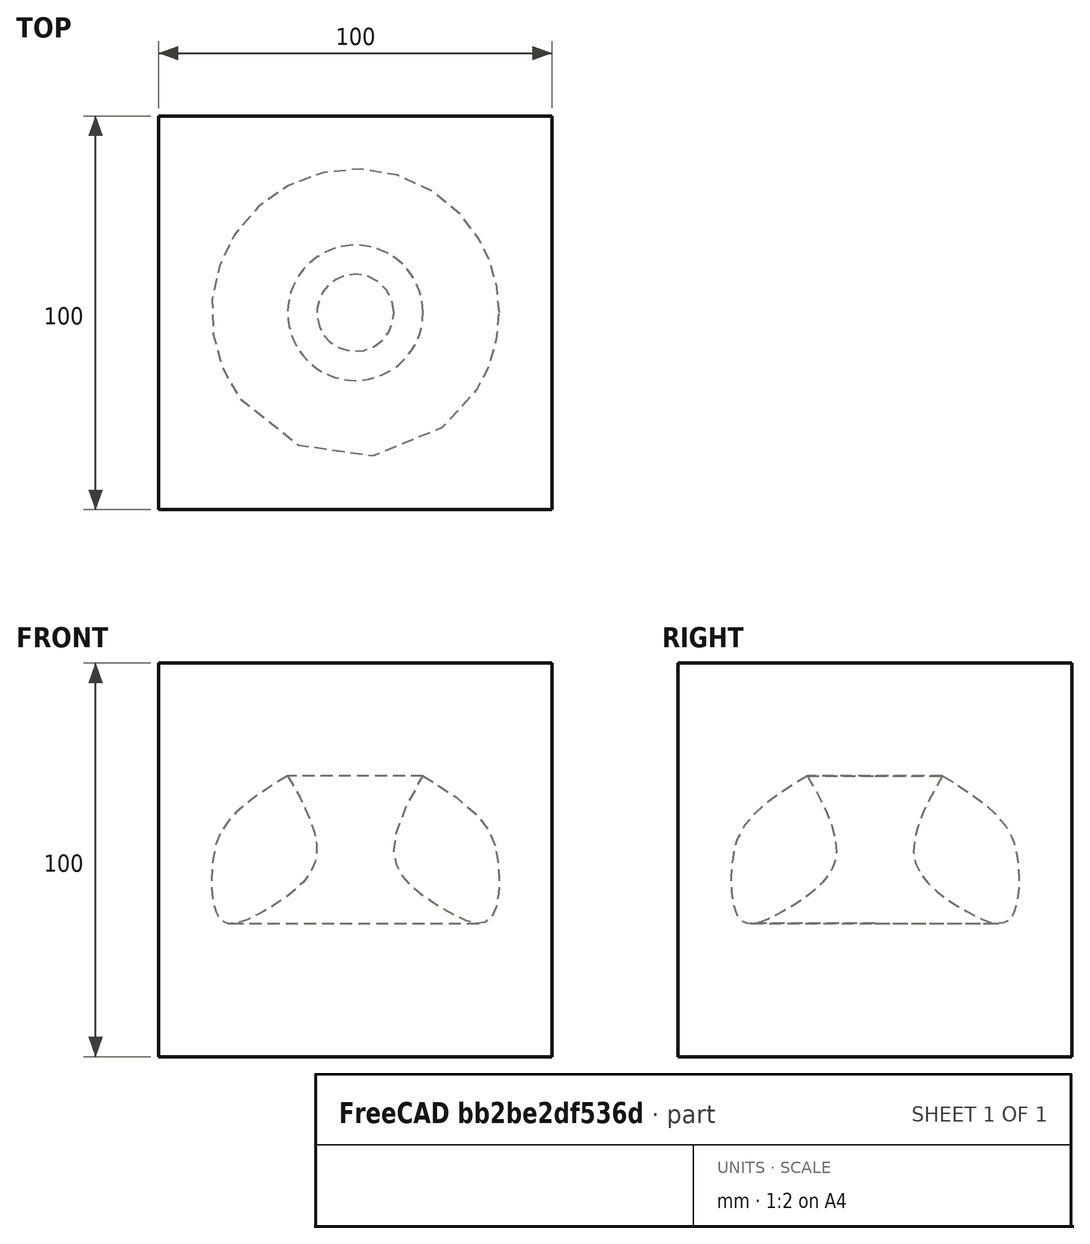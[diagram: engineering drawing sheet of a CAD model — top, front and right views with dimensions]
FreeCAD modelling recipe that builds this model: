
FCSTD DOCUMENT  (FreeCAD 0.21R33694 (Git))
Label: revolveSingleEdge-Bspline
License: All rights reserved
LicenseURL: http://en.wikipedia.org/wiki/All_rights_reserved
objects: App::DocumentObjectGroupPython×1248, App::Part×2, Part::FeaturePython×1, Sketcher::SketchObject×1, Part::Revolution×1
note: 3 computed .brp shape members not serialized (recipe doc carries the construction recipe); baked Part::Feature solids carry a one-line shape summary decoded from their .brp

FEATURE [App::DocumentObjectGroupPython] HALFPI  # scripted group (container) (typed FeaturePython)
  name = HALFPI
  value = pi/2.
FEATURE [App::DocumentObjectGroupPython] PI  # scripted group (container) (typed FeaturePython)
  name = PI
  value = 1.*pi
FEATURE [App::DocumentObjectGroupPython] TWOPI  # scripted group (container) (typed FeaturePython)
  name = TWOPI
  value = 2.*pi
FEATURE [App::DocumentObjectGroupPython] Constants  # scripted group (container) (typed FeaturePython)
  Group = -> [HALFPI,PI,TWOPI]
FEATURE [App::DocumentObjectGroupPython] Variables  # scripted group (container) (typed FeaturePython)
FEATURE [App::DocumentObjectGroupPython] Quantities  # scripted group (container) (typed FeaturePython)
FEATURE [App::DocumentObjectGroupPython] Isotopes  # scripted group (container) (typed FeaturePython)
FEATURE [App::DocumentObjectGroupPython] Elements  # scripted group (container) (typed FeaturePython)
FEATURE [App::DocumentObjectGroupPython] G4Isotopes  # scripted group (container) (typed FeaturePython)
FEATURE [App::DocumentObjectGroupPython] H_element  # scripted group (container) (typed FeaturePython)
  Z = 1
  atom_value = 1.008
  formula = H
  name = H_element
FEATURE [App::DocumentObjectGroupPython] He_element  # scripted group (container) (typed FeaturePython)
  Z = 2
  atom_value = 4.0026
  formula = He
  name = He_element
FEATURE [App::DocumentObjectGroupPython] Li_element  # scripted group (container) (typed FeaturePython)
  Z = 3
  atom_value = 6.94
  formula = Li
  name = Li_element
FEATURE [App::DocumentObjectGroupPython] Be_element  # scripted group (container) (typed FeaturePython)
  Z = 4
  atom_value = 9.01218
  formula = Be
  name = Be_element
FEATURE [App::DocumentObjectGroupPython] B_element  # scripted group (container) (typed FeaturePython)
  Z = 5
  atom_value = 10.81
  formula = B
  name = B_element
FEATURE [App::DocumentObjectGroupPython] C_element  # scripted group (container) (typed FeaturePython)
  Z = 6
  atom_value = 12.011
  formula = C
  name = C_element
FEATURE [App::DocumentObjectGroupPython] N_element  # scripted group (container) (typed FeaturePython)
  Z = 7
  atom_value = 14.007
  formula = N
  name = N_element
FEATURE [App::DocumentObjectGroupPython] O_element  # scripted group (container) (typed FeaturePython)
  Z = 8
  atom_value = 15.999
  formula = O
  name = O_element
FEATURE [App::DocumentObjectGroupPython] F_element  # scripted group (container) (typed FeaturePython)
  Z = 9
  atom_value = 18.9984
  formula = F
  name = F_element
FEATURE [App::DocumentObjectGroupPython] Ne_element  # scripted group (container) (typed FeaturePython)
  Z = 10
  atom_value = 20.1797
  formula = Ne
  name = Ne_element
FEATURE [App::DocumentObjectGroupPython] Na_element  # scripted group (container) (typed FeaturePython)
  Z = 11
  atom_value = 22.9898
  formula = Na
  name = Na_element
FEATURE [App::DocumentObjectGroupPython] Mg_element  # scripted group (container) (typed FeaturePython)
  Z = 12
  atom_value = 24.305
  formula = Mg
  name = Mg_element
FEATURE [App::DocumentObjectGroupPython] Al_element  # scripted group (container) (typed FeaturePython)
  Z = 13
  atom_value = 26.9815
  formula = Al
  name = Al_element
FEATURE [App::DocumentObjectGroupPython] Si_element  # scripted group (container) (typed FeaturePython)
  Z = 14
  atom_value = 28.085
  formula = Si
  name = Si_element
FEATURE [App::DocumentObjectGroupPython] P_element  # scripted group (container) (typed FeaturePython)
  Z = 15
  atom_value = 30.9738
  formula = P
  name = P_element
FEATURE [App::DocumentObjectGroupPython] S_element  # scripted group (container) (typed FeaturePython)
  Z = 16
  atom_value = 32.06
  formula = S
  name = S_element
FEATURE [App::DocumentObjectGroupPython] Cl_element  # scripted group (container) (typed FeaturePython)
  Z = 17
  atom_value = 35.45
  formula = Cl
  name = Cl_element
FEATURE [App::DocumentObjectGroupPython] Ar_element  # scripted group (container) (typed FeaturePython)
  Z = 18
  atom_value = 39.95
  formula = Ar
  name = Ar_element
FEATURE [App::DocumentObjectGroupPython] K_element  # scripted group (container) (typed FeaturePython)
  Z = 19
  atom_value = 39.0983
  formula = K
  name = K_element
FEATURE [App::DocumentObjectGroupPython] Ca_element  # scripted group (container) (typed FeaturePython)
  Z = 20
  atom_value = 40.078
  formula = Ca
  name = Ca_element
FEATURE [App::DocumentObjectGroupPython] Sc_element  # scripted group (container) (typed FeaturePython)
  Z = 21
  atom_value = 44.9559
  formula = Sc
  name = Sc_element
FEATURE [App::DocumentObjectGroupPython] Ti_element  # scripted group (container) (typed FeaturePython)
  Z = 22
  atom_value = 47.867
  formula = Ti
  name = Ti_element
FEATURE [App::DocumentObjectGroupPython] V_element  # scripted group (container) (typed FeaturePython)
  Z = 23
  atom_value = 50.9415
  formula = V
  name = V_element
FEATURE [App::DocumentObjectGroupPython] Cr_element  # scripted group (container) (typed FeaturePython)
  Z = 24
  atom_value = 51.9961
  formula = Cr
  name = Cr_element
FEATURE [App::DocumentObjectGroupPython] Mn_element  # scripted group (container) (typed FeaturePython)
  Z = 25
  atom_value = 54.938
  formula = Mn
  name = Mn_element
FEATURE [App::DocumentObjectGroupPython] Fe_element  # scripted group (container) (typed FeaturePython)
  Z = 26
  atom_value = 55.845
  formula = Fe
  name = Fe_element
FEATURE [App::DocumentObjectGroupPython] Co_element  # scripted group (container) (typed FeaturePython)
  Z = 27
  atom_value = 58.9332
  formula = Co
  name = Co_element
FEATURE [App::DocumentObjectGroupPython] Ni_element  # scripted group (container) (typed FeaturePython)
  Z = 28
  atom_value = 58.6934
  formula = Ni
  name = Ni_element
FEATURE [App::DocumentObjectGroupPython] Cu_element  # scripted group (container) (typed FeaturePython)
  Z = 29
  atom_value = 63.546
  formula = Cu
  name = Cu_element
FEATURE [App::DocumentObjectGroupPython] Zn_element  # scripted group (container) (typed FeaturePython)
  Z = 30
  atom_value = 65.38
  formula = Zn
  name = Zn_element
FEATURE [App::DocumentObjectGroupPython] Ga_element  # scripted group (container) (typed FeaturePython)
  Z = 31
  atom_value = 69.723
  formula = Ga
  name = Ga_element
FEATURE [App::DocumentObjectGroupPython] Ge_element  # scripted group (container) (typed FeaturePython)
  Z = 32
  atom_value = 72.63
  formula = Ge
  name = Ge_element
FEATURE [App::DocumentObjectGroupPython] As_element  # scripted group (container) (typed FeaturePython)
  Z = 33
  atom_value = 74.9216
  formula = As
  name = As_element
FEATURE [App::DocumentObjectGroupPython] Se_element  # scripted group (container) (typed FeaturePython)
  Z = 34
  atom_value = 78.971
  formula = Se
  name = Se_element
FEATURE [App::DocumentObjectGroupPython] Br_element  # scripted group (container) (typed FeaturePython)
  Z = 35
  atom_value = 79.904
  formula = Br
  name = Br_element
FEATURE [App::DocumentObjectGroupPython] Kr_element  # scripted group (container) (typed FeaturePython)
  Z = 36
  atom_value = 83.798
  formula = Kr
  name = Kr_element
FEATURE [App::DocumentObjectGroupPython] Rb_element  # scripted group (container) (typed FeaturePython)
  Z = 37
  atom_value = 85.4678
  formula = Rb
  name = Rb_element
FEATURE [App::DocumentObjectGroupPython] Sr_element  # scripted group (container) (typed FeaturePython)
  Z = 38
  atom_value = 87.62
  formula = Sr
  name = Sr_element
FEATURE [App::DocumentObjectGroupPython] Y_element  # scripted group (container) (typed FeaturePython)
  Z = 39
  atom_value = 88.9058
  formula = Y
  name = Y_element
FEATURE [App::DocumentObjectGroupPython] Zr_element  # scripted group (container) (typed FeaturePython)
  Z = 40
  atom_value = 91.224
  formula = Zr
  name = Zr_element
FEATURE [App::DocumentObjectGroupPython] Nb_element  # scripted group (container) (typed FeaturePython)
  Z = 41
  atom_value = 92.9064
  formula = Nb
  name = Nb_element
FEATURE [App::DocumentObjectGroupPython] Mo_element  # scripted group (container) (typed FeaturePython)
  Z = 42
  atom_value = 95.95
  formula = Mo
  name = Mo_element
FEATURE [App::DocumentObjectGroupPython] Tc_element  # scripted group (container) (typed FeaturePython)
  Z = 43
  atom_value = 97
  formula = Tc
  name = Tc_element
FEATURE [App::DocumentObjectGroupPython] Ru_element  # scripted group (container) (typed FeaturePython)
  Z = 44
  atom_value = 101.07
  formula = Ru
  name = Ru_element
FEATURE [App::DocumentObjectGroupPython] Rh_element  # scripted group (container) (typed FeaturePython)
  Z = 45
  atom_value = 102.905
  formula = Rh
  name = Rh_element
FEATURE [App::DocumentObjectGroupPython] Pd_element  # scripted group (container) (typed FeaturePython)
  Z = 46
  atom_value = 106.42
  formula = Pd
  name = Pd_element
FEATURE [App::DocumentObjectGroupPython] Ag_element  # scripted group (container) (typed FeaturePython)
  Z = 47
  atom_value = 107.868
  formula = Ag
  name = Ag_element
FEATURE [App::DocumentObjectGroupPython] Cd_element  # scripted group (container) (typed FeaturePython)
  Z = 48
  atom_value = 112.414
  formula = Cd
  name = Cd_element
FEATURE [App::DocumentObjectGroupPython] In_element  # scripted group (container) (typed FeaturePython)
  Z = 49
  atom_value = 114.818
  formula = In
  name = In_element
FEATURE [App::DocumentObjectGroupPython] Sn_element  # scripted group (container) (typed FeaturePython)
  Z = 50
  atom_value = 118.71
  formula = Sn
  name = Sn_element
FEATURE [App::DocumentObjectGroupPython] Sb_element  # scripted group (container) (typed FeaturePython)
  Z = 51
  atom_value = 121.76
  formula = Sb
  name = Sb_element
FEATURE [App::DocumentObjectGroupPython] Te_element  # scripted group (container) (typed FeaturePython)
  Z = 52
  atom_value = 127.6
  formula = Te
  name = Te_element
FEATURE [App::DocumentObjectGroupPython] I_element  # scripted group (container) (typed FeaturePython)
  Z = 53
  atom_value = 126.904
  formula = I
  name = I_element
FEATURE [App::DocumentObjectGroupPython] Xe_element  # scripted group (container) (typed FeaturePython)
  Z = 54
  atom_value = 131.293
  formula = Xe
  name = Xe_element
FEATURE [App::DocumentObjectGroupPython] Cs_element  # scripted group (container) (typed FeaturePython)
  Z = 55
  atom_value = 132.905
  formula = Cs
  name = Cs_element
FEATURE [App::DocumentObjectGroupPython] Ba_element  # scripted group (container) (typed FeaturePython)
  Z = 56
  atom_value = 137.327
  formula = Ba
  name = Ba_element
FEATURE [App::DocumentObjectGroupPython] La_element  # scripted group (container) (typed FeaturePython)
  Z = 57
  atom_value = 138.905
  formula = La
  name = La_element
FEATURE [App::DocumentObjectGroupPython] Ce_element  # scripted group (container) (typed FeaturePython)
  Z = 58
  atom_value = 140.116
  formula = Ce
  name = Ce_element
FEATURE [App::DocumentObjectGroupPython] Pr_element  # scripted group (container) (typed FeaturePython)
  Z = 59
  atom_value = 140.908
  formula = Pr
  name = Pr_element
FEATURE [App::DocumentObjectGroupPython] Nd_element  # scripted group (container) (typed FeaturePython)
  Z = 60
  atom_value = 144.242
  formula = Nd
  name = Nd_element
FEATURE [App::DocumentObjectGroupPython] Pm_element  # scripted group (container) (typed FeaturePython)
  Z = 61
  atom_value = 145
  formula = Pm
  name = Pm_element
FEATURE [App::DocumentObjectGroupPython] Sm_element  # scripted group (container) (typed FeaturePython)
  Z = 62
  atom_value = 150.36
  formula = Sm
  name = Sm_element
FEATURE [App::DocumentObjectGroupPython] Eu_element  # scripted group (container) (typed FeaturePython)
  Z = 63
  atom_value = 151.964
  formula = Eu
  name = Eu_element
FEATURE [App::DocumentObjectGroupPython] Gd_element  # scripted group (container) (typed FeaturePython)
  Z = 64
  atom_value = 157.25
  formula = Gd
  name = Gd_element
FEATURE [App::DocumentObjectGroupPython] Tb_element  # scripted group (container) (typed FeaturePython)
  Z = 65
  atom_value = 158.925
  formula = Tb
  name = Tb_element
FEATURE [App::DocumentObjectGroupPython] Dy_element  # scripted group (container) (typed FeaturePython)
  Z = 66
  atom_value = 162.5
  formula = Dy
  name = Dy_element
FEATURE [App::DocumentObjectGroupPython] Ho_element  # scripted group (container) (typed FeaturePython)
  Z = 67
  atom_value = 164.93
  formula = Ho
  name = Ho_element
FEATURE [App::DocumentObjectGroupPython] Er_element  # scripted group (container) (typed FeaturePython)
  Z = 68
  atom_value = 167.259
  formula = Er
  name = Er_element
FEATURE [App::DocumentObjectGroupPython] Tm_element  # scripted group (container) (typed FeaturePython)
  Z = 69
  atom_value = 168.934
  formula = Tm
  name = Tm_element
FEATURE [App::DocumentObjectGroupPython] Yb_element  # scripted group (container) (typed FeaturePython)
  Z = 70
  atom_value = 173.045
  formula = Yb
  name = Yb_element
FEATURE [App::DocumentObjectGroupPython] Lu_element  # scripted group (container) (typed FeaturePython)
  Z = 71
  atom_value = 174.967
  formula = Lu
  name = Lu_element
FEATURE [App::DocumentObjectGroupPython] Hf_element  # scripted group (container) (typed FeaturePython)
  Z = 72
  atom_value = 178.49
  formula = Hf
  name = Hf_element
FEATURE [App::DocumentObjectGroupPython] Ta_element  # scripted group (container) (typed FeaturePython)
  Z = 73
  atom_value = 180.948
  formula = Ta
  name = Ta_element
FEATURE [App::DocumentObjectGroupPython] W_element  # scripted group (container) (typed FeaturePython)
  Z = 74
  atom_value = 183.84
  formula = W
  name = W_element
FEATURE [App::DocumentObjectGroupPython] Re_element  # scripted group (container) (typed FeaturePython)
  Z = 75
  atom_value = 186.207
  formula = Re
  name = Re_element
FEATURE [App::DocumentObjectGroupPython] Os_element  # scripted group (container) (typed FeaturePython)
  Z = 76
  atom_value = 190.23
  formula = Os
  name = Os_element
FEATURE [App::DocumentObjectGroupPython] Ir_element  # scripted group (container) (typed FeaturePython)
  Z = 77
  atom_value = 192.217
  formula = Ir
  name = Ir_element
FEATURE [App::DocumentObjectGroupPython] Pt_element  # scripted group (container) (typed FeaturePython)
  Z = 78
  atom_value = 195.084
  formula = Pt
  name = Pt_element
FEATURE [App::DocumentObjectGroupPython] Au_element  # scripted group (container) (typed FeaturePython)
  Z = 79
  atom_value = 196.967
  formula = Au
  name = Au_element
FEATURE [App::DocumentObjectGroupPython] Hg_element  # scripted group (container) (typed FeaturePython)
  Z = 80
  atom_value = 200.592
  formula = Hg
  name = Hg_element
FEATURE [App::DocumentObjectGroupPython] Tl_element  # scripted group (container) (typed FeaturePython)
  Z = 81
  atom_value = 204.38
  formula = Tl
  name = Tl_element
FEATURE [App::DocumentObjectGroupPython] Pb_element  # scripted group (container) (typed FeaturePython)
  Z = 82
  atom_value = 207.2
  formula = Pb
  name = Pb_element
FEATURE [App::DocumentObjectGroupPython] Bi_element  # scripted group (container) (typed FeaturePython)
  Z = 83
  atom_value = 208.98
  formula = Bi
  name = Bi_element
FEATURE [App::DocumentObjectGroupPython] Po_element  # scripted group (container) (typed FeaturePython)
  Z = 84
  atom_value = 209
  formula = Po
  name = Po_element
FEATURE [App::DocumentObjectGroupPython] At_element  # scripted group (container) (typed FeaturePython)
  Z = 85
  atom_value = 210
  formula = At
  name = At_element
FEATURE [App::DocumentObjectGroupPython] Rn_element  # scripted group (container) (typed FeaturePython)
  Z = 86
  atom_value = 222
  formula = Rn
  name = Rn_element
FEATURE [App::DocumentObjectGroupPython] Fr_element  # scripted group (container) (typed FeaturePython)
  Z = 87
  atom_value = 223
  formula = Fr
  name = Fr_element
FEATURE [App::DocumentObjectGroupPython] Ra_element  # scripted group (container) (typed FeaturePython)
  Z = 88
  atom_value = 226
  formula = Ra
  name = Ra_element
FEATURE [App::DocumentObjectGroupPython] Ac_element  # scripted group (container) (typed FeaturePython)
  Z = 89
  atom_value = 227
  formula = Ac
  name = Ac_element
FEATURE [App::DocumentObjectGroupPython] Th_element  # scripted group (container) (typed FeaturePython)
  Z = 90
  atom_value = 232.038
  formula = Th
  name = Th_element
FEATURE [App::DocumentObjectGroupPython] Pa_element  # scripted group (container) (typed FeaturePython)
  Z = 91
  atom_value = 231.036
  formula = Pa
  name = Pa_element
FEATURE [App::DocumentObjectGroupPython] U_element  # scripted group (container) (typed FeaturePython)
  Z = 92
  atom_value = 238.029
  formula = U
  name = U_element
FEATURE [App::DocumentObjectGroupPython] Np_element  # scripted group (container) (typed FeaturePython)
  Z = 93
  atom_value = 237
  formula = Np
  name = Np_element
FEATURE [App::DocumentObjectGroupPython] Pu_element  # scripted group (container) (typed FeaturePython)
  Z = 94
  atom_value = 244
  formula = Pu
  name = Pu_element
FEATURE [App::DocumentObjectGroupPython] Am_element  # scripted group (container) (typed FeaturePython)
  Z = 95
  atom_value = 243
  formula = Am
  name = Am_element
FEATURE [App::DocumentObjectGroupPython] Cm_element  # scripted group (container) (typed FeaturePython)
  Z = 96
  atom_value = 247
  formula = Cm
  name = Cm_element
FEATURE [App::DocumentObjectGroupPython] Bk_element  # scripted group (container) (typed FeaturePython)
  Z = 97
  atom_value = 247
  formula = Bk
  name = Bk_element
FEATURE [App::DocumentObjectGroupPython] Cf_element  # scripted group (container) (typed FeaturePython)
  Z = 98
  atom_value = 251
  formula = Cf
  name = Cf_element
FEATURE [App::DocumentObjectGroupPython] G4Elements  # scripted group (container) (typed FeaturePython)
  Group = -> [H_element,He_element,Li_element,Be_element,B_element,C_element,N_element,O_element,F_element,Ne_element,Na_element,Mg_element,Al_element,Si_element,P_element,S_element,Cl_element,Ar_element,K_element,Ca_element,Sc_element,Ti_element,V_element,Cr_element,Mn_element,Fe_element,Co_element,Ni_element,Cu_element,Zn_element,Ga_element,Ge_element,As_element,Se_element,Br_element,Kr_element,Rb_element,+61 more]
FEATURE [App::DocumentObjectGroupPython] H_element001  label="H_element : 0.101"  # scripted group (container) (typed FeaturePython)
  n = 0.101327
FEATURE [App::DocumentObjectGroupPython] C_element001  label="C_element : 0.775"  # scripted group (container) (typed FeaturePython)
  n = 0.7755
FEATURE [App::DocumentObjectGroupPython] N_element001  label="N_element : 0.035"  # scripted group (container) (typed FeaturePython)
  n = 0.035057
FEATURE [App::DocumentObjectGroupPython] O_element001  label="O_element : 0.052"  # scripted group (container) (typed FeaturePython)
  n = 0.0523159
FEATURE [App::DocumentObjectGroupPython] F_element001  label="F_element : 0.017"  # scripted group (container) (typed FeaturePython)
  n = 0.017422
FEATURE [App::DocumentObjectGroupPython] Ca_element001  label="Ca_element : 0.018"  # scripted group (container) (typed FeaturePython)
  n = 0.018378
FEATURE [App::DocumentObjectGroupPython] G4_A_150_TISSUE  label="G4_A-150_TISSUE"  # scripted group (container) (typed FeaturePython)
  Dunit = g/cm3
  Dvalue = 1.127
  Group = -> [H_element001,C_element001,N_element001,O_element001,F_element001,Ca_element001]
  conduct = 2
  density = 1
  expand = 3
  formula = G4_A-150_TISSUE
  name = G4_A-150_TISSUE
  specific = 4
FEATURE [App::DocumentObjectGroupPython] C_element002  label="C_element : 3"  # scripted group (container) (typed FeaturePython)
  n = 3
  ref = C_element
FEATURE [App::DocumentObjectGroupPython] H_element002  label="H_element : 6"  # scripted group (container) (typed FeaturePython)
  n = 6
  ref = H_element
FEATURE [App::DocumentObjectGroupPython] O_element002  label="O_element : 1"  # scripted group (container) (typed FeaturePython)
  n = 1
  ref = O_element
FEATURE [App::DocumentObjectGroupPython] G4_ACETONE  # scripted group (container) (typed FeaturePython)
  Dunit = g/cm3
  Dvalue = 0.7899
  Group = -> [C_element002,H_element002,O_element002]
  conduct = 2
  density = 1
  expand = 3
  formula = G4_ACETONE
  name = G4_ACETONE
  specific = 4
FEATURE [App::DocumentObjectGroupPython] C_element003  label="C_element : 2"  # scripted group (container) (typed FeaturePython)
  n = 2
  ref = C_element
FEATURE [App::DocumentObjectGroupPython] H_element003  label="H_element : 2"  # scripted group (container) (typed FeaturePython)
  n = 2
  ref = H_element
FEATURE [App::DocumentObjectGroupPython] G4_ACETYLENE  # scripted group (container) (typed FeaturePython)
  Dunit = g/cm3
  Dvalue = 0.0010967
  Group = -> [C_element003,H_element003]
  conduct = 2
  density = 1
  expand = 3
  formula = G4_ACETYLENE
  name = G4_ACETYLENE
  specific = 4
FEATURE [App::DocumentObjectGroupPython] C_element004  label="C_element : 5"  # scripted group (container) (typed FeaturePython)
  n = 5
  ref = C_element
FEATURE [App::DocumentObjectGroupPython] H_element004  label="H_element : 5"  # scripted group (container) (typed FeaturePython)
  n = 5
  ref = H_element
FEATURE [App::DocumentObjectGroupPython] N_element002  label="N_element : 5"  # scripted group (container) (typed FeaturePython)
  n = 5
  ref = N_element
FEATURE [App::DocumentObjectGroupPython] G4_ADENINE  # scripted group (container) (typed FeaturePython)
  Dunit = g/cm3
  Dvalue = 1.6
  Group = -> [C_element004,H_element004,N_element002]
  conduct = 2
  density = 1
  expand = 3
  formula = G4_ADENINE
  name = G4_ADENINE
  specific = 4
FEATURE [App::DocumentObjectGroupPython] H_element005  label="H_element : 0.114"  # scripted group (container) (typed FeaturePython)
  n = 0.114
FEATURE [App::DocumentObjectGroupPython] C_element005  label="C_element : 0.598"  # scripted group (container) (typed FeaturePython)
  n = 0.598
FEATURE [App::DocumentObjectGroupPython] N_element003  label="N_element : 0.007"  # scripted group (container) (typed FeaturePython)
  n = 0.007
FEATURE [App::DocumentObjectGroupPython] O_element003  label="O_element : 0.278"  # scripted group (container) (typed FeaturePython)
  n = 0.278
FEATURE [App::DocumentObjectGroupPython] Na_element001  label="Na_element : 0.001"  # scripted group (container) (typed FeaturePython)
  n = 0.001
FEATURE [App::DocumentObjectGroupPython] S_element001  label="S_element : 0.001"  # scripted group (container) (typed FeaturePython)
  n = 0.001
FEATURE [App::DocumentObjectGroupPython] Cl_element001  label="Cl_element : 0.001"  # scripted group (container) (typed FeaturePython)
  n = 0.001
FEATURE [App::DocumentObjectGroupPython] G4_ADIPOSE_TISSUE_ICRP  # scripted group (container) (typed FeaturePython)
  Dunit = g/cm3
  Dvalue = 0.95
  Group = -> [H_element005,C_element005,N_element003,O_element003,Na_element001,S_element001,Cl_element001]
  conduct = 2
  density = 1
  expand = 3
  formula = G4_ADIPOSE_TISSUE_ICRP
  name = G4_ADIPOSE_TISSUE_ICRP
  specific = 4
FEATURE [App::DocumentObjectGroupPython] C_element006  label="C_element : 0.000"  # scripted group (container) (typed FeaturePython)
  n = 0.000124
FEATURE [App::DocumentObjectGroupPython] N_element004  label="N_element : 0.755"  # scripted group (container) (typed FeaturePython)
  n = 0.755268
FEATURE [App::DocumentObjectGroupPython] O_element004  label="O_element : 0.232"  # scripted group (container) (typed FeaturePython)
  n = 0.231781
FEATURE [App::DocumentObjectGroupPython] Ar_element001  label="Ar_element : 0.013"  # scripted group (container) (typed FeaturePython)
  n = 0.012827
FEATURE [App::DocumentObjectGroupPython] G4_AIR  # scripted group (container) (typed FeaturePython)
  Dunit = g/cm3
  Dvalue = 0.00120479
  Group = -> [C_element006,N_element004,O_element004,Ar_element001]
  conduct = 2
  density = 1
  expand = 3
  formula = G4_AIR
  name = G4_AIR
  specific = 4
FEATURE [App::DocumentObjectGroupPython] C_element007  label="C_element : 006"  # scripted group (container) (typed FeaturePython)
  n = 3
  ref = C_element
FEATURE [App::DocumentObjectGroupPython] H_element006  label="H_element : 7"  # scripted group (container) (typed FeaturePython)
  n = 7
  ref = H_element
FEATURE [App::DocumentObjectGroupPython] N_element005  label="N_element : 1"  # scripted group (container) (typed FeaturePython)
  n = 1
  ref = N_element
FEATURE [App::DocumentObjectGroupPython] O_element005  label="O_element : 2"  # scripted group (container) (typed FeaturePython)
  n = 2
  ref = O_element
FEATURE [App::DocumentObjectGroupPython] G4_ALANINE  # scripted group (container) (typed FeaturePython)
  Dunit = g/cm3
  Dvalue = 1.42
  Group = -> [C_element007,H_element006,N_element005,O_element005]
  conduct = 2
  density = 1
  expand = 3
  formula = G4_ALANINE
  name = G4_ALANINE
  specific = 4
FEATURE [App::DocumentObjectGroupPython] Al_element001  label="Al_element : 2"  # scripted group (container) (typed FeaturePython)
  n = 2
  ref = Al_element
FEATURE [App::DocumentObjectGroupPython] O_element006  label="O_element : 3"  # scripted group (container) (typed FeaturePython)
  n = 3
  ref = O_element
FEATURE [App::DocumentObjectGroupPython] G4_ALUMINUM_OXIDE  # scripted group (container) (typed FeaturePython)
  Dunit = g/cm3
  Dvalue = 3.97
  Group = -> [Al_element001,O_element006]
  conduct = 2
  density = 1
  expand = 3
  formula = G4_ALUMINUM_OXIDE
  name = G4_ALUMINUM_OXIDE
  specific = 4
FEATURE [App::DocumentObjectGroupPython] H_element007  label="H_element : 0.106"  # scripted group (container) (typed FeaturePython)
  n = 0.10593
FEATURE [App::DocumentObjectGroupPython] C_element008  label="C_element : 0.789"  # scripted group (container) (typed FeaturePython)
  n = 0.788974
FEATURE [App::DocumentObjectGroupPython] O_element007  label="O_element : 0.105"  # scripted group (container) (typed FeaturePython)
  n = 0.105096
FEATURE [App::DocumentObjectGroupPython] G4_AMBER  # scripted group (container) (typed FeaturePython)
  Dunit = g/cm3
  Dvalue = 1.1
  Group = -> [H_element007,C_element008,O_element007]
  conduct = 2
  density = 1
  expand = 3
  formula = G4_AMBER
  name = G4_AMBER
  specific = 4
FEATURE [App::DocumentObjectGroupPython] N_element006  label="N_element : 006"  # scripted group (container) (typed FeaturePython)
  n = 1
  ref = N_element
FEATURE [App::DocumentObjectGroupPython] H_element008  label="H_element : 3"  # scripted group (container) (typed FeaturePython)
  n = 3
  ref = H_element
FEATURE [App::DocumentObjectGroupPython] G4_AMMONIA  # scripted group (container) (typed FeaturePython)
  Dunit = g/cm3
  Dvalue = 0.000826019
  Group = -> [N_element006,H_element008]
  conduct = 2
  density = 1
  expand = 3
  formula = G4_AMMONIA
  name = G4_AMMONIA
  specific = 4
FEATURE [App::DocumentObjectGroupPython] C_element009  label="C_element : 6"  # scripted group (container) (typed FeaturePython)
  n = 6
  ref = C_element
FEATURE [App::DocumentObjectGroupPython] H_element009  label="H_element : 008"  # scripted group (container) (typed FeaturePython)
  n = 7
  ref = H_element
FEATURE [App::DocumentObjectGroupPython] N_element007  label="N_element : 007"  # scripted group (container) (typed FeaturePython)
  n = 1
  ref = N_element
FEATURE [App::DocumentObjectGroupPython] G4_ANILINE  # scripted group (container) (typed FeaturePython)
  Dunit = g/cm3
  Dvalue = 1.0235
  Group = -> [C_element009,H_element009,N_element007]
  conduct = 2
  density = 1
  expand = 3
  formula = G4_ANILINE
  name = G4_ANILINE
  specific = 4
FEATURE [App::DocumentObjectGroupPython] C_element010  label="C_element : 14"  # scripted group (container) (typed FeaturePython)
  n = 14
  ref = C_element
FEATURE [App::DocumentObjectGroupPython] H_element010  label="H_element : 10"  # scripted group (container) (typed FeaturePython)
  n = 10
  ref = H_element
FEATURE [App::DocumentObjectGroupPython] G4_ANTHRACENE  # scripted group (container) (typed FeaturePython)
  Dunit = g/cm3
  Dvalue = 1.283
  Group = -> [C_element010,H_element010]
  conduct = 2
  density = 1
  expand = 3
  formula = G4_ANTHRACENE
  name = G4_ANTHRACENE
  specific = 4
FEATURE [App::DocumentObjectGroupPython] H_element011  label="H_element : 0.065"  # scripted group (container) (typed FeaturePython)
  n = 0.0654709
FEATURE [App::DocumentObjectGroupPython] C_element011  label="C_element : 0.537"  # scripted group (container) (typed FeaturePython)
  n = 0.536944
FEATURE [App::DocumentObjectGroupPython] N_element008  label="N_element : 0.021"  # scripted group (container) (typed FeaturePython)
  n = 0.0215
FEATURE [App::DocumentObjectGroupPython] O_element008  label="O_element : 0.032"  # scripted group (container) (typed FeaturePython)
  n = 0.032085
FEATURE [App::DocumentObjectGroupPython] F_element002  label="F_element : 0.167"  # scripted group (container) (typed FeaturePython)
  n = 0.167411
FEATURE [App::DocumentObjectGroupPython] Ca_element002  label="Ca_element : 0.177"  # scripted group (container) (typed FeaturePython)
  n = 0.176589
FEATURE [App::DocumentObjectGroupPython] G4_B_100_BONE  label="G4_B-100_BONE"  # scripted group (container) (typed FeaturePython)
  Dunit = g/cm3
  Dvalue = 1.45
  Group = -> [H_element011,C_element011,N_element008,O_element008,F_element002,Ca_element002]
  conduct = 2
  density = 1
  expand = 3
  formula = G4_B-100_BONE
  name = G4_B-100_BONE
  specific = 4
FEATURE [App::DocumentObjectGroupPython] H_element012  label="H_element : 0.057"  # scripted group (container) (typed FeaturePython)
  n = 0.057441
FEATURE [App::DocumentObjectGroupPython] C_element012  label="C_element : 0.790"  # scripted group (container) (typed FeaturePython)
  n = 0.774591
FEATURE [App::DocumentObjectGroupPython] O_element009  label="O_element : 0.168"  # scripted group (container) (typed FeaturePython)
  n = 0.167968
FEATURE [App::DocumentObjectGroupPython] G4_BAKELITE  # scripted group (container) (typed FeaturePython)
  Dunit = g/cm3
  Dvalue = 1.25
  Group = -> [H_element012,C_element012,O_element009]
  conduct = 2
  density = 1
  expand = 3
  formula = G4_BAKELITE
  name = G4_BAKELITE
  specific = 4
FEATURE [App::DocumentObjectGroupPython] Ba_element001  label="Ba_element : 1"  # scripted group (container) (typed FeaturePython)
  n = 1
  ref = Ba_element
FEATURE [App::DocumentObjectGroupPython] F_element003  label="F_element : 2"  # scripted group (container) (typed FeaturePython)
  n = 2
  ref = F_element
FEATURE [App::DocumentObjectGroupPython] G4_BARIUM_FLUORIDE  # scripted group (container) (typed FeaturePython)
  Dunit = g/cm3
  Dvalue = 4.89
  Group = -> [Ba_element001,F_element003]
  conduct = 2
  density = 1
  expand = 3
  formula = G4_BARIUM_FLUORIDE
  name = G4_BARIUM_FLUORIDE
  specific = 4
FEATURE [App::DocumentObjectGroupPython] Ba_element002  label="Ba_element : 002"  # scripted group (container) (typed FeaturePython)
  n = 1
  ref = Ba_element
FEATURE [App::DocumentObjectGroupPython] S_element002  label="S_element : 1"  # scripted group (container) (typed FeaturePython)
  n = 1
  ref = S_element
FEATURE [App::DocumentObjectGroupPython] O_element010  label="O_element : 4"  # scripted group (container) (typed FeaturePython)
  n = 4
  ref = O_element
FEATURE [App::DocumentObjectGroupPython] G4_BARIUM_SULFATE  # scripted group (container) (typed FeaturePython)
  Dunit = g/cm3
  Dvalue = 4.5
  Group = -> [Ba_element002,S_element002,O_element010]
  conduct = 2
  density = 1
  expand = 3
  formula = G4_BARIUM_SULFATE
  name = G4_BARIUM_SULFATE
  specific = 4
FEATURE [App::DocumentObjectGroupPython] C_element013  label="C_element : 007"  # scripted group (container) (typed FeaturePython)
  n = 6
  ref = C_element
FEATURE [App::DocumentObjectGroupPython] H_element013  label="H_element : 009"  # scripted group (container) (typed FeaturePython)
  n = 6
  ref = H_element
FEATURE [App::DocumentObjectGroupPython] G4_BENZENE  # scripted group (container) (typed FeaturePython)
  Dunit = g/cm3
  Dvalue = 0.87865
  Group = -> [C_element013,H_element013]
  conduct = 2
  density = 1
  expand = 3
  formula = G4_BENZENE
  name = G4_BENZENE
  specific = 4
FEATURE [App::DocumentObjectGroupPython] Be_element001  label="Be_element : 1"  # scripted group (container) (typed FeaturePython)
  n = 1
  ref = Be_element
FEATURE [App::DocumentObjectGroupPython] O_element011  label="O_element : 005"  # scripted group (container) (typed FeaturePython)
  n = 1
  ref = O_element
FEATURE [App::DocumentObjectGroupPython] G4_BERYLLIUM_OXIDE  # scripted group (container) (typed FeaturePython)
  Dunit = g/cm3
  Dvalue = 3.01
  Group = -> [Be_element001,O_element011]
  conduct = 2
  density = 1
  expand = 3
  formula = G4_BERYLLIUM_OXIDE
  name = G4_BERYLLIUM_OXIDE
  specific = 4
FEATURE [App::DocumentObjectGroupPython] Bi_element001  label="Bi_element : 4"  # scripted group (container) (typed FeaturePython)
  n = 4
  ref = Bi_element
FEATURE [App::DocumentObjectGroupPython] Ge_element001  label="Ge_element : 3"  # scripted group (container) (typed FeaturePython)
  n = 3
  ref = Ge_element
FEATURE [App::DocumentObjectGroupPython] O_element012  label="O_element : 12"  # scripted group (container) (typed FeaturePython)
  n = 12
  ref = O_element
FEATURE [App::DocumentObjectGroupPython] G4_BGO  # scripted group (container) (typed FeaturePython)
  Dunit = g/cm3
  Dvalue = 7.13
  Group = -> [Bi_element001,Ge_element001,O_element012]
  conduct = 2
  density = 1
  expand = 3
  formula = G4_BGO
  name = G4_BGO
  specific = 4
FEATURE [App::DocumentObjectGroupPython] H_element014  label="H_element : 0.102"  # scripted group (container) (typed FeaturePython)
  n = 0.102
FEATURE [App::DocumentObjectGroupPython] C_element014  label="C_element : 0.110"  # scripted group (container) (typed FeaturePython)
  n = 0.11
FEATURE [App::DocumentObjectGroupPython] N_element009  label="N_element : 0.033"  # scripted group (container) (typed FeaturePython)
  n = 0.033
FEATURE [App::DocumentObjectGroupPython] O_element013  label="O_element : 0.745"  # scripted group (container) (typed FeaturePython)
  n = 0.745
FEATURE [App::DocumentObjectGroupPython] Na_element002  label="Na_element : 0.002"  # scripted group (container) (typed FeaturePython)
  n = 0.001
FEATURE [App::DocumentObjectGroupPython] P_element001  label="P_element : 0.001"  # scripted group (container) (typed FeaturePython)
  n = 0.001
FEATURE [App::DocumentObjectGroupPython] S_element003  label="S_element : 0.002"  # scripted group (container) (typed FeaturePython)
  n = 0.002
FEATURE [App::DocumentObjectGroupPython] Cl_element002  label="Cl_element : 0.003"  # scripted group (container) (typed FeaturePython)
  n = 0.003
FEATURE [App::DocumentObjectGroupPython] K_element001  label="K_element : 0.002"  # scripted group (container) (typed FeaturePython)
  n = 0.002
FEATURE [App::DocumentObjectGroupPython] Fe_element001  label="Fe_element : 0.001"  # scripted group (container) (typed FeaturePython)
  n = 0.001
FEATURE [App::DocumentObjectGroupPython] G4_BLOOD_ICRP  # scripted group (container) (typed FeaturePython)
  Dunit = g/cm3
  Dvalue = 1.06
  Group = -> [H_element014,C_element014,N_element009,O_element013,Na_element002,P_element001,S_element003,Cl_element002,K_element001,Fe_element001]
  conduct = 2
  density = 1
  expand = 3
  formula = G4_BLOOD_ICRP
  name = G4_BLOOD_ICRP
  specific = 4
FEATURE [App::DocumentObjectGroupPython] H_element015  label="H_element : 0.064"  # scripted group (container) (typed FeaturePython)
  n = 0.064
FEATURE [App::DocumentObjectGroupPython] C_element015  label="C_element : 0.278"  # scripted group (container) (typed FeaturePython)
  n = 0.278
FEATURE [App::DocumentObjectGroupPython] N_element010  label="N_element : 0.027"  # scripted group (container) (typed FeaturePython)
  n = 0.027
FEATURE [App::DocumentObjectGroupPython] O_element014  label="O_element : 0.410"  # scripted group (container) (typed FeaturePython)
  n = 0.41
FEATURE [App::DocumentObjectGroupPython] Mg_element001  label="Mg_element : 0.002"  # scripted group (container) (typed FeaturePython)
  n = 0.002
FEATURE [App::DocumentObjectGroupPython] P_element002  label="P_element : 0.070"  # scripted group (container) (typed FeaturePython)
  n = 0.07
FEATURE [App::DocumentObjectGroupPython] S_element004  label="S_element : 0.003"  # scripted group (container) (typed FeaturePython)
  n = 0.002
FEATURE [App::DocumentObjectGroupPython] Ca_element003  label="Ca_element : 0.147"  # scripted group (container) (typed FeaturePython)
  n = 0.147
FEATURE [App::DocumentObjectGroupPython] G4_BONE_COMPACT_ICRU  # scripted group (container) (typed FeaturePython)
  Dunit = g/cm3
  Dvalue = 1.85
  Group = -> [H_element015,C_element015,N_element010,O_element014,Mg_element001,P_element002,S_element004,Ca_element003]
  conduct = 2
  density = 1
  expand = 3
  formula = G4_BONE_COMPACT_ICRU
  name = G4_BONE_COMPACT_ICRU
  specific = 4
FEATURE [App::DocumentObjectGroupPython] H_element016  label="H_element : 0.034"  # scripted group (container) (typed FeaturePython)
  n = 0.034
FEATURE [App::DocumentObjectGroupPython] C_element016  label="C_element : 0.155"  # scripted group (container) (typed FeaturePython)
  n = 0.155
FEATURE [App::DocumentObjectGroupPython] N_element011  label="N_element : 0.042"  # scripted group (container) (typed FeaturePython)
  n = 0.042
FEATURE [App::DocumentObjectGroupPython] O_element015  label="O_element : 0.435"  # scripted group (container) (typed FeaturePython)
  n = 0.435
FEATURE [App::DocumentObjectGroupPython] Na_element003  label="Na_element : 0.003"  # scripted group (container) (typed FeaturePython)
  n = 0.001
FEATURE [App::DocumentObjectGroupPython] Mg_element002  label="Mg_element : 0.003"  # scripted group (container) (typed FeaturePython)
  n = 0.002
FEATURE [App::DocumentObjectGroupPython] P_element003  label="P_element : 0.103"  # scripted group (container) (typed FeaturePython)
  n = 0.103
FEATURE [App::DocumentObjectGroupPython] S_element005  label="S_element : 0.004"  # scripted group (container) (typed FeaturePython)
  n = 0.003
FEATURE [App::DocumentObjectGroupPython] Ca_element004  label="Ca_element : 0.225"  # scripted group (container) (typed FeaturePython)
  n = 0.225
FEATURE [App::DocumentObjectGroupPython] G4_BONE_CORTICAL_ICRP  # scripted group (container) (typed FeaturePython)
  Dunit = g/cm3
  Dvalue = 1.92
  Group = -> [H_element016,C_element016,N_element011,O_element015,Na_element003,Mg_element002,P_element003,S_element005,Ca_element004]
  conduct = 2
  density = 1
  expand = 3
  formula = G4_BONE_CORTICAL_ICRP
  name = G4_BONE_CORTICAL_ICRP
  specific = 4
FEATURE [App::DocumentObjectGroupPython] B_element001  label="B_element : 4"  # scripted group (container) (typed FeaturePython)
  n = 4
  ref = B_element
FEATURE [App::DocumentObjectGroupPython] C_element017  label="C_element : 1"  # scripted group (container) (typed FeaturePython)
  n = 1
  ref = C_element
FEATURE [App::DocumentObjectGroupPython] G4_BORON_CARBIDE  # scripted group (container) (typed FeaturePython)
  Dunit = g/cm3
  Dvalue = 2.52
  Group = -> [B_element001,C_element017]
  conduct = 2
  density = 1
  expand = 3
  formula = G4_BORON_CARBIDE
  name = G4_BORON_CARBIDE
  specific = 4
FEATURE [App::DocumentObjectGroupPython] B_element002  label="B_element : 2"  # scripted group (container) (typed FeaturePython)
  n = 2
  ref = B_element
FEATURE [App::DocumentObjectGroupPython] O_element016  label="O_element : 006"  # scripted group (container) (typed FeaturePython)
  n = 3
  ref = O_element
FEATURE [App::DocumentObjectGroupPython] G4_BORON_OXIDE  # scripted group (container) (typed FeaturePython)
  Dunit = g/cm3
  Dvalue = 1.812
  Group = -> [B_element002,O_element016]
  conduct = 2
  density = 1
  expand = 3
  formula = G4_BORON_OXIDE
  name = G4_BORON_OXIDE
  specific = 4
FEATURE [App::DocumentObjectGroupPython] H_element017  label="H_element : 0.107"  # scripted group (container) (typed FeaturePython)
  n = 0.107
FEATURE [App::DocumentObjectGroupPython] C_element018  label="C_element : 0.145"  # scripted group (container) (typed FeaturePython)
  n = 0.145
FEATURE [App::DocumentObjectGroupPython] N_element012  label="N_element : 0.022"  # scripted group (container) (typed FeaturePython)
  n = 0.022
FEATURE [App::DocumentObjectGroupPython] O_element017  label="O_element : 0.712"  # scripted group (container) (typed FeaturePython)
  n = 0.712
FEATURE [App::DocumentObjectGroupPython] Na_element004  label="Na_element : 0.004"  # scripted group (container) (typed FeaturePython)
  n = 0.002
FEATURE [App::DocumentObjectGroupPython] P_element004  label="P_element : 0.004"  # scripted group (container) (typed FeaturePython)
  n = 0.004
FEATURE [App::DocumentObjectGroupPython] S_element006  label="S_element : 0.005"  # scripted group (container) (typed FeaturePython)
  n = 0.002
FEATURE [App::DocumentObjectGroupPython] Cl_element003  label="Cl_element : 0.004"  # scripted group (container) (typed FeaturePython)
  n = 0.003
FEATURE [App::DocumentObjectGroupPython] K_element002  label="K_element : 0.003"  # scripted group (container) (typed FeaturePython)
  n = 0.003
FEATURE [App::DocumentObjectGroupPython] G4_BRAIN_ICRP  # scripted group (container) (typed FeaturePython)
  Dunit = g/cm3
  Dvalue = 1.04
  Group = -> [H_element017,C_element018,N_element012,O_element017,Na_element004,P_element004,S_element006,Cl_element003,K_element002]
  conduct = 2
  density = 1
  expand = 3
  formula = G4_BRAIN_ICRP
  name = G4_BRAIN_ICRP
  specific = 4
FEATURE [App::DocumentObjectGroupPython] C_element019  label="C_element : 4"  # scripted group (container) (typed FeaturePython)
  n = 4
  ref = C_element
FEATURE [App::DocumentObjectGroupPython] H_element018  label="H_element : 010"  # scripted group (container) (typed FeaturePython)
  n = 10
  ref = H_element
FEATURE [App::DocumentObjectGroupPython] G4_BUTANE  # scripted group (container) (typed FeaturePython)
  Dunit = g/cm3
  Dvalue = 0.00249343
  Group = -> [C_element019,H_element018]
  conduct = 2
  density = 1
  expand = 3
  formula = G4_BUTANE
  name = G4_BUTANE
  specific = 4
FEATURE [App::DocumentObjectGroupPython] C_element020  label="C_element : 008"  # scripted group (container) (typed FeaturePython)
  n = 4
  ref = C_element
FEATURE [App::DocumentObjectGroupPython] H_element019  label="H_element : 011"  # scripted group (container) (typed FeaturePython)
  n = 10
  ref = H_element
FEATURE [App::DocumentObjectGroupPython] O_element018  label="O_element : 007"  # scripted group (container) (typed FeaturePython)
  n = 1
  ref = O_element
FEATURE [App::DocumentObjectGroupPython] G4_N_BUTYL_ALCOHOL  label="G4_N-BUTYL_ALCOHOL"  # scripted group (container) (typed FeaturePython)
  Dunit = g/cm3
  Dvalue = 0.8098
  Group = -> [C_element020,H_element019,O_element018]
  conduct = 2
  density = 1
  expand = 3
  formula = G4_N-BUTYL_ALCOHOL
  name = G4_N-BUTYL_ALCOHOL
  specific = 4
FEATURE [App::DocumentObjectGroupPython] H_element020  label="H_element : 0.025"  # scripted group (container) (typed FeaturePython)
  n = 0.02468
FEATURE [App::DocumentObjectGroupPython] C_element021  label="C_element : 0.502"  # scripted group (container) (typed FeaturePython)
  n = 0.501611
FEATURE [App::DocumentObjectGroupPython] O_element019  label="O_element : 0.005"  # scripted group (container) (typed FeaturePython)
  n = 0.004527
FEATURE [App::DocumentObjectGroupPython] F_element004  label="F_element : 0.465"  # scripted group (container) (typed FeaturePython)
  n = 0.465209
FEATURE [App::DocumentObjectGroupPython] Si_element001  label="Si_element : 0.004"  # scripted group (container) (typed FeaturePython)
  n = 0.003973
FEATURE [App::DocumentObjectGroupPython] G4_C_552  label="G4_C-552"  # scripted group (container) (typed FeaturePython)
  Dunit = g/cm3
  Dvalue = 1.76
  Group = -> [H_element020,C_element021,O_element019,F_element004,Si_element001]
  conduct = 2
  density = 1
  expand = 3
  formula = G4_C-552
  name = G4_C-552
  specific = 4
FEATURE [App::DocumentObjectGroupPython] Cd_element001  label="Cd_element : 1"  # scripted group (container) (typed FeaturePython)
  n = 1
  ref = Cd_element
FEATURE [App::DocumentObjectGroupPython] Te_element001  label="Te_element : 1"  # scripted group (container) (typed FeaturePython)
  n = 1
  ref = Te_element
FEATURE [App::DocumentObjectGroupPython] G4_CADMIUM_TELLURIDE  # scripted group (container) (typed FeaturePython)
  Dunit = g/cm3
  Dvalue = 6.2
  Group = -> [Cd_element001,Te_element001]
  conduct = 2
  density = 1
  expand = 3
  formula = G4_CADMIUM_TELLURIDE
  name = G4_CADMIUM_TELLURIDE
  specific = 4
FEATURE [App::DocumentObjectGroupPython] Cd_element002  label="Cd_element : 002"  # scripted group (container) (typed FeaturePython)
  n = 1
  ref = Cd_element
FEATURE [App::DocumentObjectGroupPython] W_element001  label="W_element : 1"  # scripted group (container) (typed FeaturePython)
  n = 1
  ref = W_element
FEATURE [App::DocumentObjectGroupPython] O_element020  label="O_element : 008"  # scripted group (container) (typed FeaturePython)
  n = 4
  ref = O_element
FEATURE [App::DocumentObjectGroupPython] G4_CADMIUM_TUNGSTATE  # scripted group (container) (typed FeaturePython)
  Dunit = g/cm3
  Dvalue = 7.9
  Group = -> [Cd_element002,W_element001,O_element020]
  conduct = 2
  density = 1
  expand = 3
  formula = G4_CADMIUM_TUNGSTATE
  name = G4_CADMIUM_TUNGSTATE
  specific = 4
FEATURE [App::DocumentObjectGroupPython] Ca_element005  label="Ca_element : 1"  # scripted group (container) (typed FeaturePython)
  n = 1
  ref = Ca_element
FEATURE [App::DocumentObjectGroupPython] C_element022  label="C_element : 009"  # scripted group (container) (typed FeaturePython)
  n = 1
  ref = C_element
FEATURE [App::DocumentObjectGroupPython] O_element021  label="O_element : 009"  # scripted group (container) (typed FeaturePython)
  n = 3
  ref = O_element
FEATURE [App::DocumentObjectGroupPython] G4_CALCIUM_CARBONATE  # scripted group (container) (typed FeaturePython)
  Dunit = g/cm3
  Dvalue = 2.8
  Group = -> [Ca_element005,C_element022,O_element021]
  conduct = 2
  density = 1
  expand = 3
  formula = G4_CALCIUM_CARBONATE
  name = G4_CALCIUM_CARBONATE
  specific = 4
FEATURE [App::DocumentObjectGroupPython] Ca_element006  label="Ca_element : 002"  # scripted group (container) (typed FeaturePython)
  n = 1
  ref = Ca_element
FEATURE [App::DocumentObjectGroupPython] F_element005  label="F_element : 003"  # scripted group (container) (typed FeaturePython)
  n = 2
  ref = F_element
FEATURE [App::DocumentObjectGroupPython] G4_CALCIUM_FLUORIDE  # scripted group (container) (typed FeaturePython)
  Dunit = g/cm3
  Dvalue = 3.18
  Group = -> [Ca_element006,F_element005]
  conduct = 2
  density = 1
  expand = 3
  formula = G4_CALCIUM_FLUORIDE
  name = G4_CALCIUM_FLUORIDE
  specific = 4
FEATURE [App::DocumentObjectGroupPython] Ca_element007  label="Ca_element : 003"  # scripted group (container) (typed FeaturePython)
  n = 1
  ref = Ca_element
FEATURE [App::DocumentObjectGroupPython] O_element022  label="O_element : 010"  # scripted group (container) (typed FeaturePython)
  n = 1
  ref = O_element
FEATURE [App::DocumentObjectGroupPython] G4_CALCIUM_OXIDE  # scripted group (container) (typed FeaturePython)
  Dunit = g/cm3
  Dvalue = 3.3
  Group = -> [Ca_element007,O_element022]
  conduct = 2
  density = 1
  expand = 3
  formula = G4_CALCIUM_OXIDE
  name = G4_CALCIUM_OXIDE
  specific = 4
FEATURE [App::DocumentObjectGroupPython] Ca_element008  label="Ca_element : 004"  # scripted group (container) (typed FeaturePython)
  n = 1
  ref = Ca_element
FEATURE [App::DocumentObjectGroupPython] S_element007  label="S_element : 002"  # scripted group (container) (typed FeaturePython)
  n = 1
  ref = S_element
FEATURE [App::DocumentObjectGroupPython] O_element023  label="O_element : 011"  # scripted group (container) (typed FeaturePython)
  n = 4
  ref = O_element
FEATURE [App::DocumentObjectGroupPython] G4_CALCIUM_SULFATE  # scripted group (container) (typed FeaturePython)
  Dunit = g/cm3
  Dvalue = 2.96
  Group = -> [Ca_element008,S_element007,O_element023]
  conduct = 2
  density = 1
  expand = 3
  formula = G4_CALCIUM_SULFATE
  name = G4_CALCIUM_SULFATE
  specific = 4
FEATURE [App::DocumentObjectGroupPython] Ca_element009  label="Ca_element : 005"  # scripted group (container) (typed FeaturePython)
  n = 1
  ref = Ca_element
FEATURE [App::DocumentObjectGroupPython] W_element002  label="W_element : 002"  # scripted group (container) (typed FeaturePython)
  n = 1
  ref = W_element
FEATURE [App::DocumentObjectGroupPython] O_element024  label="O_element : 012"  # scripted group (container) (typed FeaturePython)
  n = 4
  ref = O_element
FEATURE [App::DocumentObjectGroupPython] G4_CALCIUM_TUNGSTATE  # scripted group (container) (typed FeaturePython)
  Dunit = g/cm3
  Dvalue = 6.062
  Group = -> [Ca_element009,W_element002,O_element024]
  conduct = 2
  density = 1
  expand = 3
  formula = G4_CALCIUM_TUNGSTATE
  name = G4_CALCIUM_TUNGSTATE
  specific = 4
FEATURE [App::DocumentObjectGroupPython] C_element023  label="C_element : 010"  # scripted group (container) (typed FeaturePython)
  n = 1
  ref = C_element
FEATURE [App::DocumentObjectGroupPython] O_element025  label="O_element : 013"  # scripted group (container) (typed FeaturePython)
  n = 2
  ref = O_element
FEATURE [App::DocumentObjectGroupPython] G4_CARBON_DIOXIDE  # scripted group (container) (typed FeaturePython)
  Dunit = g/cm3
  Dvalue = 0.00184212
  Group = -> [C_element023,O_element025]
  conduct = 2
  density = 1
  expand = 3
  formula = G4_CARBON_DIOXIDE
  name = G4_CARBON_DIOXIDE
  specific = 4
FEATURE [App::DocumentObjectGroupPython] C_element024  label="C_element : 011"  # scripted group (container) (typed FeaturePython)
  n = 1
  ref = C_element
FEATURE [App::DocumentObjectGroupPython] Cl_element004  label="Cl_element : 4"  # scripted group (container) (typed FeaturePython)
  n = 4
  ref = Cl_element
FEATURE [App::DocumentObjectGroupPython] G4_CARBON_TETRACHLORIDE  # scripted group (container) (typed FeaturePython)
  Dunit = g/cm3
  Dvalue = 1.594
  Group = -> [C_element024,Cl_element004]
  conduct = 2
  density = 1
  expand = 3
  formula = G4_CARBON_TETRACHLORIDE
  name = G4_CARBON_TETRACHLORIDE
  specific = 4
FEATURE [App::DocumentObjectGroupPython] C_element025  label="C_element : 012"  # scripted group (container) (typed FeaturePython)
  n = 6
  ref = C_element
FEATURE [App::DocumentObjectGroupPython] H_element021  label="H_element : 012"  # scripted group (container) (typed FeaturePython)
  n = 10
  ref = H_element
FEATURE [App::DocumentObjectGroupPython] O_element026  label="O_element : 5"  # scripted group (container) (typed FeaturePython)
  n = 5
  ref = O_element
FEATURE [App::DocumentObjectGroupPython] G4_CELLULOSE_CELLOPHANE  # scripted group (container) (typed FeaturePython)
  Dunit = g/cm3
  Dvalue = 1.42
  Group = -> [C_element025,H_element021,O_element026]
  conduct = 2
  density = 1
  expand = 3
  formula = G4_CELLULOSE_CELLOPHANE
  name = G4_CELLULOSE_CELLOPHANE
  specific = 4
FEATURE [App::DocumentObjectGroupPython] H_element022  label="H_element : 0.067"  # scripted group (container) (typed FeaturePython)
  n = 0.067125
FEATURE [App::DocumentObjectGroupPython] C_element026  label="C_element : 0.545"  # scripted group (container) (typed FeaturePython)
  n = 0.545403
FEATURE [App::DocumentObjectGroupPython] O_element027  label="O_element : 0.387"  # scripted group (container) (typed FeaturePython)
  n = 0.387472
FEATURE [App::DocumentObjectGroupPython] G4_CELLULOSE_BUTYRATE  # scripted group (container) (typed FeaturePython)
  Dunit = g/cm3
  Dvalue = 1.2
  Group = -> [H_element022,C_element026,O_element027]
  conduct = 2
  density = 1
  expand = 3
  formula = G4_CELLULOSE_BUTYRATE
  name = G4_CELLULOSE_BUTYRATE
  specific = 4
FEATURE [App::DocumentObjectGroupPython] H_element023  label="H_element : 0.029"  # scripted group (container) (typed FeaturePython)
  n = 0.029216
FEATURE [App::DocumentObjectGroupPython] C_element027  label="C_element : 0.271"  # scripted group (container) (typed FeaturePython)
  n = 0.271296
FEATURE [App::DocumentObjectGroupPython] N_element013  label="N_element : 0.121"  # scripted group (container) (typed FeaturePython)
  n = 0.121276
FEATURE [App::DocumentObjectGroupPython] O_element028  label="O_element : 0.578"  # scripted group (container) (typed FeaturePython)
  n = 0.578212
FEATURE [App::DocumentObjectGroupPython] G4_CELLULOSE_NITRATE  # scripted group (container) (typed FeaturePython)
  Dunit = g/cm3
  Dvalue = 1.49
  Group = -> [H_element023,C_element027,N_element013,O_element028]
  conduct = 2
  density = 1
  expand = 3
  formula = G4_CELLULOSE_NITRATE
  name = G4_CELLULOSE_NITRATE
  specific = 4
FEATURE [App::DocumentObjectGroupPython] H_element024  label="H_element : 0.108"  # scripted group (container) (typed FeaturePython)
  n = 0.107596
FEATURE [App::DocumentObjectGroupPython] N_element014  label="N_element : 0.001"  # scripted group (container) (typed FeaturePython)
  n = 0.0008
FEATURE [App::DocumentObjectGroupPython] O_element029  label="O_element : 0.875"  # scripted group (container) (typed FeaturePython)
  n = 0.874976
FEATURE [App::DocumentObjectGroupPython] S_element008  label="S_element : 0.015"  # scripted group (container) (typed FeaturePython)
  n = 0.014627
FEATURE [App::DocumentObjectGroupPython] Ce_element001  label="Ce_element : 0.002"  # scripted group (container) (typed FeaturePython)
  n = 0.002001
FEATURE [App::DocumentObjectGroupPython] G4_CERIC_SULFATE  # scripted group (container) (typed FeaturePython)
  Dunit = g/cm3
  Dvalue = 1.03
  Group = -> [H_element024,N_element014,O_element029,S_element008,Ce_element001]
  conduct = 2
  density = 1
  expand = 3
  formula = G4_CERIC_SULFATE
  name = G4_CERIC_SULFATE
  specific = 4
FEATURE [App::DocumentObjectGroupPython] Cs_element001  label="Cs_element : 1"  # scripted group (container) (typed FeaturePython)
  n = 1
  ref = Cs_element
FEATURE [App::DocumentObjectGroupPython] F_element006  label="F_element : 1"  # scripted group (container) (typed FeaturePython)
  n = 1
  ref = F_element
FEATURE [App::DocumentObjectGroupPython] G4_CESIUM_FLUORIDE  # scripted group (container) (typed FeaturePython)
  Dunit = g/cm3
  Dvalue = 4.115
  Group = -> [Cs_element001,F_element006]
  conduct = 2
  density = 1
  expand = 3
  formula = G4_CESIUM_FLUORIDE
  name = G4_CESIUM_FLUORIDE
  specific = 4
FEATURE [App::DocumentObjectGroupPython] Cs_element002  label="Cs_element : 002"  # scripted group (container) (typed FeaturePython)
  n = 1
  ref = Cs_element
FEATURE [App::DocumentObjectGroupPython] I_element001  label="I_element : 1"  # scripted group (container) (typed FeaturePython)
  n = 1
  ref = I_element
FEATURE [App::DocumentObjectGroupPython] G4_CESIUM_IODIDE  # scripted group (container) (typed FeaturePython)
  Dunit = g/cm3
  Dvalue = 4.51
  Group = -> [Cs_element002,I_element001]
  conduct = 2
  density = 1
  expand = 3
  formula = G4_CESIUM_IODIDE
  name = G4_CESIUM_IODIDE
  specific = 4
FEATURE [App::DocumentObjectGroupPython] C_element028  label="C_element : 013"  # scripted group (container) (typed FeaturePython)
  n = 6
  ref = C_element
FEATURE [App::DocumentObjectGroupPython] H_element025  label="H_element : 013"  # scripted group (container) (typed FeaturePython)
  n = 5
  ref = H_element
FEATURE [App::DocumentObjectGroupPython] Cl_element005  label="Cl_element : 1"  # scripted group (container) (typed FeaturePython)
  n = 1
  ref = Cl_element
FEATURE [App::DocumentObjectGroupPython] G4_CHLOROBENZENE  # scripted group (container) (typed FeaturePython)
  Dunit = g/cm3
  Dvalue = 1.1058
  Group = -> [C_element028,H_element025,Cl_element005]
  conduct = 2
  density = 1
  expand = 3
  formula = G4_CHLOROBENZENE
  name = G4_CHLOROBENZENE
  specific = 4
FEATURE [App::DocumentObjectGroupPython] C_element029  label="C_element : 014"  # scripted group (container) (typed FeaturePython)
  n = 1
  ref = C_element
FEATURE [App::DocumentObjectGroupPython] H_element026  label="H_element : 1"  # scripted group (container) (typed FeaturePython)
  n = 1
  ref = H_element
FEATURE [App::DocumentObjectGroupPython] Cl_element006  label="Cl_element : 3"  # scripted group (container) (typed FeaturePython)
  n = 3
  ref = Cl_element
FEATURE [App::DocumentObjectGroupPython] G4_CHLOROFORM  # scripted group (container) (typed FeaturePython)
  Dunit = g/cm3
  Dvalue = 1.4832
  Group = -> [C_element029,H_element026,Cl_element006]
  conduct = 2
  density = 1
  expand = 3
  formula = G4_CHLOROFORM
  name = G4_CHLOROFORM
  specific = 4
FEATURE [App::DocumentObjectGroupPython] H_element027  label="H_element : 0.010"  # scripted group (container) (typed FeaturePython)
  n = 0.01
FEATURE [App::DocumentObjectGroupPython] C_element030  label="C_element : 0.001"  # scripted group (container) (typed FeaturePython)
  n = 0.001
FEATURE [App::DocumentObjectGroupPython] O_element030  label="O_element : 0.529"  # scripted group (container) (typed FeaturePython)
  n = 0.529107
FEATURE [App::DocumentObjectGroupPython] Na_element005  label="Na_element : 0.016"  # scripted group (container) (typed FeaturePython)
  n = 0.016
FEATURE [App::DocumentObjectGroupPython] Mg_element003  label="Mg_element : 0.004"  # scripted group (container) (typed FeaturePython)
  n = 0.002
FEATURE [App::DocumentObjectGroupPython] Al_element002  label="Al_element : 0.034"  # scripted group (container) (typed FeaturePython)
  n = 0.033872
FEATURE [App::DocumentObjectGroupPython] Si_element002  label="Si_element : 0.337"  # scripted group (container) (typed FeaturePython)
  n = 0.337021
FEATURE [App::DocumentObjectGroupPython] K_element003  label="K_element : 0.013"  # scripted group (container) (typed FeaturePython)
  n = 0.013
FEATURE [App::DocumentObjectGroupPython] Ca_element010  label="Ca_element : 0.044"  # scripted group (container) (typed FeaturePython)
  n = 0.044
FEATURE [App::DocumentObjectGroupPython] Fe_element002  label="Fe_element : 0.014"  # scripted group (container) (typed FeaturePython)
  n = 0.014
FEATURE [App::DocumentObjectGroupPython] G4_CONCRETE  # scripted group (container) (typed FeaturePython)
  Dunit = g/cm3
  Dvalue = 2.3
  Group = -> [H_element027,C_element030,O_element030,Na_element005,Mg_element003,Al_element002,Si_element002,K_element003,Ca_element010,Fe_element002]
  conduct = 2
  density = 1
  expand = 3
  formula = G4_CONCRETE
  name = G4_CONCRETE
  specific = 4
FEATURE [App::DocumentObjectGroupPython] C_element031  label="C_element : 015"  # scripted group (container) (typed FeaturePython)
  n = 6
  ref = C_element
FEATURE [App::DocumentObjectGroupPython] H_element028  label="H_element : 12"  # scripted group (container) (typed FeaturePython)
  n = 12
  ref = H_element
FEATURE [App::DocumentObjectGroupPython] G4_CYCLOHEXANE  # scripted group (container) (typed FeaturePython)
  Dunit = g/cm3
  Dvalue = 0.779
  Group = -> [C_element031,H_element028]
  conduct = 2
  density = 1
  expand = 3
  formula = G4_CYCLOHEXANE
  name = G4_CYCLOHEXANE
  specific = 4
FEATURE [App::DocumentObjectGroupPython] C_element032  label="C_element : 016"  # scripted group (container) (typed FeaturePython)
  n = 6
  ref = C_element
FEATURE [App::DocumentObjectGroupPython] H_element029  label="H_element : 4"  # scripted group (container) (typed FeaturePython)
  n = 4
  ref = H_element
FEATURE [App::DocumentObjectGroupPython] Cl_element007  label="Cl_element : 2"  # scripted group (container) (typed FeaturePython)
  n = 2
  ref = Cl_element
FEATURE [App::DocumentObjectGroupPython] G4_1_2_DICHLOROBENZENE  label="G4_1.2-DICHLOROBENZENE"  # scripted group (container) (typed FeaturePython)
  Dunit = g/cm3
  Dvalue = 1.3048
  Group = -> [C_element032,H_element029,Cl_element007]
  conduct = 2
  density = 1
  expand = 3
  formula = G4_1.2-DICHLOROBENZENE
  name = G4_1.2-DICHLOROBENZENE
  specific = 4
FEATURE [App::DocumentObjectGroupPython] C_element033  label="C_element : 017"  # scripted group (container) (typed FeaturePython)
  n = 4
  ref = C_element
FEATURE [App::DocumentObjectGroupPython] H_element030  label="H_element : 8"  # scripted group (container) (typed FeaturePython)
  n = 8
  ref = H_element
FEATURE [App::DocumentObjectGroupPython] O_element031  label="O_element : 014"  # scripted group (container) (typed FeaturePython)
  n = 1
  ref = O_element
FEATURE [App::DocumentObjectGroupPython] Cl_element008  label="Cl_element : 005"  # scripted group (container) (typed FeaturePython)
  n = 2
  ref = Cl_element
FEATURE [App::DocumentObjectGroupPython] G4_DICHLORODIETHYL_ETHER  # scripted group (container) (typed FeaturePython)
  Dunit = g/cm3
  Dvalue = 1.2199
  Group = -> [C_element033,H_element030,O_element031,Cl_element008]
  conduct = 2
  density = 1
  expand = 3
  formula = G4_DICHLORODIETHYL_ETHER
  name = G4_DICHLORODIETHYL_ETHER
  specific = 4
FEATURE [App::DocumentObjectGroupPython] C_element034  label="C_element : 018"  # scripted group (container) (typed FeaturePython)
  n = 2
  ref = C_element
FEATURE [App::DocumentObjectGroupPython] H_element031  label="H_element : 014"  # scripted group (container) (typed FeaturePython)
  n = 4
  ref = H_element
FEATURE [App::DocumentObjectGroupPython] Cl_element009  label="Cl_element : 006"  # scripted group (container) (typed FeaturePython)
  n = 2
  ref = Cl_element
FEATURE [App::DocumentObjectGroupPython] G4_1_2_DICHLOROETHANE  label="G4_1.2-DICHLOROETHANE"  # scripted group (container) (typed FeaturePython)
  Dunit = g/cm3
  Dvalue = 1.2351
  Group = -> [C_element034,H_element031,Cl_element009]
  conduct = 2
  density = 1
  expand = 3
  formula = G4_1.2-DICHLOROETHANE
  name = G4_1.2-DICHLOROETHANE
  specific = 4
FEATURE [App::DocumentObjectGroupPython] C_element035  label="C_element : 019"  # scripted group (container) (typed FeaturePython)
  n = 4
  ref = C_element
FEATURE [App::DocumentObjectGroupPython] H_element032  label="H_element : 015"  # scripted group (container) (typed FeaturePython)
  n = 10
  ref = H_element
FEATURE [App::DocumentObjectGroupPython] O_element032  label="O_element : 015"  # scripted group (container) (typed FeaturePython)
  n = 1
  ref = O_element
FEATURE [App::DocumentObjectGroupPython] G4_DIETHYL_ETHER  # scripted group (container) (typed FeaturePython)
  Dunit = g/cm3
  Dvalue = 0.71378
  Group = -> [C_element035,H_element032,O_element032]
  conduct = 2
  density = 1
  expand = 3
  formula = G4_DIETHYL_ETHER
  name = G4_DIETHYL_ETHER
  specific = 4
FEATURE [App::DocumentObjectGroupPython] C_element036  label="C_element : 020"  # scripted group (container) (typed FeaturePython)
  n = 3
  ref = C_element
FEATURE [App::DocumentObjectGroupPython] H_element033  label="H_element : 016"  # scripted group (container) (typed FeaturePython)
  n = 7
  ref = H_element
FEATURE [App::DocumentObjectGroupPython] N_element015  label="N_element : 008"  # scripted group (container) (typed FeaturePython)
  n = 1
  ref = N_element
FEATURE [App::DocumentObjectGroupPython] O_element033  label="O_element : 016"  # scripted group (container) (typed FeaturePython)
  n = 1
  ref = O_element
FEATURE [App::DocumentObjectGroupPython] G4_N_N_DIMETHYL_FORMAMIDE  label="G4_N.N-DIMETHYL_FORMAMIDE"  # scripted group (container) (typed FeaturePython)
  Dunit = g/cm3
  Dvalue = 0.9487
  Group = -> [C_element036,H_element033,N_element015,O_element033]
  conduct = 2
  density = 1
  expand = 3
  formula = G4_N.N-DIMETHYL_FORMAMIDE
  name = G4_N.N-DIMETHYL_FORMAMIDE
  specific = 4
FEATURE [App::DocumentObjectGroupPython] C_element037  label="C_element : 021"  # scripted group (container) (typed FeaturePython)
  n = 2
  ref = C_element
FEATURE [App::DocumentObjectGroupPython] H_element034  label="H_element : 017"  # scripted group (container) (typed FeaturePython)
  n = 6
  ref = H_element
FEATURE [App::DocumentObjectGroupPython] O_element034  label="O_element : 017"  # scripted group (container) (typed FeaturePython)
  n = 1
  ref = O_element
FEATURE [App::DocumentObjectGroupPython] S_element009  label="S_element : 003"  # scripted group (container) (typed FeaturePython)
  n = 1
  ref = S_element
FEATURE [App::DocumentObjectGroupPython] G4_DIMETHYL_SULFOXIDE  # scripted group (container) (typed FeaturePython)
  Dunit = g/cm3
  Dvalue = 1.1014
  Group = -> [C_element037,H_element034,O_element034,S_element009]
  conduct = 2
  density = 1
  expand = 3
  formula = G4_DIMETHYL_SULFOXIDE
  name = G4_DIMETHYL_SULFOXIDE
  specific = 4
FEATURE [App::DocumentObjectGroupPython] C_element038  label="C_element : 022"  # scripted group (container) (typed FeaturePython)
  n = 2
  ref = C_element
FEATURE [App::DocumentObjectGroupPython] H_element035  label="H_element : 018"  # scripted group (container) (typed FeaturePython)
  n = 6
  ref = H_element
FEATURE [App::DocumentObjectGroupPython] G4_ETHANE  # scripted group (container) (typed FeaturePython)
  Dunit = g/cm3
  Dvalue = 0.00125324
  Group = -> [C_element038,H_element035]
  conduct = 2
  density = 1
  expand = 3
  formula = G4_ETHANE
  name = G4_ETHANE
  specific = 4
FEATURE [App::DocumentObjectGroupPython] C_element039  label="C_element : 023"  # scripted group (container) (typed FeaturePython)
  n = 2
  ref = C_element
FEATURE [App::DocumentObjectGroupPython] H_element036  label="H_element : 019"  # scripted group (container) (typed FeaturePython)
  n = 6
  ref = H_element
FEATURE [App::DocumentObjectGroupPython] O_element035  label="O_element : 018"  # scripted group (container) (typed FeaturePython)
  n = 1
  ref = O_element
FEATURE [App::DocumentObjectGroupPython] G4_ETHYL_ALCOHOL  # scripted group (container) (typed FeaturePython)
  Dunit = g/cm3
  Dvalue = 0.7893
  Group = -> [C_element039,H_element036,O_element035]
  conduct = 2
  density = 1
  expand = 3
  formula = G4_ETHYL_ALCOHOL
  name = G4_ETHYL_ALCOHOL
  specific = 4
FEATURE [App::DocumentObjectGroupPython] H_element037  label="H_element : 0.090"  # scripted group (container) (typed FeaturePython)
  n = 0.090027
FEATURE [App::DocumentObjectGroupPython] C_element040  label="C_element : 0.585"  # scripted group (container) (typed FeaturePython)
  n = 0.585182
FEATURE [App::DocumentObjectGroupPython] O_element036  label="O_element : 0.325"  # scripted group (container) (typed FeaturePython)
  n = 0.324791
FEATURE [App::DocumentObjectGroupPython] G4_ETHYL_CELLULOSE  # scripted group (container) (typed FeaturePython)
  Dunit = g/cm3
  Dvalue = 1.13
  Group = -> [H_element037,C_element040,O_element036]
  conduct = 2
  density = 1
  expand = 3
  formula = G4_ETHYL_CELLULOSE
  name = G4_ETHYL_CELLULOSE
  specific = 4
FEATURE [App::DocumentObjectGroupPython] C_element041  label="C_element : 024"  # scripted group (container) (typed FeaturePython)
  n = 2
  ref = C_element
FEATURE [App::DocumentObjectGroupPython] H_element038  label="H_element : 020"  # scripted group (container) (typed FeaturePython)
  n = 4
  ref = H_element
FEATURE [App::DocumentObjectGroupPython] G4_ETHYLENE  # scripted group (container) (typed FeaturePython)
  Dunit = g/cm3
  Dvalue = 0.00117497
  Group = -> [C_element041,H_element038]
  conduct = 2
  density = 1
  expand = 3
  formula = G4_ETHYLENE
  name = G4_ETHYLENE
  specific = 4
FEATURE [App::DocumentObjectGroupPython] H_element039  label="H_element : 0.096"  # scripted group (container) (typed FeaturePython)
  n = 0.096
FEATURE [App::DocumentObjectGroupPython] C_element042  label="C_element : 0.195"  # scripted group (container) (typed FeaturePython)
  n = 0.195
FEATURE [App::DocumentObjectGroupPython] N_element016  label="N_element : 0.057"  # scripted group (container) (typed FeaturePython)
  n = 0.057
FEATURE [App::DocumentObjectGroupPython] O_element037  label="O_element : 0.646"  # scripted group (container) (typed FeaturePython)
  n = 0.646
FEATURE [App::DocumentObjectGroupPython] Na_element006  label="Na_element : 0.017"  # scripted group (container) (typed FeaturePython)
  n = 0.001
FEATURE [App::DocumentObjectGroupPython] P_element005  label="P_element : 0.104"  # scripted group (container) (typed FeaturePython)
  n = 0.001
FEATURE [App::DocumentObjectGroupPython] S_element010  label="S_element : 0.016"  # scripted group (container) (typed FeaturePython)
  n = 0.003
FEATURE [App::DocumentObjectGroupPython] Cl_element010  label="Cl_element : 0.005"  # scripted group (container) (typed FeaturePython)
  n = 0.001
FEATURE [App::DocumentObjectGroupPython] G4_EYE_LENS_ICRP  # scripted group (container) (typed FeaturePython)
  Dunit = g/cm3
  Dvalue = 1.07
  Group = -> [H_element039,C_element042,N_element016,O_element037,Na_element006,P_element005,S_element010,Cl_element010]
  conduct = 2
  density = 1
  expand = 3
  formula = G4_EYE_LENS_ICRP
  name = G4_EYE_LENS_ICRP
  specific = 4
FEATURE [App::DocumentObjectGroupPython] Fe_element003  label="Fe_element : 2"  # scripted group (container) (typed FeaturePython)
  n = 2
  ref = Fe_element
FEATURE [App::DocumentObjectGroupPython] O_element038  label="O_element : 019"  # scripted group (container) (typed FeaturePython)
  n = 3
  ref = O_element
FEATURE [App::DocumentObjectGroupPython] G4_FERRIC_OXIDE  # scripted group (container) (typed FeaturePython)
  Dunit = g/cm3
  Dvalue = 5.2
  Group = -> [Fe_element003,O_element038]
  conduct = 2
  density = 1
  expand = 3
  formula = G4_FERRIC_OXIDE
  name = G4_FERRIC_OXIDE
  specific = 4
FEATURE [App::DocumentObjectGroupPython] Fe_element004  label="Fe_element : 1"  # scripted group (container) (typed FeaturePython)
  n = 1
  ref = Fe_element
FEATURE [App::DocumentObjectGroupPython] B_element003  label="B_element : 1"  # scripted group (container) (typed FeaturePython)
  n = 1
  ref = B_element
FEATURE [App::DocumentObjectGroupPython] G4_FERROBORIDE  # scripted group (container) (typed FeaturePython)
  Dunit = g/cm3
  Dvalue = 7.15
  Group = -> [Fe_element004,B_element003]
  conduct = 2
  density = 1
  expand = 3
  formula = G4_FERROBORIDE
  name = G4_FERROBORIDE
  specific = 4
FEATURE [App::DocumentObjectGroupPython] Fe_element005  label="Fe_element : 003"  # scripted group (container) (typed FeaturePython)
  n = 1
  ref = Fe_element
FEATURE [App::DocumentObjectGroupPython] O_element039  label="O_element : 020"  # scripted group (container) (typed FeaturePython)
  n = 1
  ref = O_element
FEATURE [App::DocumentObjectGroupPython] G4_FERROUS_OXIDE  # scripted group (container) (typed FeaturePython)
  Dunit = g/cm3
  Dvalue = 5.7
  Group = -> [Fe_element005,O_element039]
  conduct = 2
  density = 1
  expand = 3
  formula = G4_FERROUS_OXIDE
  name = G4_FERROUS_OXIDE
  specific = 4
FEATURE [App::DocumentObjectGroupPython] H_element040  label="H_element : 0.115"  # scripted group (container) (typed FeaturePython)
  n = 0.108259
FEATURE [App::DocumentObjectGroupPython] N_element017  label="N_element : 0.000"  # scripted group (container) (typed FeaturePython)
  n = 2.7e-05
FEATURE [App::DocumentObjectGroupPython] O_element040  label="O_element : 0.879"  # scripted group (container) (typed FeaturePython)
  n = 0.878636
FEATURE [App::DocumentObjectGroupPython] Na_element007  label="Na_element : 0.000"  # scripted group (container) (typed FeaturePython)
  n = 2.2e-05
FEATURE [App::DocumentObjectGroupPython] S_element011  label="S_element : 0.013"  # scripted group (container) (typed FeaturePython)
  n = 0.012968
FEATURE [App::DocumentObjectGroupPython] Cl_element011  label="Cl_element : 0.000"  # scripted group (container) (typed FeaturePython)
  n = 3.4e-05
FEATURE [App::DocumentObjectGroupPython] Fe_element006  label="Fe_element : 0.000"  # scripted group (container) (typed FeaturePython)
  n = 5.4e-05
FEATURE [App::DocumentObjectGroupPython] G4_FERROUS_SULFATE  # scripted group (container) (typed FeaturePython)
  Dunit = g/cm3
  Dvalue = 1.024
  Group = -> [H_element040,N_element017,O_element040,Na_element007,S_element011,Cl_element011,Fe_element006]
  conduct = 2
  density = 1
  expand = 3
  formula = G4_FERROUS_SULFATE
  name = G4_FERROUS_SULFATE
  specific = 4
FEATURE [App::DocumentObjectGroupPython] C_element043  label="C_element : 0.099"  # scripted group (container) (typed FeaturePython)
  n = 0.099335
FEATURE [App::DocumentObjectGroupPython] F_element007  label="F_element : 0.314"  # scripted group (container) (typed FeaturePython)
  n = 0.314247
FEATURE [App::DocumentObjectGroupPython] Cl_element012  label="Cl_element : 0.586"  # scripted group (container) (typed FeaturePython)
  n = 0.586418
FEATURE [App::DocumentObjectGroupPython] G4_FREON_12  label="G4_FREON-12"  # scripted group (container) (typed FeaturePython)
  Dunit = g/cm3
  Dvalue = 1.12
  Group = -> [C_element043,F_element007,Cl_element012]
  conduct = 2
  density = 1
  expand = 3
  formula = G4_FREON-12
  name = G4_FREON-12
  specific = 4
FEATURE [App::DocumentObjectGroupPython] C_element044  label="C_element : 0.057"  # scripted group (container) (typed FeaturePython)
  n = 0.057245
FEATURE [App::DocumentObjectGroupPython] F_element008  label="F_element : 0.181"  # scripted group (container) (typed FeaturePython)
  n = 0.181096
FEATURE [App::DocumentObjectGroupPython] Br_element001  label="Br_element : 0.762"  # scripted group (container) (typed FeaturePython)
  n = 0.761659
FEATURE [App::DocumentObjectGroupPython] G4_FREON_12B2  label="G4_FREON-12B2"  # scripted group (container) (typed FeaturePython)
  Dunit = g/cm3
  Dvalue = 1.8
  Group = -> [C_element044,F_element008,Br_element001]
  conduct = 2
  density = 1
  expand = 3
  formula = G4_FREON-12B2
  name = G4_FREON-12B2
  specific = 4
FEATURE [App::DocumentObjectGroupPython] C_element045  label="C_element : 0.115"  # scripted group (container) (typed FeaturePython)
  n = 0.114983
FEATURE [App::DocumentObjectGroupPython] F_element009  label="F_element : 0.546"  # scripted group (container) (typed FeaturePython)
  n = 0.545621
FEATURE [App::DocumentObjectGroupPython] Cl_element013  label="Cl_element : 0.339"  # scripted group (container) (typed FeaturePython)
  n = 0.339396
FEATURE [App::DocumentObjectGroupPython] G4_FREON_13  label="G4_FREON-13"  # scripted group (container) (typed FeaturePython)
  Dunit = g/cm3
  Dvalue = 0.95
  Group = -> [C_element045,F_element009,Cl_element013]
  conduct = 2
  density = 1
  expand = 3
  formula = G4_FREON-13
  name = G4_FREON-13
  specific = 4
FEATURE [App::DocumentObjectGroupPython] C_element046  label="C_element : 025"  # scripted group (container) (typed FeaturePython)
  n = 1
  ref = C_element
FEATURE [App::DocumentObjectGroupPython] F_element010  label="F_element : 3"  # scripted group (container) (typed FeaturePython)
  n = 3
  ref = F_element
FEATURE [App::DocumentObjectGroupPython] Br_element002  label="Br_element : 1"  # scripted group (container) (typed FeaturePython)
  n = 1
  ref = Br_element
FEATURE [App::DocumentObjectGroupPython] G4_FREON_13B1  label="G4_FREON-13B1"  # scripted group (container) (typed FeaturePython)
  Dunit = g/cm3
  Dvalue = 1.5
  Group = -> [C_element046,F_element010,Br_element002]
  conduct = 2
  density = 1
  expand = 3
  formula = G4_FREON-13B1
  name = G4_FREON-13B1
  specific = 4
FEATURE [App::DocumentObjectGroupPython] C_element047  label="C_element : 0.061"  # scripted group (container) (typed FeaturePython)
  n = 0.061309
FEATURE [App::DocumentObjectGroupPython] F_element011  label="F_element : 0.291"  # scripted group (container) (typed FeaturePython)
  n = 0.290924
FEATURE [App::DocumentObjectGroupPython] I_element002  label="I_element : 0.648"  # scripted group (container) (typed FeaturePython)
  n = 0.647767
FEATURE [App::DocumentObjectGroupPython] G4_FREON_13I1  label="G4_FREON-13I1"  # scripted group (container) (typed FeaturePython)
  Dunit = g/cm3
  Dvalue = 1.8
  Group = -> [C_element047,F_element011,I_element002]
  conduct = 2
  density = 1
  expand = 3
  formula = G4_FREON-13I1
  name = G4_FREON-13I1
  specific = 4
FEATURE [App::DocumentObjectGroupPython] Gd_element001  label="Gd_element : 2"  # scripted group (container) (typed FeaturePython)
  n = 2
  ref = Gd_element
FEATURE [App::DocumentObjectGroupPython] O_element041  label="O_element : 021"  # scripted group (container) (typed FeaturePython)
  n = 2
  ref = O_element
FEATURE [App::DocumentObjectGroupPython] S_element012  label="S_element : 004"  # scripted group (container) (typed FeaturePython)
  n = 1
  ref = S_element
FEATURE [App::DocumentObjectGroupPython] G4_GADOLINIUM_OXYSULFIDE  # scripted group (container) (typed FeaturePython)
  Dunit = g/cm3
  Dvalue = 7.44
  Group = -> [Gd_element001,O_element041,S_element012]
  conduct = 2
  density = 1
  expand = 3
  formula = G4_GADOLINIUM_OXYSULFIDE
  name = G4_GADOLINIUM_OXYSULFIDE
  specific = 4
FEATURE [App::DocumentObjectGroupPython] Ga_element001  label="Ga_element : 1"  # scripted group (container) (typed FeaturePython)
  n = 1
  ref = Ga_element
FEATURE [App::DocumentObjectGroupPython] As_element001  label="As_element : 1"  # scripted group (container) (typed FeaturePython)
  n = 1
  ref = As_element
FEATURE [App::DocumentObjectGroupPython] G4_GALLIUM_ARSENIDE  # scripted group (container) (typed FeaturePython)
  Dunit = g/cm3
  Dvalue = 5.31
  Group = -> [Ga_element001,As_element001]
  conduct = 2
  density = 1
  expand = 3
  formula = G4_GALLIUM_ARSENIDE
  name = G4_GALLIUM_ARSENIDE
  specific = 4
FEATURE [App::DocumentObjectGroupPython] H_element041  label="H_element : 0.081"  # scripted group (container) (typed FeaturePython)
  n = 0.08118
FEATURE [App::DocumentObjectGroupPython] C_element048  label="C_element : 0.416"  # scripted group (container) (typed FeaturePython)
  n = 0.41606
FEATURE [App::DocumentObjectGroupPython] N_element018  label="N_element : 0.111"  # scripted group (container) (typed FeaturePython)
  n = 0.11124
FEATURE [App::DocumentObjectGroupPython] O_element042  label="O_element : 0.381"  # scripted group (container) (typed FeaturePython)
  n = 0.38064
FEATURE [App::DocumentObjectGroupPython] S_element013  label="S_element : 0.011"  # scripted group (container) (typed FeaturePython)
  n = 0.01088
FEATURE [App::DocumentObjectGroupPython] G4_GEL_PHOTO_EMULSION  # scripted group (container) (typed FeaturePython)
  Dunit = g/cm3
  Dvalue = 1.2914
  Group = -> [H_element041,C_element048,N_element018,O_element042,S_element013]
  conduct = 2
  density = 1
  expand = 3
  formula = G4_GEL_PHOTO_EMULSION
  name = G4_GEL_PHOTO_EMULSION
  specific = 4
FEATURE [App::DocumentObjectGroupPython] B_element004  label="B_element : 0.040"  # scripted group (container) (typed FeaturePython)
  n = 0.0400639
FEATURE [App::DocumentObjectGroupPython] O_element043  label="O_element : 0.540"  # scripted group (container) (typed FeaturePython)
  n = 0.539561
FEATURE [App::DocumentObjectGroupPython] Na_element008  label="Na_element : 0.028"  # scripted group (container) (typed FeaturePython)
  n = 0.0281909
FEATURE [App::DocumentObjectGroupPython] Al_element003  label="Al_element : 0.012"  # scripted group (container) (typed FeaturePython)
  n = 0.011644
FEATURE [App::DocumentObjectGroupPython] Si_element003  label="Si_element : 0.377"  # scripted group (container) (typed FeaturePython)
  n = 0.377219
FEATURE [App::DocumentObjectGroupPython] K_element004  label="K_element : 0.014"  # scripted group (container) (typed FeaturePython)
  n = 0.00332099
FEATURE [App::DocumentObjectGroupPython] G4_Pyrex_Glass  # scripted group (container) (typed FeaturePython)
  Dunit = g/cm3
  Dvalue = 2.23
  Group = -> [B_element004,O_element043,Na_element008,Al_element003,Si_element003,K_element004]
  conduct = 2
  density = 1
  expand = 3
  formula = G4_Pyrex_Glass
  name = G4_Pyrex_Glass
  specific = 4
FEATURE [App::DocumentObjectGroupPython] O_element044  label="O_element : 0.156"  # scripted group (container) (typed FeaturePython)
  n = 0.156453
FEATURE [App::DocumentObjectGroupPython] Si_element004  label="Si_element : 0.081"  # scripted group (container) (typed FeaturePython)
  n = 0.080866
FEATURE [App::DocumentObjectGroupPython] Ti_element001  label="Ti_element : 0.008"  # scripted group (container) (typed FeaturePython)
  n = 0.008092
FEATURE [App::DocumentObjectGroupPython] As_element002  label="As_element : 0.003"  # scripted group (container) (typed FeaturePython)
  n = 0.002651
FEATURE [App::DocumentObjectGroupPython] Pb_element001  label="Pb_element : 0.752"  # scripted group (container) (typed FeaturePython)
  n = 0.751938
FEATURE [App::DocumentObjectGroupPython] G4_GLASS_LEAD  # scripted group (container) (typed FeaturePython)
  Dunit = g/cm3
  Dvalue = 6.22
  Group = -> [O_element044,Si_element004,Ti_element001,As_element002,Pb_element001]
  conduct = 2
  density = 1
  expand = 3
  formula = G4_GLASS_LEAD
  name = G4_GLASS_LEAD
  specific = 4
FEATURE [App::DocumentObjectGroupPython] O_element045  label="O_element : 0.460"  # scripted group (container) (typed FeaturePython)
  n = 0.4598
FEATURE [App::DocumentObjectGroupPython] Na_element009  label="Na_element : 0.096"  # scripted group (container) (typed FeaturePython)
  n = 0.0964411
FEATURE [App::DocumentObjectGroupPython] Si_element005  label="Si_element : 0.378"  # scripted group (container) (typed FeaturePython)
  n = 0.336553
FEATURE [App::DocumentObjectGroupPython] Ca_element011  label="Ca_element : 0.107"  # scripted group (container) (typed FeaturePython)
  n = 0.107205
FEATURE [App::DocumentObjectGroupPython] G4_GLASS_PLATE  # scripted group (container) (typed FeaturePython)
  Dunit = g/cm3
  Dvalue = 2.4
  Group = -> [O_element045,Na_element009,Si_element005,Ca_element011]
  conduct = 2
  density = 1
  expand = 3
  formula = G4_GLASS_PLATE
  name = G4_GLASS_PLATE
  specific = 4
FEATURE [App::DocumentObjectGroupPython] C_element049  label="C_element : 026"  # scripted group (container) (typed FeaturePython)
  n = 5
  ref = C_element
FEATURE [App::DocumentObjectGroupPython] H_element042  label="H_element : 021"  # scripted group (container) (typed FeaturePython)
  n = 10
  ref = H_element
FEATURE [App::DocumentObjectGroupPython] N_element019  label="N_element : 2"  # scripted group (container) (typed FeaturePython)
  n = 2
  ref = N_element
FEATURE [App::DocumentObjectGroupPython] O_element046  label="O_element : 022"  # scripted group (container) (typed FeaturePython)
  n = 3
  ref = O_element
FEATURE [App::DocumentObjectGroupPython] G4_GLUTAMINE  # scripted group (container) (typed FeaturePython)
  Dunit = g/cm3
  Dvalue = 1.46
  Group = -> [C_element049,H_element042,N_element019,O_element046]
  conduct = 2
  density = 1
  expand = 3
  formula = G4_GLUTAMINE
  name = G4_GLUTAMINE
  specific = 4
FEATURE [App::DocumentObjectGroupPython] C_element050  label="C_element : 027"  # scripted group (container) (typed FeaturePython)
  n = 3
  ref = C_element
FEATURE [App::DocumentObjectGroupPython] H_element043  label="H_element : 022"  # scripted group (container) (typed FeaturePython)
  n = 8
  ref = H_element
FEATURE [App::DocumentObjectGroupPython] O_element047  label="O_element : 023"  # scripted group (container) (typed FeaturePython)
  n = 3
  ref = O_element
FEATURE [App::DocumentObjectGroupPython] G4_GLYCEROL  # scripted group (container) (typed FeaturePython)
  Dunit = g/cm3
  Dvalue = 1.2613
  Group = -> [C_element050,H_element043,O_element047]
  conduct = 2
  density = 1
  expand = 3
  formula = G4_GLYCEROL
  name = G4_GLYCEROL
  specific = 4
FEATURE [App::DocumentObjectGroupPython] C_element051  label="C_element : 028"  # scripted group (container) (typed FeaturePython)
  n = 5
  ref = C_element
FEATURE [App::DocumentObjectGroupPython] H_element044  label="H_element : 023"  # scripted group (container) (typed FeaturePython)
  n = 5
  ref = H_element
FEATURE [App::DocumentObjectGroupPython] N_element020  label="N_element : 009"  # scripted group (container) (typed FeaturePython)
  n = 5
  ref = N_element
FEATURE [App::DocumentObjectGroupPython] O_element048  label="O_element : 024"  # scripted group (container) (typed FeaturePython)
  n = 1
  ref = O_element
FEATURE [App::DocumentObjectGroupPython] G4_GUANINE  # scripted group (container) (typed FeaturePython)
  Dunit = g/cm3
  Dvalue = 2.2
  Group = -> [C_element051,H_element044,N_element020,O_element048]
  conduct = 2
  density = 1
  expand = 3
  formula = G4_GUANINE
  name = G4_GUANINE
  specific = 4
FEATURE [App::DocumentObjectGroupPython] Ca_element012  label="Ca_element : 006"  # scripted group (container) (typed FeaturePython)
  n = 1
  ref = Ca_element
FEATURE [App::DocumentObjectGroupPython] S_element014  label="S_element : 005"  # scripted group (container) (typed FeaturePython)
  n = 1
  ref = S_element
FEATURE [App::DocumentObjectGroupPython] O_element049  label="O_element : 6"  # scripted group (container) (typed FeaturePython)
  n = 6
  ref = O_element
FEATURE [App::DocumentObjectGroupPython] H_element045  label="H_element : 024"  # scripted group (container) (typed FeaturePython)
  n = 4
  ref = H_element
FEATURE [App::DocumentObjectGroupPython] G4_GYPSUM  # scripted group (container) (typed FeaturePython)
  Dunit = g/cm3
  Dvalue = 2.32
  Group = -> [Ca_element012,S_element014,O_element049,H_element045]
  conduct = 2
  density = 1
  expand = 3
  formula = G4_GYPSUM
  name = G4_GYPSUM
  specific = 4
FEATURE [App::DocumentObjectGroupPython] C_element052  label="C_element : 7"  # scripted group (container) (typed FeaturePython)
  n = 7
  ref = C_element
FEATURE [App::DocumentObjectGroupPython] H_element046  label="H_element : 16"  # scripted group (container) (typed FeaturePython)
  n = 16
  ref = H_element
FEATURE [App::DocumentObjectGroupPython] G4_N_HEPTANE  label="G4_N-HEPTANE"  # scripted group (container) (typed FeaturePython)
  Dunit = g/cm3
  Dvalue = 0.68376
  Group = -> [C_element052,H_element046]
  conduct = 2
  density = 1
  expand = 3
  formula = G4_N-HEPTANE
  name = G4_N-HEPTANE
  specific = 4
FEATURE [App::DocumentObjectGroupPython] C_element053  label="C_element : 029"  # scripted group (container) (typed FeaturePython)
  n = 6
  ref = C_element
FEATURE [App::DocumentObjectGroupPython] H_element047  label="H_element : 14"  # scripted group (container) (typed FeaturePython)
  n = 14
  ref = H_element
FEATURE [App::DocumentObjectGroupPython] G4_N_HEXANE  label="G4_N-HEXANE"  # scripted group (container) (typed FeaturePython)
  Dunit = g/cm3
  Dvalue = 0.6603
  Group = -> [C_element053,H_element047]
  conduct = 2
  density = 1
  expand = 3
  formula = G4_N-HEXANE
  name = G4_N-HEXANE
  specific = 4
FEATURE [App::DocumentObjectGroupPython] C_element054  label="C_element : 22"  # scripted group (container) (typed FeaturePython)
  n = 22
  ref = C_element
FEATURE [App::DocumentObjectGroupPython] H_element048  label="H_element : 025"  # scripted group (container) (typed FeaturePython)
  n = 10
  ref = H_element
FEATURE [App::DocumentObjectGroupPython] N_element021  label="N_element : 010"  # scripted group (container) (typed FeaturePython)
  n = 2
  ref = N_element
FEATURE [App::DocumentObjectGroupPython] O_element050  label="O_element : 025"  # scripted group (container) (typed FeaturePython)
  n = 5
  ref = O_element
FEATURE [App::DocumentObjectGroupPython] G4_KAPTON  # scripted group (container) (typed FeaturePython)
  Dunit = g/cm3
  Dvalue = 1.42
  Group = -> [C_element054,H_element048,N_element021,O_element050]
  conduct = 2
  density = 1
  expand = 3
  formula = G4_KAPTON
  name = G4_KAPTON
  specific = 4
FEATURE [App::DocumentObjectGroupPython] La_element001  label="La_element : 1"  # scripted group (container) (typed FeaturePython)
  n = 1
  ref = La_element
FEATURE [App::DocumentObjectGroupPython] Br_element003  label="Br_element : 002"  # scripted group (container) (typed FeaturePython)
  n = 1
  ref = Br_element
FEATURE [App::DocumentObjectGroupPython] O_element051  label="O_element : 026"  # scripted group (container) (typed FeaturePython)
  n = 1
  ref = O_element
FEATURE [App::DocumentObjectGroupPython] G4_LANTHANUM_OXYBROMIDE  # scripted group (container) (typed FeaturePython)
  Dunit = g/cm3
  Dvalue = 6.28
  Group = -> [La_element001,Br_element003,O_element051]
  conduct = 2
  density = 1
  expand = 3
  formula = G4_LANTHANUM_OXYBROMIDE
  name = G4_LANTHANUM_OXYBROMIDE
  specific = 4
FEATURE [App::DocumentObjectGroupPython] La_element002  label="La_element : 2"  # scripted group (container) (typed FeaturePython)
  n = 2
  ref = La_element
FEATURE [App::DocumentObjectGroupPython] O_element052  label="O_element : 027"  # scripted group (container) (typed FeaturePython)
  n = 2
  ref = O_element
FEATURE [App::DocumentObjectGroupPython] S_element015  label="S_element : 006"  # scripted group (container) (typed FeaturePython)
  n = 1
  ref = S_element
FEATURE [App::DocumentObjectGroupPython] G4_LANTHANUM_OXYSULFIDE  # scripted group (container) (typed FeaturePython)
  Dunit = g/cm3
  Dvalue = 5.86
  Group = -> [La_element002,O_element052,S_element015]
  conduct = 2
  density = 1
  expand = 3
  formula = G4_LANTHANUM_OXYSULFIDE
  name = G4_LANTHANUM_OXYSULFIDE
  specific = 4
FEATURE [App::DocumentObjectGroupPython] O_element053  label="O_element : 0.072"  # scripted group (container) (typed FeaturePython)
  n = 0.071682
FEATURE [App::DocumentObjectGroupPython] Pb_element002  label="Pb_element : 0.928"  # scripted group (container) (typed FeaturePython)
  n = 0.928318
FEATURE [App::DocumentObjectGroupPython] G4_LEAD_OXIDE  # scripted group (container) (typed FeaturePython)
  Dunit = g/cm3
  Dvalue = 9.53
  Group = -> [O_element053,Pb_element002]
  conduct = 2
  density = 1
  expand = 3
  formula = G4_LEAD_OXIDE
  name = G4_LEAD_OXIDE
  specific = 4
FEATURE [App::DocumentObjectGroupPython] Li_element001  label="Li_element : 1"  # scripted group (container) (typed FeaturePython)
  n = 1
  ref = Li_element
FEATURE [App::DocumentObjectGroupPython] N_element022  label="N_element : 011"  # scripted group (container) (typed FeaturePython)
  n = 1
  ref = N_element
FEATURE [App::DocumentObjectGroupPython] H_element049  label="H_element : 026"  # scripted group (container) (typed FeaturePython)
  n = 2
  ref = H_element
FEATURE [App::DocumentObjectGroupPython] G4_LITHIUM_AMIDE  # scripted group (container) (typed FeaturePython)
  Dunit = g/cm3
  Dvalue = 1.178
  Group = -> [Li_element001,N_element022,H_element049]
  conduct = 2
  density = 1
  expand = 3
  formula = G4_LITHIUM_AMIDE
  name = G4_LITHIUM_AMIDE
  specific = 4
FEATURE [App::DocumentObjectGroupPython] Li_element002  label="Li_element : 2"  # scripted group (container) (typed FeaturePython)
  n = 2
  ref = Li_element
FEATURE [App::DocumentObjectGroupPython] C_element055  label="C_element : 030"  # scripted group (container) (typed FeaturePython)
  n = 1
  ref = C_element
FEATURE [App::DocumentObjectGroupPython] O_element054  label="O_element : 028"  # scripted group (container) (typed FeaturePython)
  n = 3
  ref = O_element
FEATURE [App::DocumentObjectGroupPython] G4_LITHIUM_CARBONATE  # scripted group (container) (typed FeaturePython)
  Dunit = g/cm3
  Dvalue = 2.11
  Group = -> [Li_element002,C_element055,O_element054]
  conduct = 2
  density = 1
  expand = 3
  formula = G4_LITHIUM_CARBONATE
  name = G4_LITHIUM_CARBONATE
  specific = 4
FEATURE [App::DocumentObjectGroupPython] Li_element003  label="Li_element : 003"  # scripted group (container) (typed FeaturePython)
  n = 1
  ref = Li_element
FEATURE [App::DocumentObjectGroupPython] F_element012  label="F_element : 004"  # scripted group (container) (typed FeaturePython)
  n = 1
  ref = F_element
FEATURE [App::DocumentObjectGroupPython] G4_LITHIUM_FLUORIDE  # scripted group (container) (typed FeaturePython)
  Dunit = g/cm3
  Dvalue = 2.635
  Group = -> [Li_element003,F_element012]
  conduct = 2
  density = 1
  expand = 3
  formula = G4_LITHIUM_FLUORIDE
  name = G4_LITHIUM_FLUORIDE
  specific = 4
FEATURE [App::DocumentObjectGroupPython] Li_element004  label="Li_element : 004"  # scripted group (container) (typed FeaturePython)
  n = 1
  ref = Li_element
FEATURE [App::DocumentObjectGroupPython] H_element050  label="H_element : 027"  # scripted group (container) (typed FeaturePython)
  n = 1
  ref = H_element
FEATURE [App::DocumentObjectGroupPython] G4_LITHIUM_HYDRIDE  # scripted group (container) (typed FeaturePython)
  Dunit = g/cm3
  Dvalue = 0.82
  Group = -> [Li_element004,H_element050]
  conduct = 2
  density = 1
  expand = 3
  formula = G4_LITHIUM_HYDRIDE
  name = G4_LITHIUM_HYDRIDE
  specific = 4
FEATURE [App::DocumentObjectGroupPython] Li_element005  label="Li_element : 005"  # scripted group (container) (typed FeaturePython)
  n = 1
  ref = Li_element
FEATURE [App::DocumentObjectGroupPython] I_element003  label="I_element : 002"  # scripted group (container) (typed FeaturePython)
  n = 1
  ref = I_element
FEATURE [App::DocumentObjectGroupPython] G4_LITHIUM_IODIDE  # scripted group (container) (typed FeaturePython)
  Dunit = g/cm3
  Dvalue = 3.494
  Group = -> [Li_element005,I_element003]
  conduct = 2
  density = 1
  expand = 3
  formula = G4_LITHIUM_IODIDE
  name = G4_LITHIUM_IODIDE
  specific = 4
FEATURE [App::DocumentObjectGroupPython] Li_element006  label="Li_element : 006"  # scripted group (container) (typed FeaturePython)
  n = 2
  ref = Li_element
FEATURE [App::DocumentObjectGroupPython] O_element055  label="O_element : 029"  # scripted group (container) (typed FeaturePython)
  n = 1
  ref = O_element
FEATURE [App::DocumentObjectGroupPython] G4_LITHIUM_OXIDE  # scripted group (container) (typed FeaturePython)
  Dunit = g/cm3
  Dvalue = 2.013
  Group = -> [Li_element006,O_element055]
  conduct = 2
  density = 1
  expand = 3
  formula = G4_LITHIUM_OXIDE
  name = G4_LITHIUM_OXIDE
  specific = 4
FEATURE [App::DocumentObjectGroupPython] Li_element007  label="Li_element : 007"  # scripted group (container) (typed FeaturePython)
  n = 2
  ref = Li_element
FEATURE [App::DocumentObjectGroupPython] B_element005  label="B_element : 005"  # scripted group (container) (typed FeaturePython)
  n = 4
  ref = B_element
FEATURE [App::DocumentObjectGroupPython] O_element056  label="O_element : 7"  # scripted group (container) (typed FeaturePython)
  n = 7
  ref = O_element
FEATURE [App::DocumentObjectGroupPython] G4_LITHIUM_TETRABORATE  # scripted group (container) (typed FeaturePython)
  Dunit = g/cm3
  Dvalue = 2.44
  Group = -> [Li_element007,B_element005,O_element056]
  conduct = 2
  density = 1
  expand = 3
  formula = G4_LITHIUM_TETRABORATE
  name = G4_LITHIUM_TETRABORATE
  specific = 4
FEATURE [App::DocumentObjectGroupPython] H_element051  label="H_element : 0.105"  # scripted group (container) (typed FeaturePython)
  n = 0.105
FEATURE [App::DocumentObjectGroupPython] C_element056  label="C_element : 0.083"  # scripted group (container) (typed FeaturePython)
  n = 0.083
FEATURE [App::DocumentObjectGroupPython] N_element023  label="N_element : 0.023"  # scripted group (container) (typed FeaturePython)
  n = 0.023
FEATURE [App::DocumentObjectGroupPython] O_element057  label="O_element : 0.779"  # scripted group (container) (typed FeaturePython)
  n = 0.779
FEATURE [App::DocumentObjectGroupPython] Na_element010  label="Na_element : 0.097"  # scripted group (container) (typed FeaturePython)
  n = 0.002
FEATURE [App::DocumentObjectGroupPython] P_element006  label="P_element : 0.105"  # scripted group (container) (typed FeaturePython)
  n = 0.001
FEATURE [App::DocumentObjectGroupPython] S_element016  label="S_element : 0.017"  # scripted group (container) (typed FeaturePython)
  n = 0.002
FEATURE [App::DocumentObjectGroupPython] Cl_element014  label="Cl_element : 0.587"  # scripted group (container) (typed FeaturePython)
  n = 0.003
FEATURE [App::DocumentObjectGroupPython] K_element005  label="K_element : 0.015"  # scripted group (container) (typed FeaturePython)
  n = 0.002
FEATURE [App::DocumentObjectGroupPython] G4_LUNG_ICRP  # scripted group (container) (typed FeaturePython)
  Dunit = g/cm3
  Dvalue = 1.04
  Group = -> [H_element051,C_element056,N_element023,O_element057,Na_element010,P_element006,S_element016,Cl_element014,K_element005]
  conduct = 2
  density = 1
  expand = 3
  formula = G4_LUNG_ICRP
  name = G4_LUNG_ICRP
  specific = 4
FEATURE [App::DocumentObjectGroupPython] H_element052  label="H_element : 0.116"  # scripted group (container) (typed FeaturePython)
  n = 0.114318
FEATURE [App::DocumentObjectGroupPython] C_element057  label="C_element : 0.656"  # scripted group (container) (typed FeaturePython)
  n = 0.655824
FEATURE [App::DocumentObjectGroupPython] O_element058  label="O_element : 0.092"  # scripted group (container) (typed FeaturePython)
  n = 0.0921831
FEATURE [App::DocumentObjectGroupPython] Mg_element004  label="Mg_element : 0.135"  # scripted group (container) (typed FeaturePython)
  n = 0.134792
FEATURE [App::DocumentObjectGroupPython] Ca_element013  label="Ca_element : 0.003"  # scripted group (container) (typed FeaturePython)
  n = 0.002883
FEATURE [App::DocumentObjectGroupPython] G4_M3_WAX  # scripted group (container) (typed FeaturePython)
  Dunit = g/cm3
  Dvalue = 1.05
  Group = -> [H_element052,C_element057,O_element058,Mg_element004,Ca_element013]
  conduct = 2
  density = 1
  expand = 3
  formula = G4_M3_WAX
  name = G4_M3_WAX
  specific = 4
FEATURE [App::DocumentObjectGroupPython] Mg_element005  label="Mg_element : 1"  # scripted group (container) (typed FeaturePython)
  n = 1
  ref = Mg_element
FEATURE [App::DocumentObjectGroupPython] C_element058  label="C_element : 031"  # scripted group (container) (typed FeaturePython)
  n = 1
  ref = C_element
FEATURE [App::DocumentObjectGroupPython] O_element059  label="O_element : 030"  # scripted group (container) (typed FeaturePython)
  n = 3
  ref = O_element
FEATURE [App::DocumentObjectGroupPython] G4_MAGNESIUM_CARBONATE  # scripted group (container) (typed FeaturePython)
  Dunit = g/cm3
  Dvalue = 2.958
  Group = -> [Mg_element005,C_element058,O_element059]
  conduct = 2
  density = 1
  expand = 3
  formula = G4_MAGNESIUM_CARBONATE
  name = G4_MAGNESIUM_CARBONATE
  specific = 4
FEATURE [App::DocumentObjectGroupPython] Mg_element006  label="Mg_element : 002"  # scripted group (container) (typed FeaturePython)
  n = 1
  ref = Mg_element
FEATURE [App::DocumentObjectGroupPython] F_element013  label="F_element : 005"  # scripted group (container) (typed FeaturePython)
  n = 2
  ref = F_element
FEATURE [App::DocumentObjectGroupPython] G4_MAGNESIUM_FLUORIDE  # scripted group (container) (typed FeaturePython)
  Dunit = g/cm3
  Dvalue = 3
  Group = -> [Mg_element006,F_element013]
  conduct = 2
  density = 1
  expand = 3
  formula = G4_MAGNESIUM_FLUORIDE
  name = G4_MAGNESIUM_FLUORIDE
  specific = 4
FEATURE [App::DocumentObjectGroupPython] Mg_element007  label="Mg_element : 003"  # scripted group (container) (typed FeaturePython)
  n = 1
  ref = Mg_element
FEATURE [App::DocumentObjectGroupPython] O_element060  label="O_element : 031"  # scripted group (container) (typed FeaturePython)
  n = 1
  ref = O_element
FEATURE [App::DocumentObjectGroupPython] G4_MAGNESIUM_OXIDE  # scripted group (container) (typed FeaturePython)
  Dunit = g/cm3
  Dvalue = 3.58
  Group = -> [Mg_element007,O_element060]
  conduct = 2
  density = 1
  expand = 3
  formula = G4_MAGNESIUM_OXIDE
  name = G4_MAGNESIUM_OXIDE
  specific = 4
FEATURE [App::DocumentObjectGroupPython] Mg_element008  label="Mg_element : 004"  # scripted group (container) (typed FeaturePython)
  n = 1
  ref = Mg_element
FEATURE [App::DocumentObjectGroupPython] B_element006  label="B_element : 006"  # scripted group (container) (typed FeaturePython)
  n = 4
  ref = B_element
FEATURE [App::DocumentObjectGroupPython] O_element061  label="O_element : 032"  # scripted group (container) (typed FeaturePython)
  n = 7
  ref = O_element
FEATURE [App::DocumentObjectGroupPython] G4_MAGNESIUM_TETRABORATE  # scripted group (container) (typed FeaturePython)
  Dunit = g/cm3
  Dvalue = 2.53
  Group = -> [Mg_element008,B_element006,O_element061]
  conduct = 2
  density = 1
  expand = 3
  formula = G4_MAGNESIUM_TETRABORATE
  name = G4_MAGNESIUM_TETRABORATE
  specific = 4
FEATURE [App::DocumentObjectGroupPython] Hg_element001  label="Hg_element : 1"  # scripted group (container) (typed FeaturePython)
  n = 1
  ref = Hg_element
FEATURE [App::DocumentObjectGroupPython] I_element004  label="I_element : 2"  # scripted group (container) (typed FeaturePython)
  n = 2
  ref = I_element
FEATURE [App::DocumentObjectGroupPython] G4_MERCURIC_IODIDE  # scripted group (container) (typed FeaturePython)
  Dunit = g/cm3
  Dvalue = 6.36
  Group = -> [Hg_element001,I_element004]
  conduct = 2
  density = 1
  expand = 3
  formula = G4_MERCURIC_IODIDE
  name = G4_MERCURIC_IODIDE
  specific = 4
FEATURE [App::DocumentObjectGroupPython] C_element059  label="C_element : 032"  # scripted group (container) (typed FeaturePython)
  n = 1
  ref = C_element
FEATURE [App::DocumentObjectGroupPython] H_element053  label="H_element : 028"  # scripted group (container) (typed FeaturePython)
  n = 4
  ref = H_element
FEATURE [App::DocumentObjectGroupPython] G4_METHANE  # scripted group (container) (typed FeaturePython)
  Dunit = g/cm3
  Dvalue = 0.000667151
  Group = -> [C_element059,H_element053]
  conduct = 2
  density = 1
  expand = 3
  formula = G4_METHANE
  name = G4_METHANE
  specific = 4
FEATURE [App::DocumentObjectGroupPython] C_element060  label="C_element : 033"  # scripted group (container) (typed FeaturePython)
  n = 1
  ref = C_element
FEATURE [App::DocumentObjectGroupPython] H_element054  label="H_element : 029"  # scripted group (container) (typed FeaturePython)
  n = 4
  ref = H_element
FEATURE [App::DocumentObjectGroupPython] O_element062  label="O_element : 033"  # scripted group (container) (typed FeaturePython)
  n = 1
  ref = O_element
FEATURE [App::DocumentObjectGroupPython] G4_METHANOL  # scripted group (container) (typed FeaturePython)
  Dunit = g/cm3
  Dvalue = 0.7914
  Group = -> [C_element060,H_element054,O_element062]
  conduct = 2
  density = 1
  expand = 3
  formula = G4_METHANOL
  name = G4_METHANOL
  specific = 4
FEATURE [App::DocumentObjectGroupPython] H_element055  label="H_element : 0.134"  # scripted group (container) (typed FeaturePython)
  n = 0.13404
FEATURE [App::DocumentObjectGroupPython] C_element061  label="C_element : 0.778"  # scripted group (container) (typed FeaturePython)
  n = 0.77796
FEATURE [App::DocumentObjectGroupPython] O_element063  label="O_element : 0.035"  # scripted group (container) (typed FeaturePython)
  n = 0.03502
FEATURE [App::DocumentObjectGroupPython] Mg_element009  label="Mg_element : 0.039"  # scripted group (container) (typed FeaturePython)
  n = 0.038594
FEATURE [App::DocumentObjectGroupPython] Ti_element002  label="Ti_element : 0.014"  # scripted group (container) (typed FeaturePython)
  n = 0.014386
FEATURE [App::DocumentObjectGroupPython] G4_MIX_D_WAX  # scripted group (container) (typed FeaturePython)
  Dunit = g/cm3
  Dvalue = 0.99
  Group = -> [H_element055,C_element061,O_element063,Mg_element009,Ti_element002]
  conduct = 2
  density = 1
  expand = 3
  formula = G4_MIX_D_WAX
  name = G4_MIX_D_WAX
  specific = 4
FEATURE [App::DocumentObjectGroupPython] H_element056  label="H_element : 0.135"  # scripted group (container) (typed FeaturePython)
  n = 0.081192
FEATURE [App::DocumentObjectGroupPython] C_element062  label="C_element : 0.583"  # scripted group (container) (typed FeaturePython)
  n = 0.583442
FEATURE [App::DocumentObjectGroupPython] N_element024  label="N_element : 0.018"  # scripted group (container) (typed FeaturePython)
  n = 0.017798
FEATURE [App::DocumentObjectGroupPython] O_element064  label="O_element : 0.186"  # scripted group (container) (typed FeaturePython)
  n = 0.186381
FEATURE [App::DocumentObjectGroupPython] Mg_element010  label="Mg_element : 0.130"  # scripted group (container) (typed FeaturePython)
  n = 0.130287
FEATURE [App::DocumentObjectGroupPython] Cl_element015  label="Cl_element : 0.588"  # scripted group (container) (typed FeaturePython)
  n = 0.0009
FEATURE [App::DocumentObjectGroupPython] G4_MS20_TISSUE  # scripted group (container) (typed FeaturePython)
  Dunit = g/cm3
  Dvalue = 1
  Group = -> [H_element056,C_element062,N_element024,O_element064,Mg_element010,Cl_element015]
  conduct = 2
  density = 1
  expand = 3
  formula = G4_MS20_TISSUE
  name = G4_MS20_TISSUE
  specific = 4
FEATURE [App::DocumentObjectGroupPython] H_element057  label="H_element : 0.136"  # scripted group (container) (typed FeaturePython)
  n = 0.102
FEATURE [App::DocumentObjectGroupPython] C_element063  label="C_element : 0.143"  # scripted group (container) (typed FeaturePython)
  n = 0.143
FEATURE [App::DocumentObjectGroupPython] N_element025  label="N_element : 0.034"  # scripted group (container) (typed FeaturePython)
  n = 0.034
FEATURE [App::DocumentObjectGroupPython] O_element065  label="O_element : 0.710"  # scripted group (container) (typed FeaturePython)
  n = 0.71
FEATURE [App::DocumentObjectGroupPython] Na_element011  label="Na_element : 0.098"  # scripted group (container) (typed FeaturePython)
  n = 0.001
FEATURE [App::DocumentObjectGroupPython] P_element007  label="P_element : 0.002"  # scripted group (container) (typed FeaturePython)
  n = 0.002
FEATURE [App::DocumentObjectGroupPython] S_element017  label="S_element : 0.018"  # scripted group (container) (typed FeaturePython)
  n = 0.003
FEATURE [App::DocumentObjectGroupPython] Cl_element016  label="Cl_element : 0.589"  # scripted group (container) (typed FeaturePython)
  n = 0.001
FEATURE [App::DocumentObjectGroupPython] K_element006  label="K_element : 0.004"  # scripted group (container) (typed FeaturePython)
  n = 0.004
FEATURE [App::DocumentObjectGroupPython] G4_MUSCLE_SKELETAL_ICRP  # scripted group (container) (typed FeaturePython)
  Dunit = g/cm3
  Dvalue = 1.05
  Group = -> [H_element057,C_element063,N_element025,O_element065,Na_element011,P_element007,S_element017,Cl_element016,K_element006]
  conduct = 2
  density = 1
  expand = 3
  formula = G4_MUSCLE_SKELETAL_ICRP
  name = G4_MUSCLE_SKELETAL_ICRP
  specific = 4
FEATURE [App::DocumentObjectGroupPython] H_element058  label="H_element : 0.137"  # scripted group (container) (typed FeaturePython)
  n = 0.102102
FEATURE [App::DocumentObjectGroupPython] C_element064  label="C_element : 0.123"  # scripted group (container) (typed FeaturePython)
  n = 0.123123
FEATURE [App::DocumentObjectGroupPython] N_element026  label="N_element : 0.756"  # scripted group (container) (typed FeaturePython)
  n = 0.035035
FEATURE [App::DocumentObjectGroupPython] O_element066  label="O_element : 0.730"  # scripted group (container) (typed FeaturePython)
  n = 0.72973
FEATURE [App::DocumentObjectGroupPython] Na_element012  label="Na_element : 0.099"  # scripted group (container) (typed FeaturePython)
  n = 0.001001
FEATURE [App::DocumentObjectGroupPython] P_element008  label="P_element : 0.106"  # scripted group (container) (typed FeaturePython)
  n = 0.002002
FEATURE [App::DocumentObjectGroupPython] S_element018  label="S_element : 0.019"  # scripted group (container) (typed FeaturePython)
  n = 0.004004
FEATURE [App::DocumentObjectGroupPython] K_element007  label="K_element : 0.016"  # scripted group (container) (typed FeaturePython)
  n = 0.003003
FEATURE [App::DocumentObjectGroupPython] G4_MUSCLE_STRIATED_ICRU  # scripted group (container) (typed FeaturePython)
  Dunit = g/cm3
  Dvalue = 1.04
  Group = -> [H_element058,C_element064,N_element026,O_element066,Na_element012,P_element008,S_element018,K_element007]
  conduct = 2
  density = 1
  expand = 3
  formula = G4_MUSCLE_STRIATED_ICRU
  name = G4_MUSCLE_STRIATED_ICRU
  specific = 4
FEATURE [App::DocumentObjectGroupPython] H_element059  label="H_element : 0.098"  # scripted group (container) (typed FeaturePython)
  n = 0.0982341
FEATURE [App::DocumentObjectGroupPython] C_element065  label="C_element : 0.156"  # scripted group (container) (typed FeaturePython)
  n = 0.156214
FEATURE [App::DocumentObjectGroupPython] N_element027  label="N_element : 0.757"  # scripted group (container) (typed FeaturePython)
  n = 0.035451
FEATURE [App::DocumentObjectGroupPython] O_element067  label="O_element : 0.880"  # scripted group (container) (typed FeaturePython)
  n = 0.710101
FEATURE [App::DocumentObjectGroupPython] G4_MUSCLE_WITH_SUCROSE  # scripted group (container) (typed FeaturePython)
  Dunit = g/cm3
  Dvalue = 1.11
  Group = -> [H_element059,C_element065,N_element027,O_element067]
  conduct = 2
  density = 1
  expand = 3
  formula = G4_MUSCLE_WITH_SUCROSE
  name = G4_MUSCLE_WITH_SUCROSE
  specific = 4
FEATURE [App::DocumentObjectGroupPython] H_element060  label="H_element : 0.138"  # scripted group (container) (typed FeaturePython)
  n = 0.101969
FEATURE [App::DocumentObjectGroupPython] C_element066  label="C_element : 0.120"  # scripted group (container) (typed FeaturePython)
  n = 0.120058
FEATURE [App::DocumentObjectGroupPython] N_element028  label="N_element : 0.758"  # scripted group (container) (typed FeaturePython)
  n = 0.035451
FEATURE [App::DocumentObjectGroupPython] O_element068  label="O_element : 0.743"  # scripted group (container) (typed FeaturePython)
  n = 0.742522
FEATURE [App::DocumentObjectGroupPython] G4_MUSCLE_WITHOUT_SUCROSE  # scripted group (container) (typed FeaturePython)
  Dunit = g/cm3
  Dvalue = 1.07
  Group = -> [H_element060,C_element066,N_element028,O_element068]
  conduct = 2
  density = 1
  expand = 3
  formula = G4_MUSCLE_WITHOUT_SUCROSE
  name = G4_MUSCLE_WITHOUT_SUCROSE
  specific = 4
FEATURE [App::DocumentObjectGroupPython] C_element067  label="C_element : 10"  # scripted group (container) (typed FeaturePython)
  n = 10
  ref = C_element
FEATURE [App::DocumentObjectGroupPython] H_element061  label="H_element : 030"  # scripted group (container) (typed FeaturePython)
  n = 8
  ref = H_element
FEATURE [App::DocumentObjectGroupPython] G4_NAPHTHALENE  # scripted group (container) (typed FeaturePython)
  Dunit = g/cm3
  Dvalue = 1.145
  Group = -> [C_element067,H_element061]
  conduct = 2
  density = 1
  expand = 3
  formula = G4_NAPHTHALENE
  name = G4_NAPHTHALENE
  specific = 4
FEATURE [App::DocumentObjectGroupPython] C_element068  label="C_element : 034"  # scripted group (container) (typed FeaturePython)
  n = 6
  ref = C_element
FEATURE [App::DocumentObjectGroupPython] H_element062  label="H_element : 031"  # scripted group (container) (typed FeaturePython)
  n = 5
  ref = H_element
FEATURE [App::DocumentObjectGroupPython] N_element029  label="N_element : 012"  # scripted group (container) (typed FeaturePython)
  n = 1
  ref = N_element
FEATURE [App::DocumentObjectGroupPython] O_element069  label="O_element : 034"  # scripted group (container) (typed FeaturePython)
  n = 2
  ref = O_element
FEATURE [App::DocumentObjectGroupPython] G4_NITROBENZENE  # scripted group (container) (typed FeaturePython)
  Dunit = g/cm3
  Dvalue = 1.19867
  Group = -> [C_element068,H_element062,N_element029,O_element069]
  conduct = 2
  density = 1
  expand = 3
  formula = G4_NITROBENZENE
  name = G4_NITROBENZENE
  specific = 4
FEATURE [App::DocumentObjectGroupPython] N_element030  label="N_element : 013"  # scripted group (container) (typed FeaturePython)
  n = 2
  ref = N_element
FEATURE [App::DocumentObjectGroupPython] O_element070  label="O_element : 035"  # scripted group (container) (typed FeaturePython)
  n = 1
  ref = O_element
FEATURE [App::DocumentObjectGroupPython] G4_NITROUS_OXIDE  # scripted group (container) (typed FeaturePython)
  Dunit = g/cm3
  Dvalue = 0.00183094
  Group = -> [N_element030,O_element070]
  conduct = 2
  density = 1
  expand = 3
  formula = G4_NITROUS_OXIDE
  name = G4_NITROUS_OXIDE
  specific = 4
FEATURE [App::DocumentObjectGroupPython] H_element063  label="H_element : 0.104"  # scripted group (container) (typed FeaturePython)
  n = 0.103509
FEATURE [App::DocumentObjectGroupPython] C_element069  label="C_element : 0.648"  # scripted group (container) (typed FeaturePython)
  n = 0.648416
FEATURE [App::DocumentObjectGroupPython] N_element031  label="N_element : 0.100"  # scripted group (container) (typed FeaturePython)
  n = 0.0995361
FEATURE [App::DocumentObjectGroupPython] O_element071  label="O_element : 0.149"  # scripted group (container) (typed FeaturePython)
  n = 0.148539
FEATURE [App::DocumentObjectGroupPython] G4_NYLON_8062  label="G4_NYLON-8062"  # scripted group (container) (typed FeaturePython)
  Dunit = g/cm3
  Dvalue = 1.08
  Group = -> [H_element063,C_element069,N_element031,O_element071]
  conduct = 2
  density = 1
  expand = 3
  formula = G4_NYLON-8062
  name = G4_NYLON-8062
  specific = 4
FEATURE [App::DocumentObjectGroupPython] C_element070  label="C_element : 035"  # scripted group (container) (typed FeaturePython)
  n = 6
  ref = C_element
FEATURE [App::DocumentObjectGroupPython] H_element064  label="H_element : 11"  # scripted group (container) (typed FeaturePython)
  n = 11
  ref = H_element
FEATURE [App::DocumentObjectGroupPython] N_element032  label="N_element : 014"  # scripted group (container) (typed FeaturePython)
  n = 1
  ref = N_element
FEATURE [App::DocumentObjectGroupPython] O_element072  label="O_element : 036"  # scripted group (container) (typed FeaturePython)
  n = 1
  ref = O_element
FEATURE [App::DocumentObjectGroupPython] G4_NYLON_6_6  label="G4_NYLON-6-6"  # scripted group (container) (typed FeaturePython)
  Dunit = g/cm3
  Dvalue = 1.14
  Group = -> [C_element070,H_element064,N_element032,O_element072]
  conduct = 2
  density = 1
  expand = 3
  formula = G4_NYLON-6-6
  name = G4_NYLON-6-6
  specific = 4
FEATURE [App::DocumentObjectGroupPython] H_element065  label="H_element : 0.139"  # scripted group (container) (typed FeaturePython)
  n = 0.107062
FEATURE [App::DocumentObjectGroupPython] C_element071  label="C_element : 0.680"  # scripted group (container) (typed FeaturePython)
  n = 0.680449
FEATURE [App::DocumentObjectGroupPython] N_element033  label="N_element : 0.099"  # scripted group (container) (typed FeaturePython)
  n = 0.099189
FEATURE [App::DocumentObjectGroupPython] O_element073  label="O_element : 0.113"  # scripted group (container) (typed FeaturePython)
  n = 0.1133
FEATURE [App::DocumentObjectGroupPython] G4_NYLON_6_10  label="G4_NYLON-6-10"  # scripted group (container) (typed FeaturePython)
  Dunit = g/cm3
  Dvalue = 1.14
  Group = -> [H_element065,C_element071,N_element033,O_element073]
  conduct = 2
  density = 1
  expand = 3
  formula = G4_NYLON-6-10
  name = G4_NYLON-6-10
  specific = 4
FEATURE [App::DocumentObjectGroupPython] H_element066  label="H_element : 0.140"  # scripted group (container) (typed FeaturePython)
  n = 0.115476
FEATURE [App::DocumentObjectGroupPython] C_element072  label="C_element : 0.721"  # scripted group (container) (typed FeaturePython)
  n = 0.720818
FEATURE [App::DocumentObjectGroupPython] N_element034  label="N_element : 0.076"  # scripted group (container) (typed FeaturePython)
  n = 0.0764169
FEATURE [App::DocumentObjectGroupPython] O_element074  label="O_element : 0.087"  # scripted group (container) (typed FeaturePython)
  n = 0.0872889
FEATURE [App::DocumentObjectGroupPython] G4_NYLON_11_RILSAN  label="G4_NYLON-11_RILSAN"  # scripted group (container) (typed FeaturePython)
  Dunit = g/cm3
  Dvalue = 1.425
  Group = -> [H_element066,C_element072,N_element034,O_element074]
  conduct = 2
  density = 1
  expand = 3
  formula = G4_NYLON-11_RILSAN
  name = G4_NYLON-11_RILSAN
  specific = 4
FEATURE [App::DocumentObjectGroupPython] C_element073  label="C_element : 8"  # scripted group (container) (typed FeaturePython)
  n = 8
  ref = C_element
FEATURE [App::DocumentObjectGroupPython] H_element067  label="H_element : 18"  # scripted group (container) (typed FeaturePython)
  n = 18
  ref = H_element
FEATURE [App::DocumentObjectGroupPython] G4_OCTANE  # scripted group (container) (typed FeaturePython)
  Dunit = g/cm3
  Dvalue = 0.7026
  Group = -> [C_element073,H_element067]
  conduct = 2
  density = 1
  expand = 3
  formula = G4_OCTANE
  name = G4_OCTANE
  specific = 4
FEATURE [App::DocumentObjectGroupPython] C_element074  label="C_element : 25"  # scripted group (container) (typed FeaturePython)
  n = 25
  ref = C_element
FEATURE [App::DocumentObjectGroupPython] H_element068  label="H_element : 52"  # scripted group (container) (typed FeaturePython)
  n = 52
  ref = H_element
FEATURE [App::DocumentObjectGroupPython] G4_PARAFFIN  # scripted group (container) (typed FeaturePython)
  Dunit = g/cm3
  Dvalue = 0.93
  Group = -> [C_element074,H_element068]
  conduct = 2
  density = 1
  expand = 3
  formula = G4_PARAFFIN
  name = G4_PARAFFIN
  specific = 4
FEATURE [App::DocumentObjectGroupPython] C_element075  label="C_element : 036"  # scripted group (container) (typed FeaturePython)
  n = 5
  ref = C_element
FEATURE [App::DocumentObjectGroupPython] H_element069  label="H_element : 032"  # scripted group (container) (typed FeaturePython)
  n = 12
  ref = H_element
FEATURE [App::DocumentObjectGroupPython] G4_N_PENTANE  label="G4_N-PENTANE"  # scripted group (container) (typed FeaturePython)
  Dunit = g/cm3
  Dvalue = 0.6262
  Group = -> [C_element075,H_element069]
  conduct = 2
  density = 1
  expand = 3
  formula = G4_N-PENTANE
  name = G4_N-PENTANE
  specific = 4
FEATURE [App::DocumentObjectGroupPython] H_element070  label="H_element : 0.014"  # scripted group (container) (typed FeaturePython)
  n = 0.0141
FEATURE [App::DocumentObjectGroupPython] C_element076  label="C_element : 0.072"  # scripted group (container) (typed FeaturePython)
  n = 0.072261
FEATURE [App::DocumentObjectGroupPython] N_element035  label="N_element : 0.019"  # scripted group (container) (typed FeaturePython)
  n = 0.01932
FEATURE [App::DocumentObjectGroupPython] O_element075  label="O_element : 0.066"  # scripted group (container) (typed FeaturePython)
  n = 0.066101
FEATURE [App::DocumentObjectGroupPython] S_element019  label="S_element : 0.020"  # scripted group (container) (typed FeaturePython)
  n = 0.00189
FEATURE [App::DocumentObjectGroupPython] Br_element004  label="Br_element : 0.349"  # scripted group (container) (typed FeaturePython)
  n = 0.349103
FEATURE [App::DocumentObjectGroupPython] Ag_element001  label="Ag_element : 0.474"  # scripted group (container) (typed FeaturePython)
  n = 0.474105
FEATURE [App::DocumentObjectGroupPython] I_element005  label="I_element : 0.003"  # scripted group (container) (typed FeaturePython)
  n = 0.00312
FEATURE [App::DocumentObjectGroupPython] G4_PHOTO_EMULSION  # scripted group (container) (typed FeaturePython)
  Dunit = g/cm3
  Dvalue = 3.815
  Group = -> [H_element070,C_element076,N_element035,O_element075,S_element019,Br_element004,Ag_element001,I_element005]
  conduct = 2
  density = 1
  expand = 3
  formula = G4_PHOTO_EMULSION
  name = G4_PHOTO_EMULSION
  specific = 4
FEATURE [App::DocumentObjectGroupPython] C_element077  label="C_element : 9"  # scripted group (container) (typed FeaturePython)
  n = 9
  ref = C_element
FEATURE [App::DocumentObjectGroupPython] H_element071  label="H_element : 033"  # scripted group (container) (typed FeaturePython)
  n = 10
  ref = H_element
FEATURE [App::DocumentObjectGroupPython] G4_PLASTIC_SC_VINYLTOLUENE  # scripted group (container) (typed FeaturePython)
  Dunit = g/cm3
  Dvalue = 1.032
  Group = -> [C_element077,H_element071]
  conduct = 2
  density = 1
  expand = 3
  formula = G4_PLASTIC_SC_VINYLTOLUENE
  name = G4_PLASTIC_SC_VINYLTOLUENE
  specific = 4
FEATURE [App::DocumentObjectGroupPython] Pu_element001  label="Pu_element : 1"  # scripted group (container) (typed FeaturePython)
  n = 1
  ref = Pu_element
FEATURE [App::DocumentObjectGroupPython] O_element076  label="O_element : 037"  # scripted group (container) (typed FeaturePython)
  n = 2
  ref = O_element
FEATURE [App::DocumentObjectGroupPython] G4_PLUTONIUM_DIOXIDE  # scripted group (container) (typed FeaturePython)
  Dunit = g/cm3
  Dvalue = 11.46
  Group = -> [Pu_element001,O_element076]
  conduct = 2
  density = 1
  expand = 3
  formula = G4_PLUTONIUM_DIOXIDE
  name = G4_PLUTONIUM_DIOXIDE
  specific = 4
FEATURE [App::DocumentObjectGroupPython] C_element078  label="C_element : 037"  # scripted group (container) (typed FeaturePython)
  n = 3
  ref = C_element
FEATURE [App::DocumentObjectGroupPython] H_element072  label="H_element : 034"  # scripted group (container) (typed FeaturePython)
  n = 3
  ref = H_element
FEATURE [App::DocumentObjectGroupPython] N_element036  label="N_element : 015"  # scripted group (container) (typed FeaturePython)
  n = 1
  ref = N_element
FEATURE [App::DocumentObjectGroupPython] G4_POLYACRYLONITRILE  # scripted group (container) (typed FeaturePython)
  Dunit = g/cm3
  Dvalue = 1.17
  Group = -> [C_element078,H_element072,N_element036]
  conduct = 2
  density = 1
  expand = 3
  formula = G4_POLYACRYLONITRILE
  name = G4_POLYACRYLONITRILE
  specific = 4
FEATURE [App::DocumentObjectGroupPython] C_element079  label="C_element : 16"  # scripted group (container) (typed FeaturePython)
  n = 16
  ref = C_element
FEATURE [App::DocumentObjectGroupPython] H_element073  label="H_element : 035"  # scripted group (container) (typed FeaturePython)
  n = 14
  ref = H_element
FEATURE [App::DocumentObjectGroupPython] O_element077  label="O_element : 038"  # scripted group (container) (typed FeaturePython)
  n = 3
  ref = O_element
FEATURE [App::DocumentObjectGroupPython] G4_POLYCARBONATE  # scripted group (container) (typed FeaturePython)
  Dunit = g/cm3
  Dvalue = 1.2
  Group = -> [C_element079,H_element073,O_element077]
  conduct = 2
  density = 1
  expand = 3
  formula = G4_POLYCARBONATE
  name = G4_POLYCARBONATE
  specific = 4
FEATURE [App::DocumentObjectGroupPython] C_element080  label="C_element : 038"  # scripted group (container) (typed FeaturePython)
  n = 8
  ref = C_element
FEATURE [App::DocumentObjectGroupPython] H_element074  label="H_element : 036"  # scripted group (container) (typed FeaturePython)
  n = 7
  ref = H_element
FEATURE [App::DocumentObjectGroupPython] Cl_element017  label="Cl_element : 007"  # scripted group (container) (typed FeaturePython)
  n = 1
  ref = Cl_element
FEATURE [App::DocumentObjectGroupPython] G4_POLYCHLOROSTYRENE  # scripted group (container) (typed FeaturePython)
  Dunit = g/cm3
  Dvalue = 1.3
  Group = -> [C_element080,H_element074,Cl_element017]
  conduct = 2
  density = 1
  expand = 3
  formula = G4_POLYCHLOROSTYRENE
  name = G4_POLYCHLOROSTYRENE
  specific = 4
FEATURE [App::DocumentObjectGroupPython] C_element081  label="C_element : 039"  # scripted group (container) (typed FeaturePython)
  n = 1
  ref = C_element
FEATURE [App::DocumentObjectGroupPython] H_element075  label="H_element : 037"  # scripted group (container) (typed FeaturePython)
  n = 2
  ref = H_element
FEATURE [App::DocumentObjectGroupPython] G4_POLYETHYLENE  # scripted group (container) (typed FeaturePython)
  Dunit = g/cm3
  Dvalue = 0.94
  Group = -> [C_element081,H_element075]
  conduct = 2
  density = 1
  expand = 3
  formula = G4_POLYETHYLENE
  name = G4_POLYETHYLENE
  specific = 4
FEATURE [App::DocumentObjectGroupPython] C_element082  label="C_element : 040"  # scripted group (container) (typed FeaturePython)
  n = 10
  ref = C_element
FEATURE [App::DocumentObjectGroupPython] H_element076  label="H_element : 038"  # scripted group (container) (typed FeaturePython)
  n = 8
  ref = H_element
FEATURE [App::DocumentObjectGroupPython] O_element078  label="O_element : 039"  # scripted group (container) (typed FeaturePython)
  n = 4
  ref = O_element
FEATURE [App::DocumentObjectGroupPython] G4_MYLAR  # scripted group (container) (typed FeaturePython)
  Dunit = g/cm3
  Dvalue = 1.4
  Group = -> [C_element082,H_element076,O_element078]
  conduct = 2
  density = 1
  expand = 3
  formula = G4_MYLAR
  name = G4_MYLAR
  specific = 4
FEATURE [App::DocumentObjectGroupPython] C_element083  label="C_element : 041"  # scripted group (container) (typed FeaturePython)
  n = 5
  ref = C_element
FEATURE [App::DocumentObjectGroupPython] H_element077  label="H_element : 039"  # scripted group (container) (typed FeaturePython)
  n = 8
  ref = H_element
FEATURE [App::DocumentObjectGroupPython] O_element079  label="O_element : 040"  # scripted group (container) (typed FeaturePython)
  n = 2
  ref = O_element
FEATURE [App::DocumentObjectGroupPython] G4_PLEXIGLASS  # scripted group (container) (typed FeaturePython)
  Dunit = g/cm3
  Dvalue = 1.19
  Group = -> [C_element083,H_element077,O_element079]
  conduct = 2
  density = 1
  expand = 3
  formula = G4_PLEXIGLASS
  name = G4_PLEXIGLASS
  specific = 4
FEATURE [App::DocumentObjectGroupPython] C_element084  label="C_element : 042"  # scripted group (container) (typed FeaturePython)
  n = 1
  ref = C_element
FEATURE [App::DocumentObjectGroupPython] H_element078  label="H_element : 040"  # scripted group (container) (typed FeaturePython)
  n = 2
  ref = H_element
FEATURE [App::DocumentObjectGroupPython] O_element080  label="O_element : 041"  # scripted group (container) (typed FeaturePython)
  n = 1
  ref = O_element
FEATURE [App::DocumentObjectGroupPython] G4_POLYOXYMETHYLENE  # scripted group (container) (typed FeaturePython)
  Dunit = g/cm3
  Dvalue = 1.425
  Group = -> [C_element084,H_element078,O_element080]
  conduct = 2
  density = 1
  expand = 3
  formula = G4_POLYOXYMETHYLENE
  name = G4_POLYOXYMETHYLENE
  specific = 4
FEATURE [App::DocumentObjectGroupPython] C_element085  label="C_element : 043"  # scripted group (container) (typed FeaturePython)
  n = 2
  ref = C_element
FEATURE [App::DocumentObjectGroupPython] H_element079  label="H_element : 041"  # scripted group (container) (typed FeaturePython)
  n = 4
  ref = H_element
FEATURE [App::DocumentObjectGroupPython] G4_POLYPROPYLENE  # scripted group (container) (typed FeaturePython)
  Dunit = g/cm3
  Dvalue = 0.9
  Group = -> [C_element085,H_element079]
  conduct = 2
  density = 1
  expand = 3
  formula = G4_POLYPROPYLENE
  name = G4_POLYPROPYLENE
  specific = 4
FEATURE [App::DocumentObjectGroupPython] C_element086  label="C_element : 044"  # scripted group (container) (typed FeaturePython)
  n = 8
  ref = C_element
FEATURE [App::DocumentObjectGroupPython] H_element080  label="H_element : 042"  # scripted group (container) (typed FeaturePython)
  n = 8
  ref = H_element
FEATURE [App::DocumentObjectGroupPython] G4_POLYSTYRENE  # scripted group (container) (typed FeaturePython)
  Dunit = g/cm3
  Dvalue = 1.06
  Group = -> [C_element086,H_element080]
  conduct = 2
  density = 1
  expand = 3
  formula = G4_POLYSTYRENE
  name = G4_POLYSTYRENE
  specific = 4
FEATURE [App::DocumentObjectGroupPython] C_element087  label="C_element : 045"  # scripted group (container) (typed FeaturePython)
  n = 2
  ref = C_element
FEATURE [App::DocumentObjectGroupPython] F_element014  label="F_element : 4"  # scripted group (container) (typed FeaturePython)
  n = 4
  ref = F_element
FEATURE [App::DocumentObjectGroupPython] G4_TEFLON  # scripted group (container) (typed FeaturePython)
  Dunit = g/cm3
  Dvalue = 2.2
  Group = -> [C_element087,F_element014]
  conduct = 2
  density = 1
  expand = 3
  formula = G4_TEFLON
  name = G4_TEFLON
  specific = 4
FEATURE [App::DocumentObjectGroupPython] C_element088  label="C_element : 046"  # scripted group (container) (typed FeaturePython)
  n = 2
  ref = C_element
FEATURE [App::DocumentObjectGroupPython] F_element015  label="F_element : 006"  # scripted group (container) (typed FeaturePython)
  n = 3
  ref = F_element
FEATURE [App::DocumentObjectGroupPython] Cl_element018  label="Cl_element : 008"  # scripted group (container) (typed FeaturePython)
  n = 1
  ref = Cl_element
FEATURE [App::DocumentObjectGroupPython] G4_POLYTRIFLUOROCHLOROETHYLENE  # scripted group (container) (typed FeaturePython)
  Dunit = g/cm3
  Dvalue = 2.1
  Group = -> [C_element088,F_element015,Cl_element018]
  conduct = 2
  density = 1
  expand = 3
  formula = G4_POLYTRIFLUOROCHLOROETHYLENE
  name = G4_POLYTRIFLUOROCHLOROETHYLENE
  specific = 4
FEATURE [App::DocumentObjectGroupPython] C_element089  label="C_element : 047"  # scripted group (container) (typed FeaturePython)
  n = 4
  ref = C_element
FEATURE [App::DocumentObjectGroupPython] H_element081  label="H_element : 043"  # scripted group (container) (typed FeaturePython)
  n = 6
  ref = H_element
FEATURE [App::DocumentObjectGroupPython] O_element081  label="O_element : 042"  # scripted group (container) (typed FeaturePython)
  n = 2
  ref = O_element
FEATURE [App::DocumentObjectGroupPython] G4_POLYVINYL_ACETATE  # scripted group (container) (typed FeaturePython)
  Dunit = g/cm3
  Dvalue = 1.19
  Group = -> [C_element089,H_element081,O_element081]
  conduct = 2
  density = 1
  expand = 3
  formula = G4_POLYVINYL_ACETATE
  name = G4_POLYVINYL_ACETATE
  specific = 4
FEATURE [App::DocumentObjectGroupPython] C_element090  label="C_element : 048"  # scripted group (container) (typed FeaturePython)
  n = 2
  ref = C_element
FEATURE [App::DocumentObjectGroupPython] H_element082  label="H_element : 044"  # scripted group (container) (typed FeaturePython)
  n = 4
  ref = H_element
FEATURE [App::DocumentObjectGroupPython] O_element082  label="O_element : 043"  # scripted group (container) (typed FeaturePython)
  n = 1
  ref = O_element
FEATURE [App::DocumentObjectGroupPython] G4_POLYVINYL_ALCOHOL  # scripted group (container) (typed FeaturePython)
  Dunit = g/cm3
  Dvalue = 1.3
  Group = -> [C_element090,H_element082,O_element082]
  conduct = 2
  density = 1
  expand = 3
  formula = G4_POLYVINYL_ALCOHOL
  name = G4_POLYVINYL_ALCOHOL
  specific = 4
FEATURE [App::DocumentObjectGroupPython] C_element091  label="C_element : 049"  # scripted group (container) (typed FeaturePython)
  n = 8
  ref = C_element
FEATURE [App::DocumentObjectGroupPython] H_element083  label="H_element : 045"  # scripted group (container) (typed FeaturePython)
  n = 14
  ref = H_element
FEATURE [App::DocumentObjectGroupPython] O_element083  label="O_element : 044"  # scripted group (container) (typed FeaturePython)
  n = 2
  ref = O_element
FEATURE [App::DocumentObjectGroupPython] G4_POLYVINYL_BUTYRAL  # scripted group (container) (typed FeaturePython)
  Dunit = g/cm3
  Dvalue = 1.12
  Group = -> [C_element091,H_element083,O_element083]
  conduct = 2
  density = 1
  expand = 3
  formula = G4_POLYVINYL_BUTYRAL
  name = G4_POLYVINYL_BUTYRAL
  specific = 4
FEATURE [App::DocumentObjectGroupPython] C_element092  label="C_element : 050"  # scripted group (container) (typed FeaturePython)
  n = 2
  ref = C_element
FEATURE [App::DocumentObjectGroupPython] H_element084  label="H_element : 046"  # scripted group (container) (typed FeaturePython)
  n = 3
  ref = H_element
FEATURE [App::DocumentObjectGroupPython] Cl_element019  label="Cl_element : 009"  # scripted group (container) (typed FeaturePython)
  n = 1
  ref = Cl_element
FEATURE [App::DocumentObjectGroupPython] G4_POLYVINYL_CHLORIDE  # scripted group (container) (typed FeaturePython)
  Dunit = g/cm3
  Dvalue = 1.3
  Group = -> [C_element092,H_element084,Cl_element019]
  conduct = 2
  density = 1
  expand = 3
  formula = G4_POLYVINYL_CHLORIDE
  name = G4_POLYVINYL_CHLORIDE
  specific = 4
FEATURE [App::DocumentObjectGroupPython] C_element093  label="C_element : 051"  # scripted group (container) (typed FeaturePython)
  n = 2
  ref = C_element
FEATURE [App::DocumentObjectGroupPython] H_element085  label="H_element : 047"  # scripted group (container) (typed FeaturePython)
  n = 2
  ref = H_element
FEATURE [App::DocumentObjectGroupPython] Cl_element020  label="Cl_element : 010"  # scripted group (container) (typed FeaturePython)
  n = 2
  ref = Cl_element
FEATURE [App::DocumentObjectGroupPython] G4_POLYVINYLIDENE_CHLORIDE  # scripted group (container) (typed FeaturePython)
  Dunit = g/cm3
  Dvalue = 1.7
  Group = -> [C_element093,H_element085,Cl_element020]
  conduct = 2
  density = 1
  expand = 3
  formula = G4_POLYVINYLIDENE_CHLORIDE
  name = G4_POLYVINYLIDENE_CHLORIDE
  specific = 4
FEATURE [App::DocumentObjectGroupPython] C_element094  label="C_element : 052"  # scripted group (container) (typed FeaturePython)
  n = 2
  ref = C_element
FEATURE [App::DocumentObjectGroupPython] H_element086  label="H_element : 048"  # scripted group (container) (typed FeaturePython)
  n = 2
  ref = H_element
FEATURE [App::DocumentObjectGroupPython] F_element016  label="F_element : 007"  # scripted group (container) (typed FeaturePython)
  n = 2
  ref = F_element
FEATURE [App::DocumentObjectGroupPython] G4_POLYVINYLIDENE_FLUORIDE  # scripted group (container) (typed FeaturePython)
  Dunit = g/cm3
  Dvalue = 1.76
  Group = -> [C_element094,H_element086,F_element016]
  conduct = 2
  density = 1
  expand = 3
  formula = G4_POLYVINYLIDENE_FLUORIDE
  name = G4_POLYVINYLIDENE_FLUORIDE
  specific = 4
FEATURE [App::DocumentObjectGroupPython] C_element095  label="C_element : 053"  # scripted group (container) (typed FeaturePython)
  n = 6
  ref = C_element
FEATURE [App::DocumentObjectGroupPython] H_element087  label="H_element : 9"  # scripted group (container) (typed FeaturePython)
  n = 9
  ref = H_element
FEATURE [App::DocumentObjectGroupPython] N_element037  label="N_element : 016"  # scripted group (container) (typed FeaturePython)
  n = 1
  ref = N_element
FEATURE [App::DocumentObjectGroupPython] O_element084  label="O_element : 045"  # scripted group (container) (typed FeaturePython)
  n = 1
  ref = O_element
FEATURE [App::DocumentObjectGroupPython] G4_POLYVINYL_PYRROLIDONE  # scripted group (container) (typed FeaturePython)
  Dunit = g/cm3
  Dvalue = 1.25
  Group = -> [C_element095,H_element087,N_element037,O_element084]
  conduct = 2
  density = 1
  expand = 3
  formula = G4_POLYVINYL_PYRROLIDONE
  name = G4_POLYVINYL_PYRROLIDONE
  specific = 4
FEATURE [App::DocumentObjectGroupPython] K_element008  label="K_element : 1"  # scripted group (container) (typed FeaturePython)
  n = 1
  ref = K_element
FEATURE [App::DocumentObjectGroupPython] I_element006  label="I_element : 003"  # scripted group (container) (typed FeaturePython)
  n = 1
  ref = I_element
FEATURE [App::DocumentObjectGroupPython] G4_POTASSIUM_IODIDE  # scripted group (container) (typed FeaturePython)
  Dunit = g/cm3
  Dvalue = 3.13
  Group = -> [K_element008,I_element006]
  conduct = 2
  density = 1
  expand = 3
  formula = G4_POTASSIUM_IODIDE
  name = G4_POTASSIUM_IODIDE
  specific = 4
FEATURE [App::DocumentObjectGroupPython] K_element009  label="K_element : 2"  # scripted group (container) (typed FeaturePython)
  n = 2
  ref = K_element
FEATURE [App::DocumentObjectGroupPython] O_element085  label="O_element : 046"  # scripted group (container) (typed FeaturePython)
  n = 1
  ref = O_element
FEATURE [App::DocumentObjectGroupPython] G4_POTASSIUM_OXIDE  # scripted group (container) (typed FeaturePython)
  Dunit = g/cm3
  Dvalue = 2.32
  Group = -> [K_element009,O_element085]
  conduct = 2
  density = 1
  expand = 3
  formula = G4_POTASSIUM_OXIDE
  name = G4_POTASSIUM_OXIDE
  specific = 4
FEATURE [App::DocumentObjectGroupPython] C_element096  label="C_element : 054"  # scripted group (container) (typed FeaturePython)
  n = 3
  ref = C_element
FEATURE [App::DocumentObjectGroupPython] H_element088  label="H_element : 049"  # scripted group (container) (typed FeaturePython)
  n = 8
  ref = H_element
FEATURE [App::DocumentObjectGroupPython] G4_PROPANE  # scripted group (container) (typed FeaturePython)
  Dunit = g/cm3
  Dvalue = 0.00187939
  Group = -> [C_element096,H_element088]
  conduct = 2
  density = 1
  expand = 3
  formula = G4_PROPANE
  name = G4_PROPANE
  specific = 4
FEATURE [App::DocumentObjectGroupPython] C_element097  label="C_element : 055"  # scripted group (container) (typed FeaturePython)
  n = 3
  ref = C_element
FEATURE [App::DocumentObjectGroupPython] H_element089  label="H_element : 050"  # scripted group (container) (typed FeaturePython)
  n = 8
  ref = H_element
FEATURE [App::DocumentObjectGroupPython] G4_lPROPANE  # scripted group (container) (typed FeaturePython)
  Dunit = g/cm3
  Dvalue = 0.43
  Group = -> [C_element097,H_element089]
  conduct = 2
  density = 1
  expand = 3
  formula = G4_lPROPANE
  name = G4_lPROPANE
  specific = 4
FEATURE [App::DocumentObjectGroupPython] C_element098  label="C_element : 056"  # scripted group (container) (typed FeaturePython)
  n = 3
  ref = C_element
FEATURE [App::DocumentObjectGroupPython] H_element090  label="H_element : 051"  # scripted group (container) (typed FeaturePython)
  n = 8
  ref = H_element
FEATURE [App::DocumentObjectGroupPython] O_element086  label="O_element : 047"  # scripted group (container) (typed FeaturePython)
  n = 1
  ref = O_element
FEATURE [App::DocumentObjectGroupPython] G4_N_PROPYL_ALCOHOL  label="G4_N-PROPYL_ALCOHOL"  # scripted group (container) (typed FeaturePython)
  Dunit = g/cm3
  Dvalue = 0.8035
  Group = -> [C_element098,H_element090,O_element086]
  conduct = 2
  density = 1
  expand = 3
  formula = G4_N-PROPYL_ALCOHOL
  name = G4_N-PROPYL_ALCOHOL
  specific = 4
FEATURE [App::DocumentObjectGroupPython] C_element099  label="C_element : 057"  # scripted group (container) (typed FeaturePython)
  n = 5
  ref = C_element
FEATURE [App::DocumentObjectGroupPython] H_element091  label="H_element : 052"  # scripted group (container) (typed FeaturePython)
  n = 5
  ref = H_element
FEATURE [App::DocumentObjectGroupPython] N_element038  label="N_element : 017"  # scripted group (container) (typed FeaturePython)
  n = 1
  ref = N_element
FEATURE [App::DocumentObjectGroupPython] G4_PYRIDINE  # scripted group (container) (typed FeaturePython)
  Dunit = g/cm3
  Dvalue = 0.9819
  Group = -> [C_element099,H_element091,N_element038]
  conduct = 2
  density = 1
  expand = 3
  formula = G4_PYRIDINE
  name = G4_PYRIDINE
  specific = 4
FEATURE [App::DocumentObjectGroupPython] H_element092  label="H_element : 0.144"  # scripted group (container) (typed FeaturePython)
  n = 0.143711
FEATURE [App::DocumentObjectGroupPython] C_element100  label="C_element : 0.856"  # scripted group (container) (typed FeaturePython)
  n = 0.856289
FEATURE [App::DocumentObjectGroupPython] G4_RUBBER_BUTYL  # scripted group (container) (typed FeaturePython)
  Dunit = g/cm3
  Dvalue = 0.92
  Group = -> [H_element092,C_element100]
  conduct = 2
  density = 1
  expand = 3
  formula = G4_RUBBER_BUTYL
  name = G4_RUBBER_BUTYL
  specific = 4
FEATURE [App::DocumentObjectGroupPython] H_element093  label="H_element : 0.118"  # scripted group (container) (typed FeaturePython)
  n = 0.118371
FEATURE [App::DocumentObjectGroupPython] C_element101  label="C_element : 0.882"  # scripted group (container) (typed FeaturePython)
  n = 0.881629
FEATURE [App::DocumentObjectGroupPython] G4_RUBBER_NATURAL  # scripted group (container) (typed FeaturePython)
  Dunit = g/cm3
  Dvalue = 0.92
  Group = -> [H_element093,C_element101]
  conduct = 2
  density = 1
  expand = 3
  formula = G4_RUBBER_NATURAL
  name = G4_RUBBER_NATURAL
  specific = 4
FEATURE [App::DocumentObjectGroupPython] H_element094  label="H_element : 0.145"  # scripted group (container) (typed FeaturePython)
  n = 0.05692
FEATURE [App::DocumentObjectGroupPython] C_element102  label="C_element : 0.543"  # scripted group (container) (typed FeaturePython)
  n = 0.542646
FEATURE [App::DocumentObjectGroupPython] Cl_element021  label="Cl_element : 0.400"  # scripted group (container) (typed FeaturePython)
  n = 0.400434
FEATURE [App::DocumentObjectGroupPython] G4_RUBBER_NEOPRENE  # scripted group (container) (typed FeaturePython)
  Dunit = g/cm3
  Dvalue = 1.23
  Group = -> [H_element094,C_element102,Cl_element021]
  conduct = 2
  density = 1
  expand = 3
  formula = G4_RUBBER_NEOPRENE
  name = G4_RUBBER_NEOPRENE
  specific = 4
FEATURE [App::DocumentObjectGroupPython] Si_element006  label="Si_element : 1"  # scripted group (container) (typed FeaturePython)
  n = 1
  ref = Si_element
FEATURE [App::DocumentObjectGroupPython] O_element087  label="O_element : 048"  # scripted group (container) (typed FeaturePython)
  n = 2
  ref = O_element
FEATURE [App::DocumentObjectGroupPython] G4_SILICON_DIOXIDE  # scripted group (container) (typed FeaturePython)
  Dunit = g/cm3
  Dvalue = 2.32
  Group = -> [Si_element006,O_element087]
  conduct = 2
  density = 1
  expand = 3
  formula = G4_SILICON_DIOXIDE
  name = G4_SILICON_DIOXIDE
  specific = 4
FEATURE [App::DocumentObjectGroupPython] Ag_element002  label="Ag_element : 1"  # scripted group (container) (typed FeaturePython)
  n = 1
  ref = Ag_element
FEATURE [App::DocumentObjectGroupPython] Br_element005  label="Br_element : 003"  # scripted group (container) (typed FeaturePython)
  n = 1
  ref = Br_element
FEATURE [App::DocumentObjectGroupPython] G4_SILVER_BROMIDE  # scripted group (container) (typed FeaturePython)
  Dunit = g/cm3
  Dvalue = 6.473
  Group = -> [Ag_element002,Br_element005]
  conduct = 2
  density = 1
  expand = 3
  formula = G4_SILVER_BROMIDE
  name = G4_SILVER_BROMIDE
  specific = 4
FEATURE [App::DocumentObjectGroupPython] Ag_element003  label="Ag_element : 002"  # scripted group (container) (typed FeaturePython)
  n = 1
  ref = Ag_element
FEATURE [App::DocumentObjectGroupPython] Cl_element022  label="Cl_element : 011"  # scripted group (container) (typed FeaturePython)
  n = 1
  ref = Cl_element
FEATURE [App::DocumentObjectGroupPython] G4_SILVER_CHLORIDE  # scripted group (container) (typed FeaturePython)
  Dunit = g/cm3
  Dvalue = 5.56
  Group = -> [Ag_element003,Cl_element022]
  conduct = 2
  density = 1
  expand = 3
  formula = G4_SILVER_CHLORIDE
  name = G4_SILVER_CHLORIDE
  specific = 4
FEATURE [App::DocumentObjectGroupPython] Br_element006  label="Br_element : 0.423"  # scripted group (container) (typed FeaturePython)
  n = 0.422895
FEATURE [App::DocumentObjectGroupPython] Ag_element004  label="Ag_element : 0.574"  # scripted group (container) (typed FeaturePython)
  n = 0.573748
FEATURE [App::DocumentObjectGroupPython] I_element007  label="I_element : 0.649"  # scripted group (container) (typed FeaturePython)
  n = 0.003357
FEATURE [App::DocumentObjectGroupPython] G4_SILVER_HALIDES  # scripted group (container) (typed FeaturePython)
  Dunit = g/cm3
  Dvalue = 6.47
  Group = -> [Br_element006,Ag_element004,I_element007]
  conduct = 2
  density = 1
  expand = 3
  formula = G4_SILVER_HALIDES
  name = G4_SILVER_HALIDES
  specific = 4
FEATURE [App::DocumentObjectGroupPython] Ag_element005  label="Ag_element : 003"  # scripted group (container) (typed FeaturePython)
  n = 1
  ref = Ag_element
FEATURE [App::DocumentObjectGroupPython] I_element008  label="I_element : 004"  # scripted group (container) (typed FeaturePython)
  n = 1
  ref = I_element
FEATURE [App::DocumentObjectGroupPython] G4_SILVER_IODIDE  # scripted group (container) (typed FeaturePython)
  Dunit = g/cm3
  Dvalue = 6.01
  Group = -> [Ag_element005,I_element008]
  conduct = 2
  density = 1
  expand = 3
  formula = G4_SILVER_IODIDE
  name = G4_SILVER_IODIDE
  specific = 4
FEATURE [App::DocumentObjectGroupPython] H_element095  label="H_element : 0.100"  # scripted group (container) (typed FeaturePython)
  n = 0.1
FEATURE [App::DocumentObjectGroupPython] C_element103  label="C_element : 0.204"  # scripted group (container) (typed FeaturePython)
  n = 0.204
FEATURE [App::DocumentObjectGroupPython] N_element039  label="N_element : 0.759"  # scripted group (container) (typed FeaturePython)
  n = 0.042
FEATURE [App::DocumentObjectGroupPython] O_element088  label="O_element : 0.645"  # scripted group (container) (typed FeaturePython)
  n = 0.645
FEATURE [App::DocumentObjectGroupPython] Na_element013  label="Na_element : 0.100"  # scripted group (container) (typed FeaturePython)
  n = 0.002
FEATURE [App::DocumentObjectGroupPython] P_element009  label="P_element : 0.107"  # scripted group (container) (typed FeaturePython)
  n = 0.001
FEATURE [App::DocumentObjectGroupPython] S_element020  label="S_element : 0.021"  # scripted group (container) (typed FeaturePython)
  n = 0.002
FEATURE [App::DocumentObjectGroupPython] Cl_element023  label="Cl_element : 0.590"  # scripted group (container) (typed FeaturePython)
  n = 0.003
FEATURE [App::DocumentObjectGroupPython] K_element010  label="K_element : 0.001"  # scripted group (container) (typed FeaturePython)
  n = 0.001
FEATURE [App::DocumentObjectGroupPython] G4_SKIN_ICRP  # scripted group (container) (typed FeaturePython)
  Dunit = g/cm3
  Dvalue = 1.09
  Group = -> [H_element095,C_element103,N_element039,O_element088,Na_element013,P_element009,S_element020,Cl_element023,K_element010]
  conduct = 2
  density = 1
  expand = 3
  formula = G4_SKIN_ICRP
  name = G4_SKIN_ICRP
  specific = 4
FEATURE [App::DocumentObjectGroupPython] Na_element014  label="Na_element : 2"  # scripted group (container) (typed FeaturePython)
  n = 2
  ref = Na_element
FEATURE [App::DocumentObjectGroupPython] C_element104  label="C_element : 058"  # scripted group (container) (typed FeaturePython)
  n = 1
  ref = C_element
FEATURE [App::DocumentObjectGroupPython] O_element089  label="O_element : 049"  # scripted group (container) (typed FeaturePython)
  n = 3
  ref = O_element
FEATURE [App::DocumentObjectGroupPython] G4_SODIUM_CARBONATE  # scripted group (container) (typed FeaturePython)
  Dunit = g/cm3
  Dvalue = 2.532
  Group = -> [Na_element014,C_element104,O_element089]
  conduct = 2
  density = 1
  expand = 3
  formula = G4_SODIUM_CARBONATE
  name = G4_SODIUM_CARBONATE
  specific = 4
FEATURE [App::DocumentObjectGroupPython] Na_element015  label="Na_element : 1"  # scripted group (container) (typed FeaturePython)
  n = 1
  ref = Na_element
FEATURE [App::DocumentObjectGroupPython] I_element009  label="I_element : 005"  # scripted group (container) (typed FeaturePython)
  n = 1
  ref = I_element
FEATURE [App::DocumentObjectGroupPython] G4_SODIUM_IODIDE  # scripted group (container) (typed FeaturePython)
  Dunit = g/cm3
  Dvalue = 3.667
  Group = -> [Na_element015,I_element009]
  conduct = 2
  density = 1
  expand = 3
  formula = G4_SODIUM_IODIDE
  name = G4_SODIUM_IODIDE
  specific = 4
FEATURE [App::DocumentObjectGroupPython] Na_element016  label="Na_element : 003"  # scripted group (container) (typed FeaturePython)
  n = 2
  ref = Na_element
FEATURE [App::DocumentObjectGroupPython] O_element090  label="O_element : 050"  # scripted group (container) (typed FeaturePython)
  n = 1
  ref = O_element
FEATURE [App::DocumentObjectGroupPython] G4_SODIUM_MONOXIDE  # scripted group (container) (typed FeaturePython)
  Dunit = g/cm3
  Dvalue = 2.27
  Group = -> [Na_element016,O_element090]
  conduct = 2
  density = 1
  expand = 3
  formula = G4_SODIUM_MONOXIDE
  name = G4_SODIUM_MONOXIDE
  specific = 4
FEATURE [App::DocumentObjectGroupPython] Na_element017  label="Na_element : 004"  # scripted group (container) (typed FeaturePython)
  n = 1
  ref = Na_element
FEATURE [App::DocumentObjectGroupPython] N_element040  label="N_element : 018"  # scripted group (container) (typed FeaturePython)
  n = 1
  ref = N_element
FEATURE [App::DocumentObjectGroupPython] O_element091  label="O_element : 051"  # scripted group (container) (typed FeaturePython)
  n = 3
  ref = O_element
FEATURE [App::DocumentObjectGroupPython] G4_SODIUM_NITRATE  # scripted group (container) (typed FeaturePython)
  Dunit = g/cm3
  Dvalue = 2.261
  Group = -> [Na_element017,N_element040,O_element091]
  conduct = 2
  density = 1
  expand = 3
  formula = G4_SODIUM_NITRATE
  name = G4_SODIUM_NITRATE
  specific = 4
FEATURE [App::DocumentObjectGroupPython] C_element105  label="C_element : 059"  # scripted group (container) (typed FeaturePython)
  n = 14
  ref = C_element
FEATURE [App::DocumentObjectGroupPython] H_element096  label="H_element : 053"  # scripted group (container) (typed FeaturePython)
  n = 12
  ref = H_element
FEATURE [App::DocumentObjectGroupPython] G4_STILBENE  # scripted group (container) (typed FeaturePython)
  Dunit = g/cm3
  Dvalue = 0.9707
  Group = -> [C_element105,H_element096]
  conduct = 2
  density = 1
  expand = 3
  formula = G4_STILBENE
  name = G4_STILBENE
  specific = 4
FEATURE [App::DocumentObjectGroupPython] C_element106  label="C_element : 12"  # scripted group (container) (typed FeaturePython)
  n = 12
  ref = C_element
FEATURE [App::DocumentObjectGroupPython] H_element097  label="H_element : 22"  # scripted group (container) (typed FeaturePython)
  n = 22
  ref = H_element
FEATURE [App::DocumentObjectGroupPython] O_element092  label="O_element : 11"  # scripted group (container) (typed FeaturePython)
  n = 11
  ref = O_element
FEATURE [App::DocumentObjectGroupPython] G4_SUCROSE  # scripted group (container) (typed FeaturePython)
  Dunit = g/cm3
  Dvalue = 1.5805
  Group = -> [C_element106,H_element097,O_element092]
  conduct = 2
  density = 1
  expand = 3
  formula = G4_SUCROSE
  name = G4_SUCROSE
  specific = 4
FEATURE [App::DocumentObjectGroupPython] C_element107  label="C_element : 18"  # scripted group (container) (typed FeaturePython)
  n = 18
  ref = C_element
FEATURE [App::DocumentObjectGroupPython] H_element098  label="H_element : 054"  # scripted group (container) (typed FeaturePython)
  n = 14
  ref = H_element
FEATURE [App::DocumentObjectGroupPython] G4_TERPHENYL  # scripted group (container) (typed FeaturePython)
  Dunit = g/cm3
  Dvalue = 1.24
  Group = -> [C_element107,H_element098]
  conduct = 2
  density = 1
  expand = 3
  formula = G4_TERPHENYL
  name = G4_TERPHENYL
  specific = 4
FEATURE [App::DocumentObjectGroupPython] H_element099  label="H_element : 0.146"  # scripted group (container) (typed FeaturePython)
  n = 0.106
FEATURE [App::DocumentObjectGroupPython] C_element108  label="C_element : 0.883"  # scripted group (container) (typed FeaturePython)
  n = 0.099
FEATURE [App::DocumentObjectGroupPython] N_element041  label="N_element : 0.020"  # scripted group (container) (typed FeaturePython)
  n = 0.02
FEATURE [App::DocumentObjectGroupPython] O_element093  label="O_element : 0.766"  # scripted group (container) (typed FeaturePython)
  n = 0.766
FEATURE [App::DocumentObjectGroupPython] Na_element018  label="Na_element : 0.101"  # scripted group (container) (typed FeaturePython)
  n = 0.002
FEATURE [App::DocumentObjectGroupPython] P_element010  label="P_element : 0.108"  # scripted group (container) (typed FeaturePython)
  n = 0.001
FEATURE [App::DocumentObjectGroupPython] S_element021  label="S_element : 0.022"  # scripted group (container) (typed FeaturePython)
  n = 0.002
FEATURE [App::DocumentObjectGroupPython] Cl_element024  label="Cl_element : 0.002"  # scripted group (container) (typed FeaturePython)
  n = 0.002
FEATURE [App::DocumentObjectGroupPython] K_element011  label="K_element : 0.017"  # scripted group (container) (typed FeaturePython)
  n = 0.002
FEATURE [App::DocumentObjectGroupPython] G4_TESTIS_ICRP  # scripted group (container) (typed FeaturePython)
  Dunit = g/cm3
  Dvalue = 1.04
  Group = -> [H_element099,C_element108,N_element041,O_element093,Na_element018,P_element010,S_element021,Cl_element024,K_element011]
  conduct = 2
  density = 1
  expand = 3
  formula = G4_TESTIS_ICRP
  name = G4_TESTIS_ICRP
  specific = 4
FEATURE [App::DocumentObjectGroupPython] C_element109  label="C_element : 060"  # scripted group (container) (typed FeaturePython)
  n = 2
  ref = C_element
FEATURE [App::DocumentObjectGroupPython] Cl_element025  label="Cl_element : 012"  # scripted group (container) (typed FeaturePython)
  n = 4
  ref = Cl_element
FEATURE [App::DocumentObjectGroupPython] G4_TETRACHLOROETHYLENE  # scripted group (container) (typed FeaturePython)
  Dunit = g/cm3
  Dvalue = 1.625
  Group = -> [C_element109,Cl_element025]
  conduct = 2
  density = 1
  expand = 3
  formula = G4_TETRACHLOROETHYLENE
  name = G4_TETRACHLOROETHYLENE
  specific = 4
FEATURE [App::DocumentObjectGroupPython] Tl_element001  label="Tl_element : 1"  # scripted group (container) (typed FeaturePython)
  n = 1
  ref = Tl_element
FEATURE [App::DocumentObjectGroupPython] Cl_element026  label="Cl_element : 013"  # scripted group (container) (typed FeaturePython)
  n = 1
  ref = Cl_element
FEATURE [App::DocumentObjectGroupPython] G4_THALLIUM_CHLORIDE  # scripted group (container) (typed FeaturePython)
  Dunit = g/cm3
  Dvalue = 7.004
  Group = -> [Tl_element001,Cl_element026]
  conduct = 2
  density = 1
  expand = 3
  formula = G4_THALLIUM_CHLORIDE
  name = G4_THALLIUM_CHLORIDE
  specific = 4
FEATURE [App::DocumentObjectGroupPython] H_element100  label="H_element : 0.147"  # scripted group (container) (typed FeaturePython)
  n = 0.105
FEATURE [App::DocumentObjectGroupPython] C_element110  label="C_element : 0.256"  # scripted group (container) (typed FeaturePython)
  n = 0.256
FEATURE [App::DocumentObjectGroupPython] N_element042  label="N_element : 0.760"  # scripted group (container) (typed FeaturePython)
  n = 0.027
FEATURE [App::DocumentObjectGroupPython] O_element094  label="O_element : 0.602"  # scripted group (container) (typed FeaturePython)
  n = 0.602
FEATURE [App::DocumentObjectGroupPython] Na_element019  label="Na_element : 0.102"  # scripted group (container) (typed FeaturePython)
  n = 0.001
FEATURE [App::DocumentObjectGroupPython] P_element011  label="P_element : 0.109"  # scripted group (container) (typed FeaturePython)
  n = 0.002
FEATURE [App::DocumentObjectGroupPython] S_element022  label="S_element : 0.023"  # scripted group (container) (typed FeaturePython)
  n = 0.003
FEATURE [App::DocumentObjectGroupPython] Cl_element027  label="Cl_element : 0.591"  # scripted group (container) (typed FeaturePython)
  n = 0.002
FEATURE [App::DocumentObjectGroupPython] K_element012  label="K_element : 0.018"  # scripted group (container) (typed FeaturePython)
  n = 0.002
FEATURE [App::DocumentObjectGroupPython] G4_TISSUE_SOFT_ICRP  # scripted group (container) (typed FeaturePython)
  Dunit = g/cm3
  Dvalue = 1.03
  Group = -> [H_element100,C_element110,N_element042,O_element094,Na_element019,P_element011,S_element022,Cl_element027,K_element012]
  conduct = 2
  density = 1
  expand = 3
  formula = G4_TISSUE_SOFT_ICRP
  name = G4_TISSUE_SOFT_ICRP
  specific = 4
FEATURE [App::DocumentObjectGroupPython] H_element101  label="H_element : 0.148"  # scripted group (container) (typed FeaturePython)
  n = 0.101
FEATURE [App::DocumentObjectGroupPython] C_element111  label="C_element : 0.111"  # scripted group (container) (typed FeaturePython)
  n = 0.111
FEATURE [App::DocumentObjectGroupPython] N_element043  label="N_element : 0.026"  # scripted group (container) (typed FeaturePython)
  n = 0.026
FEATURE [App::DocumentObjectGroupPython] O_element095  label="O_element : 0.762"  # scripted group (container) (typed FeaturePython)
  n = 0.762
FEATURE [App::DocumentObjectGroupPython] G4_TISSUE_SOFT_ICRU_4  label="G4_TISSUE_SOFT_ICRU-4"  # scripted group (container) (typed FeaturePython)
  Dunit = g/cm3
  Dvalue = 1
  Group = -> [H_element101,C_element111,N_element043,O_element095]
  conduct = 2
  density = 1
  expand = 3
  formula = G4_TISSUE_SOFT_ICRU-4
  name = G4_TISSUE_SOFT_ICRU-4
  specific = 4
FEATURE [App::DocumentObjectGroupPython] H_element102  label="H_element : 0.149"  # scripted group (container) (typed FeaturePython)
  n = 0.101869
FEATURE [App::DocumentObjectGroupPython] C_element112  label="C_element : 0.456"  # scripted group (container) (typed FeaturePython)
  n = 0.456179
FEATURE [App::DocumentObjectGroupPython] N_element044  label="N_element : 0.761"  # scripted group (container) (typed FeaturePython)
  n = 0.035172
FEATURE [App::DocumentObjectGroupPython] O_element096  label="O_element : 0.407"  # scripted group (container) (typed FeaturePython)
  n = 0.40678
FEATURE [App::DocumentObjectGroupPython] G4_TISSUE_METHANE  label="G4_TISSUE-METHANE"  # scripted group (container) (typed FeaturePython)
  Dunit = g/cm3
  Dvalue = 0.00106409
  Group = -> [H_element102,C_element112,N_element044,O_element096]
  conduct = 2
  density = 1
  expand = 3
  formula = G4_TISSUE-METHANE
  name = G4_TISSUE-METHANE
  specific = 4
FEATURE [App::DocumentObjectGroupPython] H_element103  label="H_element : 0.103"  # scripted group (container) (typed FeaturePython)
  n = 0.102672
FEATURE [App::DocumentObjectGroupPython] C_element113  label="C_element : 0.569"  # scripted group (container) (typed FeaturePython)
  n = 0.56894
FEATURE [App::DocumentObjectGroupPython] N_element045  label="N_element : 0.762"  # scripted group (container) (typed FeaturePython)
  n = 0.035022
FEATURE [App::DocumentObjectGroupPython] O_element097  label="O_element : 0.293"  # scripted group (container) (typed FeaturePython)
  n = 0.293366
FEATURE [App::DocumentObjectGroupPython] G4_TISSUE_PROPANE  label="G4_TISSUE-PROPANE"  # scripted group (container) (typed FeaturePython)
  Dunit = g/cm3
  Dvalue = 0.00182628
  Group = -> [H_element103,C_element113,N_element045,O_element097]
  conduct = 2
  density = 1
  expand = 3
  formula = G4_TISSUE-PROPANE
  name = G4_TISSUE-PROPANE
  specific = 4
FEATURE [App::DocumentObjectGroupPython] Ti_element003  label="Ti_element : 1"  # scripted group (container) (typed FeaturePython)
  n = 1
  ref = Ti_element
FEATURE [App::DocumentObjectGroupPython] O_element098  label="O_element : 052"  # scripted group (container) (typed FeaturePython)
  n = 2
  ref = O_element
FEATURE [App::DocumentObjectGroupPython] G4_TITANIUM_DIOXIDE  # scripted group (container) (typed FeaturePython)
  Dunit = g/cm3
  Dvalue = 4.26
  Group = -> [Ti_element003,O_element098]
  conduct = 2
  density = 1
  expand = 3
  formula = G4_TITANIUM_DIOXIDE
  name = G4_TITANIUM_DIOXIDE
  specific = 4
FEATURE [App::DocumentObjectGroupPython] C_element114  label="C_element : 061"  # scripted group (container) (typed FeaturePython)
  n = 7
  ref = C_element
FEATURE [App::DocumentObjectGroupPython] H_element104  label="H_element : 055"  # scripted group (container) (typed FeaturePython)
  n = 8
  ref = H_element
FEATURE [App::DocumentObjectGroupPython] G4_TOLUENE  # scripted group (container) (typed FeaturePython)
  Dunit = g/cm3
  Dvalue = 0.8669
  Group = -> [C_element114,H_element104]
  conduct = 2
  density = 1
  expand = 3
  formula = G4_TOLUENE
  name = G4_TOLUENE
  specific = 4
FEATURE [App::DocumentObjectGroupPython] C_element115  label="C_element : 062"  # scripted group (container) (typed FeaturePython)
  n = 2
  ref = C_element
FEATURE [App::DocumentObjectGroupPython] H_element105  label="H_element : 056"  # scripted group (container) (typed FeaturePython)
  n = 1
  ref = H_element
FEATURE [App::DocumentObjectGroupPython] Cl_element028  label="Cl_element : 014"  # scripted group (container) (typed FeaturePython)
  n = 3
  ref = Cl_element
FEATURE [App::DocumentObjectGroupPython] G4_TRICHLOROETHYLENE  # scripted group (container) (typed FeaturePython)
  Dunit = g/cm3
  Dvalue = 1.46
  Group = -> [C_element115,H_element105,Cl_element028]
  conduct = 2
  density = 1
  expand = 3
  formula = G4_TRICHLOROETHYLENE
  name = G4_TRICHLOROETHYLENE
  specific = 4
FEATURE [App::DocumentObjectGroupPython] C_element116  label="C_element : 063"  # scripted group (container) (typed FeaturePython)
  n = 6
  ref = C_element
FEATURE [App::DocumentObjectGroupPython] H_element106  label="H_element : 15"  # scripted group (container) (typed FeaturePython)
  n = 15
  ref = H_element
FEATURE [App::DocumentObjectGroupPython] O_element099  label="O_element : 053"  # scripted group (container) (typed FeaturePython)
  n = 4
  ref = O_element
FEATURE [App::DocumentObjectGroupPython] P_element012  label="P_element : 1"  # scripted group (container) (typed FeaturePython)
  n = 1
  ref = P_element
FEATURE [App::DocumentObjectGroupPython] G4_TRIETHYL_PHOSPHATE  # scripted group (container) (typed FeaturePython)
  Dunit = g/cm3
  Dvalue = 1.07
  Group = -> [C_element116,H_element106,O_element099,P_element012]
  conduct = 2
  density = 1
  expand = 3
  formula = G4_TRIETHYL_PHOSPHATE
  name = G4_TRIETHYL_PHOSPHATE
  specific = 4
FEATURE [App::DocumentObjectGroupPython] W_element003  label="W_element : 003"  # scripted group (container) (typed FeaturePython)
  n = 1
  ref = W_element
FEATURE [App::DocumentObjectGroupPython] F_element017  label="F_element : 6"  # scripted group (container) (typed FeaturePython)
  n = 6
  ref = F_element
FEATURE [App::DocumentObjectGroupPython] G4_TUNGSTEN_HEXAFLUORIDE  # scripted group (container) (typed FeaturePython)
  Dunit = g/cm3
  Dvalue = 2.4
  Group = -> [W_element003,F_element017]
  conduct = 2
  density = 1
  expand = 3
  formula = G4_TUNGSTEN_HEXAFLUORIDE
  name = G4_TUNGSTEN_HEXAFLUORIDE
  specific = 4
FEATURE [App::DocumentObjectGroupPython] U_element001  label="U_element : 1"  # scripted group (container) (typed FeaturePython)
  n = 1
  ref = U_element
FEATURE [App::DocumentObjectGroupPython] C_element117  label="C_element : 064"  # scripted group (container) (typed FeaturePython)
  n = 2
  ref = C_element
FEATURE [App::DocumentObjectGroupPython] G4_URANIUM_DICARBIDE  # scripted group (container) (typed FeaturePython)
  Dunit = g/cm3
  Dvalue = 11.28
  Group = -> [U_element001,C_element117]
  conduct = 2
  density = 1
  expand = 3
  formula = G4_URANIUM_DICARBIDE
  name = G4_URANIUM_DICARBIDE
  specific = 4
FEATURE [App::DocumentObjectGroupPython] U_element002  label="U_element : 002"  # scripted group (container) (typed FeaturePython)
  n = 1
  ref = U_element
FEATURE [App::DocumentObjectGroupPython] C_element118  label="C_element : 065"  # scripted group (container) (typed FeaturePython)
  n = 1
  ref = C_element
FEATURE [App::DocumentObjectGroupPython] G4_URANIUM_MONOCARBIDE  # scripted group (container) (typed FeaturePython)
  Dunit = g/cm3
  Dvalue = 13.63
  Group = -> [U_element002,C_element118]
  conduct = 2
  density = 1
  expand = 3
  formula = G4_URANIUM_MONOCARBIDE
  name = G4_URANIUM_MONOCARBIDE
  specific = 4
FEATURE [App::DocumentObjectGroupPython] U_element003  label="U_element : 003"  # scripted group (container) (typed FeaturePython)
  n = 1
  ref = U_element
FEATURE [App::DocumentObjectGroupPython] O_element100  label="O_element : 054"  # scripted group (container) (typed FeaturePython)
  n = 2
  ref = O_element
FEATURE [App::DocumentObjectGroupPython] G4_URANIUM_OXIDE  # scripted group (container) (typed FeaturePython)
  Dunit = g/cm3
  Dvalue = 10.96
  Group = -> [U_element003,O_element100]
  conduct = 2
  density = 1
  expand = 3
  formula = G4_URANIUM_OXIDE
  name = G4_URANIUM_OXIDE
  specific = 4
FEATURE [App::DocumentObjectGroupPython] C_element119  label="C_element : 066"  # scripted group (container) (typed FeaturePython)
  n = 1
  ref = C_element
FEATURE [App::DocumentObjectGroupPython] H_element107  label="H_element : 057"  # scripted group (container) (typed FeaturePython)
  n = 4
  ref = H_element
FEATURE [App::DocumentObjectGroupPython] N_element046  label="N_element : 019"  # scripted group (container) (typed FeaturePython)
  n = 2
  ref = N_element
FEATURE [App::DocumentObjectGroupPython] O_element101  label="O_element : 055"  # scripted group (container) (typed FeaturePython)
  n = 1
  ref = O_element
FEATURE [App::DocumentObjectGroupPython] G4_UREA  # scripted group (container) (typed FeaturePython)
  Dunit = g/cm3
  Dvalue = 1.323
  Group = -> [C_element119,H_element107,N_element046,O_element101]
  conduct = 2
  density = 1
  expand = 3
  formula = G4_UREA
  name = G4_UREA
  specific = 4
FEATURE [App::DocumentObjectGroupPython] C_element120  label="C_element : 067"  # scripted group (container) (typed FeaturePython)
  n = 5
  ref = C_element
FEATURE [App::DocumentObjectGroupPython] H_element108  label="H_element : 058"  # scripted group (container) (typed FeaturePython)
  n = 11
  ref = H_element
FEATURE [App::DocumentObjectGroupPython] N_element047  label="N_element : 020"  # scripted group (container) (typed FeaturePython)
  n = 1
  ref = N_element
FEATURE [App::DocumentObjectGroupPython] O_element102  label="O_element : 056"  # scripted group (container) (typed FeaturePython)
  n = 2
  ref = O_element
FEATURE [App::DocumentObjectGroupPython] G4_VALINE  # scripted group (container) (typed FeaturePython)
  Dunit = g/cm3
  Dvalue = 1.23
  Group = -> [C_element120,H_element108,N_element047,O_element102]
  conduct = 2
  density = 1
  expand = 3
  formula = G4_VALINE
  name = G4_VALINE
  specific = 4
FEATURE [App::DocumentObjectGroupPython] H_element109  label="H_element : 0.009"  # scripted group (container) (typed FeaturePython)
  n = 0.009417
FEATURE [App::DocumentObjectGroupPython] C_element121  label="C_element : 0.281"  # scripted group (container) (typed FeaturePython)
  n = 0.280555
FEATURE [App::DocumentObjectGroupPython] F_element018  label="F_element : 0.710"  # scripted group (container) (typed FeaturePython)
  n = 0.710028
FEATURE [App::DocumentObjectGroupPython] G4_VITON  # scripted group (container) (typed FeaturePython)
  Dunit = g/cm3
  Dvalue = 1.8
  Group = -> [H_element109,C_element121,F_element018]
  conduct = 2
  density = 1
  expand = 3
  formula = G4_VITON
  name = G4_VITON
  specific = 4
FEATURE [App::DocumentObjectGroupPython] H_element110  label="H_element : 059"  # scripted group (container) (typed FeaturePython)
  n = 2
  ref = H_element
FEATURE [App::DocumentObjectGroupPython] O_element103  label="O_element : 057"  # scripted group (container) (typed FeaturePython)
  n = 1
  ref = O_element
FEATURE [App::DocumentObjectGroupPython] G4_WATER  # scripted group (container) (typed FeaturePython)
  Dunit = g/cm3
  Dvalue = 1
  Group = -> [H_element110,O_element103]
  conduct = 2
  density = 1
  expand = 3
  formula = G4_WATER
  name = G4_WATER
  specific = 4
FEATURE [App::DocumentObjectGroupPython] H_element111  label="H_element : 060"  # scripted group (container) (typed FeaturePython)
  n = 2
  ref = H_element
FEATURE [App::DocumentObjectGroupPython] O_element104  label="O_element : 058"  # scripted group (container) (typed FeaturePython)
  n = 1
  ref = O_element
FEATURE [App::DocumentObjectGroupPython] G4_WATER_VAPOR  # scripted group (container) (typed FeaturePython)
  Dunit = g/cm3
  Dvalue = 0.000756182
  Group = -> [H_element111,O_element104]
  conduct = 2
  density = 1
  expand = 3
  formula = G4_WATER_VAPOR
  name = G4_WATER_VAPOR
  specific = 4
FEATURE [App::DocumentObjectGroupPython] C_element122  label="C_element : 068"  # scripted group (container) (typed FeaturePython)
  n = 8
  ref = C_element
FEATURE [App::DocumentObjectGroupPython] H_element112  label="H_element : 061"  # scripted group (container) (typed FeaturePython)
  n = 10
  ref = H_element
FEATURE [App::DocumentObjectGroupPython] G4_XYLENE  # scripted group (container) (typed FeaturePython)
  Dunit = g/cm3
  Dvalue = 0.87
  Group = -> [C_element122,H_element112]
  conduct = 2
  density = 1
  expand = 3
  formula = G4_XYLENE
  name = G4_XYLENE
  specific = 4
FEATURE [App::DocumentObjectGroupPython] C_element123  label="C_element : 069"  # scripted group (container) (typed FeaturePython)
  n = 1
  ref = C_element
FEATURE [App::DocumentObjectGroupPython] G4_GRAPHITE  # scripted group (container) (typed FeaturePython)
  Dunit = g/cm3
  Dvalue = 2.21
  Group = -> [C_element123]
  conduct = 2
  density = 1
  expand = 3
  formula = G4_GRAPHITE
  name = G4_GRAPHITE
  specific = 4
FEATURE [App::DocumentObjectGroupPython] NIST  # scripted group (container) (typed FeaturePython)
  Group = -> [G4_A_150_TISSUE,G4_ACETONE,G4_ACETYLENE,G4_ADENINE,G4_ADIPOSE_TISSUE_ICRP,G4_AIR,G4_ALANINE,G4_ALUMINUM_OXIDE,G4_AMBER,G4_AMMONIA,G4_ANILINE,G4_ANTHRACENE,G4_B_100_BONE,G4_BAKELITE,G4_BARIUM_FLUORIDE,G4_BARIUM_SULFATE,G4_BENZENE,G4_BERYLLIUM_OXIDE,G4_BGO,G4_BLOOD_ICRP,G4_BONE_COMPACT_ICRU,G4_BONE_CORTICAL_ICRP,G4_BORON_CARBIDE,G4_BORON_OXIDE,G4_BRAIN_ICRP,G4_BUTANE,G4_N_BUTYL_ALCOHOL,G4_C_552,+152 more]
FEATURE [App::DocumentObjectGroupPython] H_element113  label="H_element : 062"  # scripted group (container) (typed FeaturePython)
  n = 1
  ref = H_element
FEATURE [App::DocumentObjectGroupPython] G4_H  # scripted group (container) (typed FeaturePython)
  Dunit = g/cm3
  Dvalue = 8.3748e-05
  Group = -> [H_element113]
  conduct = 2
  density = 1
  expand = 3
  formula = H
  name = G4_H
  specific = 4
FEATURE [App::DocumentObjectGroupPython] He_element001  label="He_element : 1"  # scripted group (container) (typed FeaturePython)
  n = 1
  ref = He_element
FEATURE [App::DocumentObjectGroupPython] G4_He  # scripted group (container) (typed FeaturePython)
  Dunit = g/cm3
  Dvalue = 0.000166322
  Group = -> [He_element001]
  conduct = 2
  density = 1
  expand = 3
  formula = He
  name = G4_He
  specific = 4
FEATURE [App::DocumentObjectGroupPython] Li_element008  label="Li_element : 008"  # scripted group (container) (typed FeaturePython)
  n = 1
  ref = Li_element
FEATURE [App::DocumentObjectGroupPython] G4_Li  # scripted group (container) (typed FeaturePython)
  Dunit = g/cm3
  Dvalue = 0.534
  Group = -> [Li_element008]
  conduct = 2
  density = 1
  expand = 3
  formula = Li
  name = G4_Li
  specific = 4
FEATURE [App::DocumentObjectGroupPython] Be_element002  label="Be_element : 002"  # scripted group (container) (typed FeaturePython)
  n = 1
  ref = Be_element
FEATURE [App::DocumentObjectGroupPython] G4_Be  # scripted group (container) (typed FeaturePython)
  Dunit = g/cm3
  Dvalue = 1.848
  Group = -> [Be_element002]
  conduct = 2
  density = 1
  expand = 3
  formula = Be
  name = G4_Be
  specific = 4
FEATURE [App::DocumentObjectGroupPython] B_element007  label="B_element : 007"  # scripted group (container) (typed FeaturePython)
  n = 1
  ref = B_element
FEATURE [App::DocumentObjectGroupPython] G4_B  # scripted group (container) (typed FeaturePython)
  Dunit = g/cm3
  Dvalue = 2.37
  Group = -> [B_element007]
  conduct = 2
  density = 1
  expand = 3
  formula = B
  name = G4_B
  specific = 4
FEATURE [App::DocumentObjectGroupPython] C_element124  label="C_element : 070"  # scripted group (container) (typed FeaturePython)
  n = 1
  ref = C_element
FEATURE [App::DocumentObjectGroupPython] G4_C  # scripted group (container) (typed FeaturePython)
  Dunit = g/cm3
  Dvalue = 2
  Group = -> [C_element124]
  conduct = 2
  density = 1
  expand = 3
  formula = C
  name = G4_C
  specific = 4
FEATURE [App::DocumentObjectGroupPython] N_element048  label="N_element : 021"  # scripted group (container) (typed FeaturePython)
  n = 1
  ref = N_element
FEATURE [App::DocumentObjectGroupPython] G4_N  # scripted group (container) (typed FeaturePython)
  Dunit = g/cm3
  Dvalue = 0.0011652
  Group = -> [N_element048]
  conduct = 2
  density = 1
  expand = 3
  formula = N
  name = G4_N
  specific = 4
FEATURE [App::DocumentObjectGroupPython] O_element105  label="O_element : 059"  # scripted group (container) (typed FeaturePython)
  n = 1
  ref = O_element
FEATURE [App::DocumentObjectGroupPython] G4_O  # scripted group (container) (typed FeaturePython)
  Dunit = g/cm3
  Dvalue = 0.00133151
  Group = -> [O_element105]
  conduct = 2
  density = 1
  expand = 3
  formula = O
  name = G4_O
  specific = 4
FEATURE [App::DocumentObjectGroupPython] F_element019  label="F_element : 008"  # scripted group (container) (typed FeaturePython)
  n = 1
  ref = F_element
FEATURE [App::DocumentObjectGroupPython] G4_F  # scripted group (container) (typed FeaturePython)
  Dunit = g/cm3
  Dvalue = 0.00158029
  Group = -> [F_element019]
  conduct = 2
  density = 1
  expand = 3
  formula = F
  name = G4_F
  specific = 4
FEATURE [App::DocumentObjectGroupPython] Ne_element001  label="Ne_element : 1"  # scripted group (container) (typed FeaturePython)
  n = 1
  ref = Ne_element
FEATURE [App::DocumentObjectGroupPython] G4_Ne  # scripted group (container) (typed FeaturePython)
  Dunit = g/cm3
  Dvalue = 0.000838505
  Group = -> [Ne_element001]
  conduct = 2
  density = 1
  expand = 3
  formula = Ne
  name = G4_Ne
  specific = 4
FEATURE [App::DocumentObjectGroupPython] Na_element020  label="Na_element : 005"  # scripted group (container) (typed FeaturePython)
  n = 1
  ref = Na_element
FEATURE [App::DocumentObjectGroupPython] G4_Na  # scripted group (container) (typed FeaturePython)
  Dunit = g/cm3
  Dvalue = 0.971
  Group = -> [Na_element020]
  conduct = 2
  density = 1
  expand = 3
  formula = Na
  name = G4_Na
  specific = 4
FEATURE [App::DocumentObjectGroupPython] Mg_element011  label="Mg_element : 005"  # scripted group (container) (typed FeaturePython)
  n = 1
  ref = Mg_element
FEATURE [App::DocumentObjectGroupPython] G4_Mg  # scripted group (container) (typed FeaturePython)
  Dunit = g/cm3
  Dvalue = 1.74
  Group = -> [Mg_element011]
  conduct = 2
  density = 1
  expand = 3
  formula = Mg
  name = G4_Mg
  specific = 4
FEATURE [App::DocumentObjectGroupPython] Al_element004  label="Al_element : 1"  # scripted group (container) (typed FeaturePython)
  n = 1
  ref = Al_element
FEATURE [App::DocumentObjectGroupPython] G4_Al  # scripted group (container) (typed FeaturePython)
  Dunit = g/cm3
  Dvalue = 2.699
  Group = -> [Al_element004]
  conduct = 2
  density = 1
  expand = 3
  formula = Al
  name = G4_Al
  specific = 4
FEATURE [App::DocumentObjectGroupPython] Si_element007  label="Si_element : 002"  # scripted group (container) (typed FeaturePython)
  n = 1
  ref = Si_element
FEATURE [App::DocumentObjectGroupPython] G4_Si  # scripted group (container) (typed FeaturePython)
  Dunit = g/cm3
  Dvalue = 2.33
  Group = -> [Si_element007]
  conduct = 2
  density = 1
  expand = 3
  formula = Si
  name = G4_Si
  specific = 4
FEATURE [App::DocumentObjectGroupPython] P_element013  label="P_element : 002"  # scripted group (container) (typed FeaturePython)
  n = 1
  ref = P_element
FEATURE [App::DocumentObjectGroupPython] G4_P  # scripted group (container) (typed FeaturePython)
  Dunit = g/cm3
  Dvalue = 2.2
  Group = -> [P_element013]
  conduct = 2
  density = 1
  expand = 3
  formula = P
  name = G4_P
  specific = 4
FEATURE [App::DocumentObjectGroupPython] S_element023  label="S_element : 007"  # scripted group (container) (typed FeaturePython)
  n = 1
  ref = S_element
FEATURE [App::DocumentObjectGroupPython] G4_S  # scripted group (container) (typed FeaturePython)
  Dunit = g/cm3
  Dvalue = 2
  Group = -> [S_element023]
  conduct = 2
  density = 1
  expand = 3
  formula = S
  name = G4_S
  specific = 4
FEATURE [App::DocumentObjectGroupPython] Cl_element029  label="Cl_element : 015"  # scripted group (container) (typed FeaturePython)
  n = 1
  ref = Cl_element
FEATURE [App::DocumentObjectGroupPython] G4_Cl  # scripted group (container) (typed FeaturePython)
  Dunit = g/cm3
  Dvalue = 0.00299473
  Group = -> [Cl_element029]
  conduct = 2
  density = 1
  expand = 3
  formula = Cl
  name = G4_Cl
  specific = 4
FEATURE [App::DocumentObjectGroupPython] Ar_element002  label="Ar_element : 1"  # scripted group (container) (typed FeaturePython)
  n = 1
  ref = Ar_element
FEATURE [App::DocumentObjectGroupPython] G4_Ar  # scripted group (container) (typed FeaturePython)
  Dunit = g/cm3
  Dvalue = 0.00166201
  Group = -> [Ar_element002]
  conduct = 2
  density = 1
  expand = 3
  formula = Ar
  name = G4_Ar
  specific = 4
FEATURE [App::DocumentObjectGroupPython] K_element013  label="K_element : 003"  # scripted group (container) (typed FeaturePython)
  n = 1
  ref = K_element
FEATURE [App::DocumentObjectGroupPython] G4_K  # scripted group (container) (typed FeaturePython)
  Dunit = g/cm3
  Dvalue = 0.862
  Group = -> [K_element013]
  conduct = 2
  density = 1
  expand = 3
  formula = K
  name = G4_K
  specific = 4
FEATURE [App::DocumentObjectGroupPython] Ca_element014  label="Ca_element : 007"  # scripted group (container) (typed FeaturePython)
  n = 1
  ref = Ca_element
FEATURE [App::DocumentObjectGroupPython] G4_Ca  # scripted group (container) (typed FeaturePython)
  Dunit = g/cm3
  Dvalue = 1.55
  Group = -> [Ca_element014]
  conduct = 2
  density = 1
  expand = 3
  formula = Ca
  name = G4_Ca
  specific = 4
FEATURE [App::DocumentObjectGroupPython] Sc_element001  label="Sc_element : 1"  # scripted group (container) (typed FeaturePython)
  n = 1
  ref = Sc_element
FEATURE [App::DocumentObjectGroupPython] G4_Sc  # scripted group (container) (typed FeaturePython)
  Dunit = g/cm3
  Dvalue = 2.989
  Group = -> [Sc_element001]
  conduct = 2
  density = 1
  expand = 3
  formula = Sc
  name = G4_Sc
  specific = 4
FEATURE [App::DocumentObjectGroupPython] Ti_element004  label="Ti_element : 002"  # scripted group (container) (typed FeaturePython)
  n = 1
  ref = Ti_element
FEATURE [App::DocumentObjectGroupPython] G4_Ti  # scripted group (container) (typed FeaturePython)
  Dunit = g/cm3
  Dvalue = 4.54
  Group = -> [Ti_element004]
  conduct = 2
  density = 1
  expand = 3
  formula = Ti
  name = G4_Ti
  specific = 4
FEATURE [App::DocumentObjectGroupPython] V_element001  label="V_element : 1"  # scripted group (container) (typed FeaturePython)
  n = 1
  ref = V_element
FEATURE [App::DocumentObjectGroupPython] G4_V  # scripted group (container) (typed FeaturePython)
  Dunit = g/cm3
  Dvalue = 6.11
  Group = -> [V_element001]
  conduct = 2
  density = 1
  expand = 3
  formula = V
  name = G4_V
  specific = 4
FEATURE [App::DocumentObjectGroupPython] Cr_element001  label="Cr_element : 1"  # scripted group (container) (typed FeaturePython)
  n = 1
  ref = Cr_element
FEATURE [App::DocumentObjectGroupPython] G4_Cr  # scripted group (container) (typed FeaturePython)
  Dunit = g/cm3
  Dvalue = 7.18
  Group = -> [Cr_element001]
  conduct = 2
  density = 1
  expand = 3
  formula = Cr
  name = G4_Cr
  specific = 4
FEATURE [App::DocumentObjectGroupPython] Mn_element001  label="Mn_element : 1"  # scripted group (container) (typed FeaturePython)
  n = 1
  ref = Mn_element
FEATURE [App::DocumentObjectGroupPython] G4_Mn  # scripted group (container) (typed FeaturePython)
  Dunit = g/cm3
  Dvalue = 7.44
  Group = -> [Mn_element001]
  conduct = 2
  density = 1
  expand = 3
  formula = Mn
  name = G4_Mn
  specific = 4
FEATURE [App::DocumentObjectGroupPython] Fe_element007  label="Fe_element : 004"  # scripted group (container) (typed FeaturePython)
  n = 1
  ref = Fe_element
FEATURE [App::DocumentObjectGroupPython] G4_Fe  # scripted group (container) (typed FeaturePython)
  Dunit = g/cm3
  Dvalue = 7.874
  Group = -> [Fe_element007]
  conduct = 2
  density = 1
  expand = 3
  formula = Fe
  name = G4_Fe
  specific = 4
FEATURE [App::DocumentObjectGroupPython] Co_element001  label="Co_element : 1"  # scripted group (container) (typed FeaturePython)
  n = 1
  ref = Co_element
FEATURE [App::DocumentObjectGroupPython] G4_Co  # scripted group (container) (typed FeaturePython)
  Dunit = g/cm3
  Dvalue = 8.9
  Group = -> [Co_element001]
  conduct = 2
  density = 1
  expand = 3
  formula = Co
  name = G4_Co
  specific = 4
FEATURE [App::DocumentObjectGroupPython] Ni_element001  label="Ni_element : 1"  # scripted group (container) (typed FeaturePython)
  n = 1
  ref = Ni_element
FEATURE [App::DocumentObjectGroupPython] G4_Ni  # scripted group (container) (typed FeaturePython)
  Dunit = g/cm3
  Dvalue = 8.902
  Group = -> [Ni_element001]
  conduct = 2
  density = 1
  expand = 3
  formula = Ni
  name = G4_Ni
  specific = 4
FEATURE [App::DocumentObjectGroupPython] Cu_element001  label="Cu_element : 1"  # scripted group (container) (typed FeaturePython)
  n = 1
  ref = Cu_element
FEATURE [App::DocumentObjectGroupPython] G4_Cu  # scripted group (container) (typed FeaturePython)
  Dunit = g/cm3
  Dvalue = 8.96
  Group = -> [Cu_element001]
  conduct = 2
  density = 1
  expand = 3
  formula = Cu
  name = G4_Cu
  specific = 4
FEATURE [App::DocumentObjectGroupPython] Zn_element001  label="Zn_element : 1"  # scripted group (container) (typed FeaturePython)
  n = 1
  ref = Zn_element
FEATURE [App::DocumentObjectGroupPython] G4_Zn  # scripted group (container) (typed FeaturePython)
  Dunit = g/cm3
  Dvalue = 7.133
  Group = -> [Zn_element001]
  conduct = 2
  density = 1
  expand = 3
  formula = Zn
  name = G4_Zn
  specific = 4
FEATURE [App::DocumentObjectGroupPython] Ga_element002  label="Ga_element : 002"  # scripted group (container) (typed FeaturePython)
  n = 1
  ref = Ga_element
FEATURE [App::DocumentObjectGroupPython] G4_Ga  # scripted group (container) (typed FeaturePython)
  Dunit = g/cm3
  Dvalue = 5.904
  Group = -> [Ga_element002]
  conduct = 2
  density = 1
  expand = 3
  formula = Ga
  name = G4_Ga
  specific = 4
FEATURE [App::DocumentObjectGroupPython] Ge_element002  label="Ge_element : 1"  # scripted group (container) (typed FeaturePython)
  n = 1
  ref = Ge_element
FEATURE [App::DocumentObjectGroupPython] G4_Ge  # scripted group (container) (typed FeaturePython)
  Dunit = g/cm3
  Dvalue = 5.323
  Group = -> [Ge_element002]
  conduct = 2
  density = 1
  expand = 3
  formula = Ge
  name = G4_Ge
  specific = 4
FEATURE [App::DocumentObjectGroupPython] As_element003  label="As_element : 002"  # scripted group (container) (typed FeaturePython)
  n = 1
  ref = As_element
FEATURE [App::DocumentObjectGroupPython] G4_As  # scripted group (container) (typed FeaturePython)
  Dunit = g/cm3
  Dvalue = 5.73
  Group = -> [As_element003]
  conduct = 2
  density = 1
  expand = 3
  formula = As
  name = G4_As
  specific = 4
FEATURE [App::DocumentObjectGroupPython] Se_element001  label="Se_element : 1"  # scripted group (container) (typed FeaturePython)
  n = 1
  ref = Se_element
FEATURE [App::DocumentObjectGroupPython] G4_Se  # scripted group (container) (typed FeaturePython)
  Dunit = g/cm3
  Dvalue = 4.5
  Group = -> [Se_element001]
  conduct = 2
  density = 1
  expand = 3
  formula = Se
  name = G4_Se
  specific = 4
FEATURE [App::DocumentObjectGroupPython] Br_element007  label="Br_element : 004"  # scripted group (container) (typed FeaturePython)
  n = 1
  ref = Br_element
FEATURE [App::DocumentObjectGroupPython] G4_Br  # scripted group (container) (typed FeaturePython)
  Dunit = g/cm3
  Dvalue = 0.0070721
  Group = -> [Br_element007]
  conduct = 2
  density = 1
  expand = 3
  formula = Br
  name = G4_Br
  specific = 4
FEATURE [App::DocumentObjectGroupPython] Kr_element001  label="Kr_element : 1"  # scripted group (container) (typed FeaturePython)
  n = 1
  ref = Kr_element
FEATURE [App::DocumentObjectGroupPython] G4_Kr  # scripted group (container) (typed FeaturePython)
  Dunit = g/cm3
  Dvalue = 0.00347832
  Group = -> [Kr_element001]
  conduct = 2
  density = 1
  expand = 3
  formula = Kr
  name = G4_Kr
  specific = 4
FEATURE [App::DocumentObjectGroupPython] Rb_element001  label="Rb_element : 1"  # scripted group (container) (typed FeaturePython)
  n = 1
  ref = Rb_element
FEATURE [App::DocumentObjectGroupPython] G4_Rb  # scripted group (container) (typed FeaturePython)
  Dunit = g/cm3
  Dvalue = 1.532
  Group = -> [Rb_element001]
  conduct = 2
  density = 1
  expand = 3
  formula = Rb
  name = G4_Rb
  specific = 4
FEATURE [App::DocumentObjectGroupPython] Sr_element001  label="Sr_element : 1"  # scripted group (container) (typed FeaturePython)
  n = 1
  ref = Sr_element
FEATURE [App::DocumentObjectGroupPython] G4_Sr  # scripted group (container) (typed FeaturePython)
  Dunit = g/cm3
  Dvalue = 2.54
  Group = -> [Sr_element001]
  conduct = 2
  density = 1
  expand = 3
  formula = Sr
  name = G4_Sr
  specific = 4
FEATURE [App::DocumentObjectGroupPython] Y_element001  label="Y_element : 1"  # scripted group (container) (typed FeaturePython)
  n = 1
  ref = Y_element
FEATURE [App::DocumentObjectGroupPython] G4_Y  # scripted group (container) (typed FeaturePython)
  Dunit = g/cm3
  Dvalue = 4.469
  Group = -> [Y_element001]
  conduct = 2
  density = 1
  expand = 3
  formula = Y
  name = G4_Y
  specific = 4
FEATURE [App::DocumentObjectGroupPython] Zr_element001  label="Zr_element : 1"  # scripted group (container) (typed FeaturePython)
  n = 1
  ref = Zr_element
FEATURE [App::DocumentObjectGroupPython] G4_Zr  # scripted group (container) (typed FeaturePython)
  Dunit = g/cm3
  Dvalue = 6.506
  Group = -> [Zr_element001]
  conduct = 2
  density = 1
  expand = 3
  formula = Zr
  name = G4_Zr
  specific = 4
FEATURE [App::DocumentObjectGroupPython] Nb_element001  label="Nb_element : 1"  # scripted group (container) (typed FeaturePython)
  n = 1
  ref = Nb_element
FEATURE [App::DocumentObjectGroupPython] G4_Nb  # scripted group (container) (typed FeaturePython)
  Dunit = g/cm3
  Dvalue = 8.57
  Group = -> [Nb_element001]
  conduct = 2
  density = 1
  expand = 3
  formula = Nb
  name = G4_Nb
  specific = 4
FEATURE [App::DocumentObjectGroupPython] Mo_element001  label="Mo_element : 1"  # scripted group (container) (typed FeaturePython)
  n = 1
  ref = Mo_element
FEATURE [App::DocumentObjectGroupPython] G4_Mo  # scripted group (container) (typed FeaturePython)
  Dunit = g/cm3
  Dvalue = 10.22
  Group = -> [Mo_element001]
  conduct = 2
  density = 1
  expand = 3
  formula = Mo
  name = G4_Mo
  specific = 4
FEATURE [App::DocumentObjectGroupPython] Tc_element001  label="Tc_element : 1"  # scripted group (container) (typed FeaturePython)
  n = 1
  ref = Tc_element
FEATURE [App::DocumentObjectGroupPython] G4_Tc  # scripted group (container) (typed FeaturePython)
  Dunit = g/cm3
  Dvalue = 11.5
  Group = -> [Tc_element001]
  conduct = 2
  density = 1
  expand = 3
  formula = Tc
  name = G4_Tc
  specific = 4
FEATURE [App::DocumentObjectGroupPython] Ru_element001  label="Ru_element : 1"  # scripted group (container) (typed FeaturePython)
  n = 1
  ref = Ru_element
FEATURE [App::DocumentObjectGroupPython] G4_Ru  # scripted group (container) (typed FeaturePython)
  Dunit = g/cm3
  Dvalue = 12.41
  Group = -> [Ru_element001]
  conduct = 2
  density = 1
  expand = 3
  formula = Ru
  name = G4_Ru
  specific = 4
FEATURE [App::DocumentObjectGroupPython] Rh_element001  label="Rh_element : 1"  # scripted group (container) (typed FeaturePython)
  n = 1
  ref = Rh_element
FEATURE [App::DocumentObjectGroupPython] G4_Rh  # scripted group (container) (typed FeaturePython)
  Dunit = g/cm3
  Dvalue = 12.41
  Group = -> [Rh_element001]
  conduct = 2
  density = 1
  expand = 3
  formula = Rh
  name = G4_Rh
  specific = 4
FEATURE [App::DocumentObjectGroupPython] Pd_element001  label="Pd_element : 1"  # scripted group (container) (typed FeaturePython)
  n = 1
  ref = Pd_element
FEATURE [App::DocumentObjectGroupPython] G4_Pd  # scripted group (container) (typed FeaturePython)
  Dunit = g/cm3
  Dvalue = 12.02
  Group = -> [Pd_element001]
  conduct = 2
  density = 1
  expand = 3
  formula = Pd
  name = G4_Pd
  specific = 4
FEATURE [App::DocumentObjectGroupPython] Ag_element006  label="Ag_element : 004"  # scripted group (container) (typed FeaturePython)
  n = 1
  ref = Ag_element
FEATURE [App::DocumentObjectGroupPython] G4_Ag  # scripted group (container) (typed FeaturePython)
  Dunit = g/cm3
  Dvalue = 10.5
  Group = -> [Ag_element006]
  conduct = 2
  density = 1
  expand = 3
  formula = Ag
  name = G4_Ag
  specific = 4
FEATURE [App::DocumentObjectGroupPython] Cd_element003  label="Cd_element : 003"  # scripted group (container) (typed FeaturePython)
  n = 1
  ref = Cd_element
FEATURE [App::DocumentObjectGroupPython] G4_Cd  # scripted group (container) (typed FeaturePython)
  Dunit = g/cm3
  Dvalue = 8.65
  Group = -> [Cd_element003]
  conduct = 2
  density = 1
  expand = 3
  formula = Cd
  name = G4_Cd
  specific = 4
FEATURE [App::DocumentObjectGroupPython] In_element001  label="In_element : 1"  # scripted group (container) (typed FeaturePython)
  n = 1
  ref = In_element
FEATURE [App::DocumentObjectGroupPython] G4_In  # scripted group (container) (typed FeaturePython)
  Dunit = g/cm3
  Dvalue = 7.31
  Group = -> [In_element001]
  conduct = 2
  density = 1
  expand = 3
  formula = In
  name = G4_In
  specific = 4
FEATURE [App::DocumentObjectGroupPython] Sn_element001  label="Sn_element : 1"  # scripted group (container) (typed FeaturePython)
  n = 1
  ref = Sn_element
FEATURE [App::DocumentObjectGroupPython] G4_Sn  # scripted group (container) (typed FeaturePython)
  Dunit = g/cm3
  Dvalue = 7.31
  Group = -> [Sn_element001]
  conduct = 2
  density = 1
  expand = 3
  formula = Sn
  name = G4_Sn
  specific = 4
FEATURE [App::DocumentObjectGroupPython] Sb_element001  label="Sb_element : 1"  # scripted group (container) (typed FeaturePython)
  n = 1
  ref = Sb_element
FEATURE [App::DocumentObjectGroupPython] G4_Sb  # scripted group (container) (typed FeaturePython)
  Dunit = g/cm3
  Dvalue = 6.691
  Group = -> [Sb_element001]
  conduct = 2
  density = 1
  expand = 3
  formula = Sb
  name = G4_Sb
  specific = 4
FEATURE [App::DocumentObjectGroupPython] Te_element002  label="Te_element : 002"  # scripted group (container) (typed FeaturePython)
  n = 1
  ref = Te_element
FEATURE [App::DocumentObjectGroupPython] G4_Te  # scripted group (container) (typed FeaturePython)
  Dunit = g/cm3
  Dvalue = 6.24
  Group = -> [Te_element002]
  conduct = 2
  density = 1
  expand = 3
  formula = Te
  name = G4_Te
  specific = 4
FEATURE [App::DocumentObjectGroupPython] I_element010  label="I_element : 006"  # scripted group (container) (typed FeaturePython)
  n = 1
  ref = I_element
FEATURE [App::DocumentObjectGroupPython] G4_I  # scripted group (container) (typed FeaturePython)
  Dunit = g/cm3
  Dvalue = 4.93
  Group = -> [I_element010]
  conduct = 2
  density = 1
  expand = 3
  formula = I
  name = G4_I
  specific = 4
FEATURE [App::DocumentObjectGroupPython] Xe_element001  label="Xe_element : 1"  # scripted group (container) (typed FeaturePython)
  n = 1
  ref = Xe_element
FEATURE [App::DocumentObjectGroupPython] G4_Xe  # scripted group (container) (typed FeaturePython)
  Dunit = g/cm3
  Dvalue = 0.00548536
  Group = -> [Xe_element001]
  conduct = 2
  density = 1
  expand = 3
  formula = Xe
  name = G4_Xe
  specific = 4
FEATURE [App::DocumentObjectGroupPython] Cs_element003  label="Cs_element : 003"  # scripted group (container) (typed FeaturePython)
  n = 1
  ref = Cs_element
FEATURE [App::DocumentObjectGroupPython] G4_Cs  # scripted group (container) (typed FeaturePython)
  Dunit = g/cm3
  Dvalue = 1.873
  Group = -> [Cs_element003]
  conduct = 2
  density = 1
  expand = 3
  formula = Cs
  name = G4_Cs
  specific = 4
FEATURE [App::DocumentObjectGroupPython] Ba_element003  label="Ba_element : 003"  # scripted group (container) (typed FeaturePython)
  n = 1
  ref = Ba_element
FEATURE [App::DocumentObjectGroupPython] G4_Ba  # scripted group (container) (typed FeaturePython)
  Dunit = g/cm3
  Dvalue = 3.5
  Group = -> [Ba_element003]
  conduct = 2
  density = 1
  expand = 3
  formula = Ba
  name = G4_Ba
  specific = 4
FEATURE [App::DocumentObjectGroupPython] La_element003  label="La_element : 003"  # scripted group (container) (typed FeaturePython)
  n = 1
  ref = La_element
FEATURE [App::DocumentObjectGroupPython] G4_La  # scripted group (container) (typed FeaturePython)
  Dunit = g/cm3
  Dvalue = 6.154
  Group = -> [La_element003]
  conduct = 2
  density = 1
  expand = 3
  formula = La
  name = G4_La
  specific = 4
FEATURE [App::DocumentObjectGroupPython] Ce_element002  label="Ce_element : 1"  # scripted group (container) (typed FeaturePython)
  n = 1
  ref = Ce_element
FEATURE [App::DocumentObjectGroupPython] G4_Ce  # scripted group (container) (typed FeaturePython)
  Dunit = g/cm3
  Dvalue = 6.657
  Group = -> [Ce_element002]
  conduct = 2
  density = 1
  expand = 3
  formula = Ce
  name = G4_Ce
  specific = 4
FEATURE [App::DocumentObjectGroupPython] Pr_element001  label="Pr_element : 1"  # scripted group (container) (typed FeaturePython)
  n = 1
  ref = Pr_element
FEATURE [App::DocumentObjectGroupPython] G4_Pr  # scripted group (container) (typed FeaturePython)
  Dunit = g/cm3
  Dvalue = 6.71
  Group = -> [Pr_element001]
  conduct = 2
  density = 1
  expand = 3
  formula = Pr
  name = G4_Pr
  specific = 4
FEATURE [App::DocumentObjectGroupPython] Nd_element001  label="Nd_element : 1"  # scripted group (container) (typed FeaturePython)
  n = 1
  ref = Nd_element
FEATURE [App::DocumentObjectGroupPython] G4_Nd  # scripted group (container) (typed FeaturePython)
  Dunit = g/cm3
  Dvalue = 6.9
  Group = -> [Nd_element001]
  conduct = 2
  density = 1
  expand = 3
  formula = Nd
  name = G4_Nd
  specific = 4
FEATURE [App::DocumentObjectGroupPython] Pm_element001  label="Pm_element : 1"  # scripted group (container) (typed FeaturePython)
  n = 1
  ref = Pm_element
FEATURE [App::DocumentObjectGroupPython] G4_Pm  # scripted group (container) (typed FeaturePython)
  Dunit = g/cm3
  Dvalue = 7.22
  Group = -> [Pm_element001]
  conduct = 2
  density = 1
  expand = 3
  formula = Pm
  name = G4_Pm
  specific = 4
FEATURE [App::DocumentObjectGroupPython] Sm_element001  label="Sm_element : 1"  # scripted group (container) (typed FeaturePython)
  n = 1
  ref = Sm_element
FEATURE [App::DocumentObjectGroupPython] G4_Sm  # scripted group (container) (typed FeaturePython)
  Dunit = g/cm3
  Dvalue = 7.46
  Group = -> [Sm_element001]
  conduct = 2
  density = 1
  expand = 3
  formula = Sm
  name = G4_Sm
  specific = 4
FEATURE [App::DocumentObjectGroupPython] Eu_element001  label="Eu_element : 1"  # scripted group (container) (typed FeaturePython)
  n = 1
  ref = Eu_element
FEATURE [App::DocumentObjectGroupPython] G4_Eu  # scripted group (container) (typed FeaturePython)
  Dunit = g/cm3
  Dvalue = 5.243
  Group = -> [Eu_element001]
  conduct = 2
  density = 1
  expand = 3
  formula = Eu
  name = G4_Eu
  specific = 4
FEATURE [App::DocumentObjectGroupPython] Gd_element002  label="Gd_element : 1"  # scripted group (container) (typed FeaturePython)
  n = 1
  ref = Gd_element
FEATURE [App::DocumentObjectGroupPython] G4_Gd  # scripted group (container) (typed FeaturePython)
  Dunit = g/cm3
  Dvalue = 7.9004
  Group = -> [Gd_element002]
  conduct = 2
  density = 1
  expand = 3
  formula = Gd
  name = G4_Gd
  specific = 4
FEATURE [App::DocumentObjectGroupPython] Tb_element001  label="Tb_element : 1"  # scripted group (container) (typed FeaturePython)
  n = 1
  ref = Tb_element
FEATURE [App::DocumentObjectGroupPython] G4_Tb  # scripted group (container) (typed FeaturePython)
  Dunit = g/cm3
  Dvalue = 8.229
  Group = -> [Tb_element001]
  conduct = 2
  density = 1
  expand = 3
  formula = Tb
  name = G4_Tb
  specific = 4
FEATURE [App::DocumentObjectGroupPython] Dy_element001  label="Dy_element : 1"  # scripted group (container) (typed FeaturePython)
  n = 1
  ref = Dy_element
FEATURE [App::DocumentObjectGroupPython] G4_Dy  # scripted group (container) (typed FeaturePython)
  Dunit = g/cm3
  Dvalue = 8.55
  Group = -> [Dy_element001]
  conduct = 2
  density = 1
  expand = 3
  formula = Dy
  name = G4_Dy
  specific = 4
FEATURE [App::DocumentObjectGroupPython] Ho_element001  label="Ho_element : 1"  # scripted group (container) (typed FeaturePython)
  n = 1
  ref = Ho_element
FEATURE [App::DocumentObjectGroupPython] G4_Ho  # scripted group (container) (typed FeaturePython)
  Dunit = g/cm3
  Dvalue = 8.795
  Group = -> [Ho_element001]
  conduct = 2
  density = 1
  expand = 3
  formula = Ho
  name = G4_Ho
  specific = 4
FEATURE [App::DocumentObjectGroupPython] Er_element001  label="Er_element : 1"  # scripted group (container) (typed FeaturePython)
  n = 1
  ref = Er_element
FEATURE [App::DocumentObjectGroupPython] G4_Er  # scripted group (container) (typed FeaturePython)
  Dunit = g/cm3
  Dvalue = 9.066
  Group = -> [Er_element001]
  conduct = 2
  density = 1
  expand = 3
  formula = Er
  name = G4_Er
  specific = 4
FEATURE [App::DocumentObjectGroupPython] Tm_element001  label="Tm_element : 1"  # scripted group (container) (typed FeaturePython)
  n = 1
  ref = Tm_element
FEATURE [App::DocumentObjectGroupPython] G4_Tm  # scripted group (container) (typed FeaturePython)
  Dunit = g/cm3
  Dvalue = 9.321
  Group = -> [Tm_element001]
  conduct = 2
  density = 1
  expand = 3
  formula = Tm
  name = G4_Tm
  specific = 4
FEATURE [App::DocumentObjectGroupPython] Yb_element001  label="Yb_element : 1"  # scripted group (container) (typed FeaturePython)
  n = 1
  ref = Yb_element
FEATURE [App::DocumentObjectGroupPython] G4_Yb  # scripted group (container) (typed FeaturePython)
  Dunit = g/cm3
  Dvalue = 6.73
  Group = -> [Yb_element001]
  conduct = 2
  density = 1
  expand = 3
  formula = Yb
  name = G4_Yb
  specific = 4
FEATURE [App::DocumentObjectGroupPython] Lu_element001  label="Lu_element : 1"  # scripted group (container) (typed FeaturePython)
  n = 1
  ref = Lu_element
FEATURE [App::DocumentObjectGroupPython] G4_Lu  # scripted group (container) (typed FeaturePython)
  Dunit = g/cm3
  Dvalue = 9.84
  Group = -> [Lu_element001]
  conduct = 2
  density = 1
  expand = 3
  formula = Lu
  name = G4_Lu
  specific = 4
FEATURE [App::DocumentObjectGroupPython] Hf_element001  label="Hf_element : 1"  # scripted group (container) (typed FeaturePython)
  n = 1
  ref = Hf_element
FEATURE [App::DocumentObjectGroupPython] G4_Hf  # scripted group (container) (typed FeaturePython)
  Dunit = g/cm3
  Dvalue = 13.31
  Group = -> [Hf_element001]
  conduct = 2
  density = 1
  expand = 3
  formula = Hf
  name = G4_Hf
  specific = 4
FEATURE [App::DocumentObjectGroupPython] Ta_element001  label="Ta_element : 1"  # scripted group (container) (typed FeaturePython)
  n = 1
  ref = Ta_element
FEATURE [App::DocumentObjectGroupPython] G4_Ta  # scripted group (container) (typed FeaturePython)
  Dunit = g/cm3
  Dvalue = 16.654
  Group = -> [Ta_element001]
  conduct = 2
  density = 1
  expand = 3
  formula = Ta
  name = G4_Ta
  specific = 4
FEATURE [App::DocumentObjectGroupPython] W_element004  label="W_element : 004"  # scripted group (container) (typed FeaturePython)
  n = 1
  ref = W_element
FEATURE [App::DocumentObjectGroupPython] G4_W  # scripted group (container) (typed FeaturePython)
  Dunit = g/cm3
  Dvalue = 19.3
  Group = -> [W_element004]
  conduct = 2
  density = 1
  expand = 3
  formula = W
  name = G4_W
  specific = 4
FEATURE [App::DocumentObjectGroupPython] Re_element001  label="Re_element : 1"  # scripted group (container) (typed FeaturePython)
  n = 1
  ref = Re_element
FEATURE [App::DocumentObjectGroupPython] G4_Re  # scripted group (container) (typed FeaturePython)
  Dunit = g/cm3
  Dvalue = 21.02
  Group = -> [Re_element001]
  conduct = 2
  density = 1
  expand = 3
  formula = Re
  name = G4_Re
  specific = 4
FEATURE [App::DocumentObjectGroupPython] Os_element001  label="Os_element : 1"  # scripted group (container) (typed FeaturePython)
  n = 1
  ref = Os_element
FEATURE [App::DocumentObjectGroupPython] G4_Os  # scripted group (container) (typed FeaturePython)
  Dunit = g/cm3
  Dvalue = 22.57
  Group = -> [Os_element001]
  conduct = 2
  density = 1
  expand = 3
  formula = Os
  name = G4_Os
  specific = 4
FEATURE [App::DocumentObjectGroupPython] Ir_element001  label="Ir_element : 1"  # scripted group (container) (typed FeaturePython)
  n = 1
  ref = Ir_element
FEATURE [App::DocumentObjectGroupPython] G4_Ir  # scripted group (container) (typed FeaturePython)
  Dunit = g/cm3
  Dvalue = 22.42
  Group = -> [Ir_element001]
  conduct = 2
  density = 1
  expand = 3
  formula = Ir
  name = G4_Ir
  specific = 4
FEATURE [App::DocumentObjectGroupPython] Pt_element001  label="Pt_element : 1"  # scripted group (container) (typed FeaturePython)
  n = 1
  ref = Pt_element
FEATURE [App::DocumentObjectGroupPython] G4_Pt  # scripted group (container) (typed FeaturePython)
  Dunit = g/cm3
  Dvalue = 21.45
  Group = -> [Pt_element001]
  conduct = 2
  density = 1
  expand = 3
  formula = Pt
  name = G4_Pt
  specific = 4
FEATURE [App::DocumentObjectGroupPython] Au_element001  label="Au_element : 1"  # scripted group (container) (typed FeaturePython)
  n = 1
  ref = Au_element
FEATURE [App::DocumentObjectGroupPython] G4_Au  # scripted group (container) (typed FeaturePython)
  Dunit = g/cm3
  Dvalue = 19.32
  Group = -> [Au_element001]
  conduct = 2
  density = 1
  expand = 3
  formula = Au
  name = G4_Au
  specific = 4
FEATURE [App::DocumentObjectGroupPython] Hg_element002  label="Hg_element : 002"  # scripted group (container) (typed FeaturePython)
  n = 1
  ref = Hg_element
FEATURE [App::DocumentObjectGroupPython] G4_Hg  # scripted group (container) (typed FeaturePython)
  Dunit = g/cm3
  Dvalue = 13.546
  Group = -> [Hg_element002]
  conduct = 2
  density = 1
  expand = 3
  formula = Hg
  name = G4_Hg
  specific = 4
FEATURE [App::DocumentObjectGroupPython] Tl_element002  label="Tl_element : 002"  # scripted group (container) (typed FeaturePython)
  n = 1
  ref = Tl_element
FEATURE [App::DocumentObjectGroupPython] G4_Tl  # scripted group (container) (typed FeaturePython)
  Dunit = g/cm3
  Dvalue = 11.72
  Group = -> [Tl_element002]
  conduct = 2
  density = 1
  expand = 3
  formula = Tl
  name = G4_Tl
  specific = 4
FEATURE [App::DocumentObjectGroupPython] Pb_element003  label="Pb_element : 1"  # scripted group (container) (typed FeaturePython)
  n = 1
  ref = Pb_element
FEATURE [App::DocumentObjectGroupPython] G4_Pb  # scripted group (container) (typed FeaturePython)
  Dunit = g/cm3
  Dvalue = 11.35
  Group = -> [Pb_element003]
  conduct = 2
  density = 1
  expand = 3
  formula = Pb
  name = G4_Pb
  specific = 4
FEATURE [App::DocumentObjectGroupPython] Bi_element002  label="Bi_element : 1"  # scripted group (container) (typed FeaturePython)
  n = 1
  ref = Bi_element
FEATURE [App::DocumentObjectGroupPython] G4_Bi  # scripted group (container) (typed FeaturePython)
  Dunit = g/cm3
  Dvalue = 9.747
  Group = -> [Bi_element002]
  conduct = 2
  density = 1
  expand = 3
  formula = Bi
  name = G4_Bi
  specific = 4
FEATURE [App::DocumentObjectGroupPython] Po_element001  label="Po_element : 1"  # scripted group (container) (typed FeaturePython)
  n = 1
  ref = Po_element
FEATURE [App::DocumentObjectGroupPython] G4_Po  # scripted group (container) (typed FeaturePython)
  Dunit = g/cm3
  Dvalue = 9.32
  Group = -> [Po_element001]
  conduct = 2
  density = 1
  expand = 3
  formula = Po
  name = G4_Po
  specific = 4
FEATURE [App::DocumentObjectGroupPython] At_element001  label="At_element : 1"  # scripted group (container) (typed FeaturePython)
  n = 1
  ref = At_element
FEATURE [App::DocumentObjectGroupPython] G4_At  # scripted group (container) (typed FeaturePython)
  Dunit = g/cm3
  Dvalue = 9.32
  Group = -> [At_element001]
  conduct = 2
  density = 1
  expand = 3
  formula = At
  name = G4_At
  specific = 4
FEATURE [App::DocumentObjectGroupPython] Rn_element001  label="Rn_element : 1"  # scripted group (container) (typed FeaturePython)
  n = 1
  ref = Rn_element
FEATURE [App::DocumentObjectGroupPython] G4_Rn  # scripted group (container) (typed FeaturePython)
  Dunit = g/cm3
  Dvalue = 0.00900662
  Group = -> [Rn_element001]
  conduct = 2
  density = 1
  expand = 3
  formula = Rn
  name = G4_Rn
  specific = 4
FEATURE [App::DocumentObjectGroupPython] Fr_element001  label="Fr_element : 1"  # scripted group (container) (typed FeaturePython)
  n = 1
  ref = Fr_element
FEATURE [App::DocumentObjectGroupPython] G4_Fr  # scripted group (container) (typed FeaturePython)
  Dunit = g/cm3
  Dvalue = 1
  Group = -> [Fr_element001]
  conduct = 2
  density = 1
  expand = 3
  formula = Fr
  name = G4_Fr
  specific = 4
FEATURE [App::DocumentObjectGroupPython] Ra_element001  label="Ra_element : 1"  # scripted group (container) (typed FeaturePython)
  n = 1
  ref = Ra_element
FEATURE [App::DocumentObjectGroupPython] G4_Ra  # scripted group (container) (typed FeaturePython)
  Dunit = g/cm3
  Dvalue = 5
  Group = -> [Ra_element001]
  conduct = 2
  density = 1
  expand = 3
  formula = Ra
  name = G4_Ra
  specific = 4
FEATURE [App::DocumentObjectGroupPython] Ac_element001  label="Ac_element : 1"  # scripted group (container) (typed FeaturePython)
  n = 1
  ref = Ac_element
FEATURE [App::DocumentObjectGroupPython] G4_Ac  # scripted group (container) (typed FeaturePython)
  Dunit = g/cm3
  Dvalue = 10.07
  Group = -> [Ac_element001]
  conduct = 2
  density = 1
  expand = 3
  formula = Ac
  name = G4_Ac
  specific = 4
FEATURE [App::DocumentObjectGroupPython] Th_element001  label="Th_element : 1"  # scripted group (container) (typed FeaturePython)
  n = 1
  ref = Th_element
FEATURE [App::DocumentObjectGroupPython] G4_Th  # scripted group (container) (typed FeaturePython)
  Dunit = g/cm3
  Dvalue = 11.72
  Group = -> [Th_element001]
  conduct = 2
  density = 1
  expand = 3
  formula = Th
  name = G4_Th
  specific = 4
FEATURE [App::DocumentObjectGroupPython] Pa_element001  label="Pa_element : 1"  # scripted group (container) (typed FeaturePython)
  n = 1
  ref = Pa_element
FEATURE [App::DocumentObjectGroupPython] G4_Pa  # scripted group (container) (typed FeaturePython)
  Dunit = g/cm3
  Dvalue = 15.37
  Group = -> [Pa_element001]
  conduct = 2
  density = 1
  expand = 3
  formula = Pa
  name = G4_Pa
  specific = 4
FEATURE [App::DocumentObjectGroupPython] U_element004  label="U_element : 004"  # scripted group (container) (typed FeaturePython)
  n = 1
  ref = U_element
FEATURE [App::DocumentObjectGroupPython] G4_U  # scripted group (container) (typed FeaturePython)
  Dunit = g/cm3
  Dvalue = 18.95
  Group = -> [U_element004]
  conduct = 2
  density = 1
  expand = 3
  formula = U
  name = G4_U
  specific = 4
FEATURE [App::DocumentObjectGroupPython] Np_element001  label="Np_element : 1"  # scripted group (container) (typed FeaturePython)
  n = 1
  ref = Np_element
FEATURE [App::DocumentObjectGroupPython] G4_Np  # scripted group (container) (typed FeaturePython)
  Dunit = g/cm3
  Dvalue = 20.25
  Group = -> [Np_element001]
  conduct = 2
  density = 1
  expand = 3
  formula = Np
  name = G4_Np
  specific = 4
FEATURE [App::DocumentObjectGroupPython] Pu_element002  label="Pu_element : 002"  # scripted group (container) (typed FeaturePython)
  n = 1
  ref = Pu_element
FEATURE [App::DocumentObjectGroupPython] G4_Pu  # scripted group (container) (typed FeaturePython)
  Dunit = g/cm3
  Dvalue = 19.84
  Group = -> [Pu_element002]
  conduct = 2
  density = 1
  expand = 3
  formula = Pu
  name = G4_Pu
  specific = 4
FEATURE [App::DocumentObjectGroupPython] Am_element001  label="Am_element : 1"  # scripted group (container) (typed FeaturePython)
  n = 1
  ref = Am_element
FEATURE [App::DocumentObjectGroupPython] G4_Am  # scripted group (container) (typed FeaturePython)
  Dunit = g/cm3
  Dvalue = 13.67
  Group = -> [Am_element001]
  conduct = 2
  density = 1
  expand = 3
  formula = Am
  name = G4_Am
  specific = 4
FEATURE [App::DocumentObjectGroupPython] Cm_element001  label="Cm_element : 1"  # scripted group (container) (typed FeaturePython)
  n = 1
  ref = Cm_element
FEATURE [App::DocumentObjectGroupPython] G4_Cm  # scripted group (container) (typed FeaturePython)
  Dunit = g/cm3
  Dvalue = 13.51
  Group = -> [Cm_element001]
  conduct = 2
  density = 1
  expand = 3
  formula = Cm
  name = G4_Cm
  specific = 4
FEATURE [App::DocumentObjectGroupPython] Bk_element001  label="Bk_element : 1"  # scripted group (container) (typed FeaturePython)
  n = 1
  ref = Bk_element
FEATURE [App::DocumentObjectGroupPython] G4_Bk  # scripted group (container) (typed FeaturePython)
  Dunit = g/cm3
  Dvalue = 14
  Group = -> [Bk_element001]
  conduct = 2
  density = 1
  expand = 3
  formula = Bk
  name = G4_Bk
  specific = 4
FEATURE [App::DocumentObjectGroupPython] Cf_element001  label="Cf_element : 1"  # scripted group (container) (typed FeaturePython)
  n = 1
  ref = Cf_element
FEATURE [App::DocumentObjectGroupPython] G4_Cf  # scripted group (container) (typed FeaturePython)
  Dunit = g/cm3
  Dvalue = 10
  Group = -> [Cf_element001]
  conduct = 2
  density = 1
  expand = 3
  formula = Cf
  name = G4_Cf
  specific = 4
FEATURE [App::DocumentObjectGroupPython] Element  # scripted group (container) (typed FeaturePython)
  Group = -> [G4_H,G4_He,G4_Li,G4_Be,G4_B,G4_C,G4_N,G4_O,G4_F,G4_Ne,G4_Na,G4_Mg,G4_Al,G4_Si,G4_P,G4_S,G4_Cl,G4_Ar,G4_K,G4_Ca,G4_Sc,G4_Ti,G4_V,G4_Cr,G4_Mn,G4_Fe,G4_Co,G4_Ni,G4_Cu,G4_Zn,G4_Ga,G4_Ge,G4_As,G4_Se,G4_Br,G4_Kr,G4_Rb,G4_Sr,G4_Y,G4_Zr,G4_Nb,G4_Mo,G4_Tc,G4_Ru,G4_Rh,G4_Pd,G4_Ag,G4_Cd,G4_In,G4_Sn,G4_Sb,G4_Te,G4_I,G4_Xe,G4_Cs,G4_Ba,G4_La,G4_Ce,G4_Pr,G4_Nd,G4_Pm,G4_Sm,G4_Eu,G4_Gd,G4_Tb,G4_Dy,G4_Ho,G4_Er,+30 more]
FEATURE [App::DocumentObjectGroupPython] H_element114  label="H_element : 063"  # scripted group (container) (typed FeaturePython)
  n = 2
  ref = H_element
FEATURE [App::DocumentObjectGroupPython] G4_lH2  # scripted group (container) (typed FeaturePython)
  Dunit = g/cm3
  Dvalue = 0.0708
  Group = -> [H_element114]
  conduct = 2
  density = 1
  expand = 3
  formula = G4_lH2
  name = G4_lH2
  specific = 4
FEATURE [App::DocumentObjectGroupPython] N_element049  label="N_element : 022"  # scripted group (container) (typed FeaturePython)
  n = 2
  ref = N_element
FEATURE [App::DocumentObjectGroupPython] G4_lN2  # scripted group (container) (typed FeaturePython)
  Dunit = g/cm3
  Dvalue = 0.807
  Group = -> [N_element049]
  conduct = 2
  density = 1
  expand = 3
  formula = G4_lN2
  name = G4_lN2
  specific = 4
FEATURE [App::DocumentObjectGroupPython] O_element106  label="O_element : 060"  # scripted group (container) (typed FeaturePython)
  n = 2
  ref = O_element
FEATURE [App::DocumentObjectGroupPython] G4_lO2  # scripted group (container) (typed FeaturePython)
  Dunit = g/cm3
  Dvalue = 1.141
  Group = -> [O_element106]
  conduct = 2
  density = 1
  expand = 3
  formula = G4_lO2
  name = G4_lO2
  specific = 4
FEATURE [App::DocumentObjectGroupPython] Ar  label="Ar : 1"  # scripted group (container) (typed FeaturePython)
  n = 1
  ref = Ar
FEATURE [App::DocumentObjectGroupPython] G4_lAr  # scripted group (container) (typed FeaturePython)
  Dunit = g/cm3
  Dvalue = 1.396
  Group = -> [Ar]
  conduct = 2
  density = 1
  expand = 3
  formula = G4_lAr
  name = G4_lAr
  specific = 4
FEATURE [App::DocumentObjectGroupPython] Br  label="Br : 1"  # scripted group (container) (typed FeaturePython)
  n = 1
  ref = Br
FEATURE [App::DocumentObjectGroupPython] G4_lBr  # scripted group (container) (typed FeaturePython)
  Dunit = g/cm3
  Dvalue = 3.1028
  Group = -> [Br]
  conduct = 2
  density = 1
  expand = 3
  formula = G4_lBr
  name = G4_lBr
  specific = 4
FEATURE [App::DocumentObjectGroupPython] Kr  label="Kr : 1"  # scripted group (container) (typed FeaturePython)
  n = 1
  ref = Kr
FEATURE [App::DocumentObjectGroupPython] G4_lKr  # scripted group (container) (typed FeaturePython)
  Dunit = g/cm3
  Dvalue = 2.418
  Group = -> [Kr]
  conduct = 2
  density = 1
  expand = 3
  formula = G4_lKr
  name = G4_lKr
  specific = 4
FEATURE [App::DocumentObjectGroupPython] Xe  label="Xe : 1"  # scripted group (container) (typed FeaturePython)
  n = 1
  ref = Xe
FEATURE [App::DocumentObjectGroupPython] G4_lXe  # scripted group (container) (typed FeaturePython)
  Dunit = g/cm3
  Dvalue = 2.953
  Group = -> [Xe]
  conduct = 2
  density = 1
  expand = 3
  formula = G4_lXe
  name = G4_lXe
  specific = 4
FEATURE [App::DocumentObjectGroupPython] O_element107  label="O_element : 061"  # scripted group (container) (typed FeaturePython)
  n = 4
  ref = O_element
FEATURE [App::DocumentObjectGroupPython] Pb_element004  label="Pb_element : 002"  # scripted group (container) (typed FeaturePython)
  n = 1
  ref = Pb_element
FEATURE [App::DocumentObjectGroupPython] W_element005  label="W_element : 005"  # scripted group (container) (typed FeaturePython)
  n = 1
  ref = W_element
FEATURE [App::DocumentObjectGroupPython] G4_PbWO4  # scripted group (container) (typed FeaturePython)
  Dunit = g/cm3
  Dvalue = 8.28
  Group = -> [O_element107,Pb_element004,W_element005]
  conduct = 2
  density = 1
  expand = 3
  formula = G4_PbWO4
  name = G4_PbWO4
  specific = 4
FEATURE [App::DocumentObjectGroupPython] alactic  label="alactic : 1"  # scripted group (container) (typed FeaturePython)
  n = 1
  ref = alactic
FEATURE [App::DocumentObjectGroupPython] G4_Galactic  # scripted group (container) (typed FeaturePython)
  Dunit = g/cm3
  Dvalue = 0
  Group = -> [alactic]
  conduct = 2
  density = 1
  expand = 3
  formula = G4_Galactic
  name = G4_Galactic
  specific = 4
FEATURE [App::DocumentObjectGroupPython] RAPHITE_POROUS  label="RAPHITE_POROUS : 1"  # scripted group (container) (typed FeaturePython)
  n = 1
  ref = RAPHITE_POROUS
FEATURE [App::DocumentObjectGroupPython] G4_GRAPHITE_POROUS  # scripted group (container) (typed FeaturePython)
  Dunit = g/cm3
  Dvalue = 1.7
  Group = -> [RAPHITE_POROUS]
  conduct = 2
  density = 1
  expand = 3
  formula = G4_GRAPHITE_POROUS
  name = G4_GRAPHITE_POROUS
  specific = 4
FEATURE [App::DocumentObjectGroupPython] H_element115  label="H_element : 0.150"  # scripted group (container) (typed FeaturePython)
  n = 0.080538
FEATURE [App::DocumentObjectGroupPython] C_element125  label="C_element : 0.600"  # scripted group (container) (typed FeaturePython)
  n = 0.599848
FEATURE [App::DocumentObjectGroupPython] O_element108  label="O_element : 0.320"  # scripted group (container) (typed FeaturePython)
  n = 0.319614
FEATURE [App::DocumentObjectGroupPython] G4_LUCITE  # scripted group (container) (typed FeaturePython)
  Dunit = g/cm3
  Dvalue = 1.19
  Group = -> [H_element115,C_element125,O_element108]
  conduct = 2
  density = 1
  expand = 3
  formula = G4_LUCITE
  name = G4_LUCITE
  specific = 4
FEATURE [App::DocumentObjectGroupPython] Cu_element002  label="Cu_element : 62"  # scripted group (container) (typed FeaturePython)
  n = 62
  ref = Cu_element
FEATURE [App::DocumentObjectGroupPython] Zn_element002  label="Zn_element : 35"  # scripted group (container) (typed FeaturePython)
  n = 35
  ref = Zn_element
FEATURE [App::DocumentObjectGroupPython] Pb_element005  label="Pb_element : 3"  # scripted group (container) (typed FeaturePython)
  n = 3
  ref = Pb_element
FEATURE [App::DocumentObjectGroupPython] G4_BRASS  # scripted group (container) (typed FeaturePython)
  Dunit = g/cm3
  Dvalue = 8.52
  Group = -> [Cu_element002,Zn_element002,Pb_element005]
  conduct = 2
  density = 1
  expand = 3
  formula = G4_BRASS
  name = G4_BRASS
  specific = 4
FEATURE [App::DocumentObjectGroupPython] Cu_element003  label="Cu_element : 89"  # scripted group (container) (typed FeaturePython)
  n = 89
  ref = Cu_element
FEATURE [App::DocumentObjectGroupPython] Zn_element003  label="Zn_element : 9"  # scripted group (container) (typed FeaturePython)
  n = 9
  ref = Zn_element
FEATURE [App::DocumentObjectGroupPython] Pb_element006  label="Pb_element : 2"  # scripted group (container) (typed FeaturePython)
  n = 2
  ref = Pb_element
FEATURE [App::DocumentObjectGroupPython] G4_BRONZE  # scripted group (container) (typed FeaturePython)
  Dunit = g/cm3
  Dvalue = 8.82
  Group = -> [Cu_element003,Zn_element003,Pb_element006]
  conduct = 2
  density = 1
  expand = 3
  formula = G4_BRONZE
  name = G4_BRONZE
  specific = 4
FEATURE [App::DocumentObjectGroupPython] Fe_element008  label="Fe_element : 74"  # scripted group (container) (typed FeaturePython)
  n = 74
  ref = Fe_element
FEATURE [App::DocumentObjectGroupPython] Cr_element002  label="Cr_element : 18"  # scripted group (container) (typed FeaturePython)
  n = 18
  ref = Cr_element
FEATURE [App::DocumentObjectGroupPython] Ni_element002  label="Ni_element : 8"  # scripted group (container) (typed FeaturePython)
  n = 8
  ref = Ni_element
FEATURE [App::DocumentObjectGroupPython] G4_STAINLESS_STEEL  label="G4_STAINLESS-STEEL"  # scripted group (container) (typed FeaturePython)
  Dunit = g/cm3
  Dvalue = 8
  Group = -> [Fe_element008,Cr_element002,Ni_element002]
  conduct = 2
  density = 1
  expand = 3
  formula = G4_STAINLESS-STEEL
  name = G4_STAINLESS-STEEL
  specific = 4
FEATURE [App::DocumentObjectGroupPython] H_element116  label="H_element : 064"  # scripted group (container) (typed FeaturePython)
  n = 18
  ref = H_element
FEATURE [App::DocumentObjectGroupPython] C_element126  label="C_element : 071"  # scripted group (container) (typed FeaturePython)
  n = 12
  ref = C_element
FEATURE [App::DocumentObjectGroupPython] O_element109  label="O_element : 062"  # scripted group (container) (typed FeaturePython)
  n = 7
  ref = O_element
FEATURE [App::DocumentObjectGroupPython] G4_CR39  # scripted group (container) (typed FeaturePython)
  Dunit = g/cm3
  Dvalue = 1.32
  Group = -> [H_element116,C_element126,O_element109]
  conduct = 2
  density = 1
  expand = 3
  formula = G4_CR39
  name = G4_CR39
  specific = 4
FEATURE [App::DocumentObjectGroupPython] H_element117  label="H_element : 38"  # scripted group (container) (typed FeaturePython)
  n = 38
  ref = H_element
FEATURE [App::DocumentObjectGroupPython] C_element127  label="C_element : 072"  # scripted group (container) (typed FeaturePython)
  n = 18
  ref = C_element
FEATURE [App::DocumentObjectGroupPython] O_element110  label="O_element : 063"  # scripted group (container) (typed FeaturePython)
  n = 1
  ref = O_element
FEATURE [App::DocumentObjectGroupPython] G4_OCTADECANOL  # scripted group (container) (typed FeaturePython)
  Dunit = g/cm3
  Dvalue = 0.812
  Group = -> [H_element117,C_element127,O_element110]
  conduct = 2
  density = 1
  expand = 3
  formula = G4_OCTADECANOL
  name = G4_OCTADECANOL
  specific = 4
FEATURE [App::DocumentObjectGroupPython] HEP  # scripted group (container) (typed FeaturePython)
  Group = -> [G4_lH2,G4_lN2,G4_lO2,G4_lAr,G4_lBr,G4_lKr,G4_lXe,G4_PbWO4,G4_Galactic,G4_GRAPHITE_POROUS,G4_LUCITE,G4_BRASS,G4_BRONZE,G4_STAINLESS_STEEL,G4_CR39,G4_OCTADECANOL]
FEATURE [App::DocumentObjectGroupPython] C_element128  label="C_element : 073"  # scripted group (container) (typed FeaturePython)
  n = 14
  ref = C_element
FEATURE [App::DocumentObjectGroupPython] H_element118  label="H_element : 065"  # scripted group (container) (typed FeaturePython)
  n = 10
  ref = H_element
FEATURE [App::DocumentObjectGroupPython] O_element111  label="O_element : 064"  # scripted group (container) (typed FeaturePython)
  n = 2
  ref = O_element
FEATURE [App::DocumentObjectGroupPython] N_element050  label="N_element : 023"  # scripted group (container) (typed FeaturePython)
  n = 2
  ref = N_element
FEATURE [App::DocumentObjectGroupPython] G4_KEVLAR  # scripted group (container) (typed FeaturePython)
  Dunit = g/cm3
  Dvalue = 1.44
  Group = -> [C_element128,H_element118,O_element111,N_element050]
  conduct = 2
  density = 1
  expand = 3
  formula = G4_KEVLAR
  name = G4_KEVLAR
  specific = 4
FEATURE [App::DocumentObjectGroupPython] C_element129  label="C_element : 074"  # scripted group (container) (typed FeaturePython)
  n = 10
  ref = C_element
FEATURE [App::DocumentObjectGroupPython] H_element119  label="H_element : 066"  # scripted group (container) (typed FeaturePython)
  n = 8
  ref = H_element
FEATURE [App::DocumentObjectGroupPython] O_element112  label="O_element : 065"  # scripted group (container) (typed FeaturePython)
  n = 4
  ref = O_element
FEATURE [App::DocumentObjectGroupPython] G4_DACRON  # scripted group (container) (typed FeaturePython)
  Dunit = g/cm3
  Dvalue = 1.4
  Group = -> [C_element129,H_element119,O_element112]
  conduct = 2
  density = 1
  expand = 3
  formula = G4_DACRON
  name = G4_DACRON
  specific = 4
FEATURE [App::DocumentObjectGroupPython] C_element130  label="C_element : 075"  # scripted group (container) (typed FeaturePython)
  n = 4
  ref = C_element
FEATURE [App::DocumentObjectGroupPython] H_element120  label="H_element : 067"  # scripted group (container) (typed FeaturePython)
  n = 5
  ref = H_element
FEATURE [App::DocumentObjectGroupPython] Cl_element030  label="Cl_element : 016"  # scripted group (container) (typed FeaturePython)
  n = 1
  ref = Cl_element
FEATURE [App::DocumentObjectGroupPython] G4_NEOPRENE  # scripted group (container) (typed FeaturePython)
  Dunit = g/cm3
  Dvalue = 1.23
  Group = -> [C_element130,H_element120,Cl_element030]
  conduct = 2
  density = 1
  expand = 3
  formula = G4_NEOPRENE
  name = G4_NEOPRENE
  specific = 4
FEATURE [App::DocumentObjectGroupPython] Space  # scripted group (container) (typed FeaturePython)
  Group = -> [G4_KEVLAR,G4_DACRON,G4_NEOPRENE]
FEATURE [App::DocumentObjectGroupPython] H_element121  label="H_element : 068"  # scripted group (container) (typed FeaturePython)
  n = 5
  ref = H_element
FEATURE [App::DocumentObjectGroupPython] C_element131  label="C_element : 076"  # scripted group (container) (typed FeaturePython)
  n = 4
  ref = C_element
FEATURE [App::DocumentObjectGroupPython] N_element051  label="N_element : 3"  # scripted group (container) (typed FeaturePython)
  n = 3
  ref = N_element
FEATURE [App::DocumentObjectGroupPython] O_element113  label="O_element : 066"  # scripted group (container) (typed FeaturePython)
  n = 1
  ref = O_element
FEATURE [App::DocumentObjectGroupPython] G4_CYTOSINE  # scripted group (container) (typed FeaturePython)
  Dunit = g/cm3
  Dvalue = 1.55
  Group = -> [H_element121,C_element131,N_element051,O_element113]
  conduct = 2
  density = 1
  expand = 3
  formula = G4_CYTOSINE
  name = G4_CYTOSINE
  specific = 4
FEATURE [App::DocumentObjectGroupPython] H_element122  label="H_element : 069"  # scripted group (container) (typed FeaturePython)
  n = 6
  ref = H_element
FEATURE [App::DocumentObjectGroupPython] C_element132  label="C_element : 077"  # scripted group (container) (typed FeaturePython)
  n = 5
  ref = C_element
FEATURE [App::DocumentObjectGroupPython] N_element052  label="N_element : 024"  # scripted group (container) (typed FeaturePython)
  n = 2
  ref = N_element
FEATURE [App::DocumentObjectGroupPython] O_element114  label="O_element : 067"  # scripted group (container) (typed FeaturePython)
  n = 2
  ref = O_element
FEATURE [App::DocumentObjectGroupPython] G4_THYMINE  # scripted group (container) (typed FeaturePython)
  Dunit = g/cm3
  Dvalue = 1.23
  Group = -> [H_element122,C_element132,N_element052,O_element114]
  conduct = 2
  density = 1
  expand = 3
  formula = G4_THYMINE
  name = G4_THYMINE
  specific = 4
FEATURE [App::DocumentObjectGroupPython] H_element123  label="H_element : 070"  # scripted group (container) (typed FeaturePython)
  n = 4
  ref = H_element
FEATURE [App::DocumentObjectGroupPython] C_element133  label="C_element : 078"  # scripted group (container) (typed FeaturePython)
  n = 4
  ref = C_element
FEATURE [App::DocumentObjectGroupPython] N_element053  label="N_element : 025"  # scripted group (container) (typed FeaturePython)
  n = 2
  ref = N_element
FEATURE [App::DocumentObjectGroupPython] O_element115  label="O_element : 068"  # scripted group (container) (typed FeaturePython)
  n = 2
  ref = O_element
FEATURE [App::DocumentObjectGroupPython] G4_URACIL  # scripted group (container) (typed FeaturePython)
  Dunit = g/cm3
  Dvalue = 1.32
  Group = -> [H_element123,C_element133,N_element053,O_element115]
  conduct = 2
  density = 1
  expand = 3
  formula = G4_URACIL
  name = G4_URACIL
  specific = 4
FEATURE [App::DocumentObjectGroupPython] H_element124  label="H_element : 071"  # scripted group (container) (typed FeaturePython)
  n = 4
  ref = H_element
FEATURE [App::DocumentObjectGroupPython] C_element134  label="C_element : 079"  # scripted group (container) (typed FeaturePython)
  n = 5
  ref = C_element
FEATURE [App::DocumentObjectGroupPython] N_element054  label="N_element : 026"  # scripted group (container) (typed FeaturePython)
  n = 5
  ref = N_element
FEATURE [App::DocumentObjectGroupPython] G4_DNA_ADENINE  # scripted group (container) (typed FeaturePython)
  Dunit = g/cm3
  Dvalue = 1
  Group = -> [H_element124,C_element134,N_element054]
  conduct = 2
  density = 1
  expand = 3
  formula = G4_DNA_ADENINE
  name = G4_DNA_ADENINE
  specific = 4
FEATURE [App::DocumentObjectGroupPython] H_element125  label="H_element : 072"  # scripted group (container) (typed FeaturePython)
  n = 4
  ref = H_element
FEATURE [App::DocumentObjectGroupPython] C_element135  label="C_element : 080"  # scripted group (container) (typed FeaturePython)
  n = 5
  ref = C_element
FEATURE [App::DocumentObjectGroupPython] N_element055  label="N_element : 027"  # scripted group (container) (typed FeaturePython)
  n = 5
  ref = N_element
FEATURE [App::DocumentObjectGroupPython] O_element116  label="O_element : 069"  # scripted group (container) (typed FeaturePython)
  n = 1
  ref = O_element
FEATURE [App::DocumentObjectGroupPython] G4_DNA_GUANINE  # scripted group (container) (typed FeaturePython)
  Dunit = g/cm3
  Dvalue = 1
  Group = -> [H_element125,C_element135,N_element055,O_element116]
  conduct = 2
  density = 1
  expand = 3
  formula = G4_DNA_GUANINE
  name = G4_DNA_GUANINE
  specific = 4
FEATURE [App::DocumentObjectGroupPython] H_element126  label="H_element : 073"  # scripted group (container) (typed FeaturePython)
  n = 4
  ref = H_element
FEATURE [App::DocumentObjectGroupPython] C_element136  label="C_element : 081"  # scripted group (container) (typed FeaturePython)
  n = 4
  ref = C_element
FEATURE [App::DocumentObjectGroupPython] N_element056  label="N_element : 028"  # scripted group (container) (typed FeaturePython)
  n = 3
  ref = N_element
FEATURE [App::DocumentObjectGroupPython] O_element117  label="O_element : 070"  # scripted group (container) (typed FeaturePython)
  n = 1
  ref = O_element
FEATURE [App::DocumentObjectGroupPython] G4_DNA_CYTOSINE  # scripted group (container) (typed FeaturePython)
  Dunit = g/cm3
  Dvalue = 1
  Group = -> [H_element126,C_element136,N_element056,O_element117]
  conduct = 2
  density = 1
  expand = 3
  formula = G4_DNA_CYTOSINE
  name = G4_DNA_CYTOSINE
  specific = 4
FEATURE [App::DocumentObjectGroupPython] H_element127  label="H_element : 074"  # scripted group (container) (typed FeaturePython)
  n = 5
  ref = H_element
FEATURE [App::DocumentObjectGroupPython] C_element137  label="C_element : 082"  # scripted group (container) (typed FeaturePython)
  n = 5
  ref = C_element
FEATURE [App::DocumentObjectGroupPython] N_element057  label="N_element : 029"  # scripted group (container) (typed FeaturePython)
  n = 2
  ref = N_element
FEATURE [App::DocumentObjectGroupPython] O_element118  label="O_element : 071"  # scripted group (container) (typed FeaturePython)
  n = 2
  ref = O_element
FEATURE [App::DocumentObjectGroupPython] G4_DNA_THYMINE  # scripted group (container) (typed FeaturePython)
  Dunit = g/cm3
  Dvalue = 1
  Group = -> [H_element127,C_element137,N_element057,O_element118]
  conduct = 2
  density = 1
  expand = 3
  formula = G4_DNA_THYMINE
  name = G4_DNA_THYMINE
  specific = 4
FEATURE [App::DocumentObjectGroupPython] H_element128  label="H_element : 075"  # scripted group (container) (typed FeaturePython)
  n = 3
  ref = H_element
FEATURE [App::DocumentObjectGroupPython] C_element138  label="C_element : 083"  # scripted group (container) (typed FeaturePython)
  n = 4
  ref = C_element
FEATURE [App::DocumentObjectGroupPython] N_element058  label="N_element : 030"  # scripted group (container) (typed FeaturePython)
  n = 2
  ref = N_element
FEATURE [App::DocumentObjectGroupPython] O_element119  label="O_element : 072"  # scripted group (container) (typed FeaturePython)
  n = 2
  ref = O_element
FEATURE [App::DocumentObjectGroupPython] G4_DNA_URACIL  # scripted group (container) (typed FeaturePython)
  Dunit = g/cm3
  Dvalue = 1
  Group = -> [H_element128,C_element138,N_element058,O_element119]
  conduct = 2
  density = 1
  expand = 3
  formula = G4_DNA_URACIL
  name = G4_DNA_URACIL
  specific = 4
FEATURE [App::DocumentObjectGroupPython] H_element129  label="H_element : 076"  # scripted group (container) (typed FeaturePython)
  n = 10
  ref = H_element
FEATURE [App::DocumentObjectGroupPython] C_element139  label="C_element : 084"  # scripted group (container) (typed FeaturePython)
  n = 10
  ref = C_element
FEATURE [App::DocumentObjectGroupPython] N_element059  label="N_element : 031"  # scripted group (container) (typed FeaturePython)
  n = 5
  ref = N_element
FEATURE [App::DocumentObjectGroupPython] O_element120  label="O_element : 073"  # scripted group (container) (typed FeaturePython)
  n = 4
  ref = O_element
FEATURE [App::DocumentObjectGroupPython] G4_DNA_ADENOSINE  # scripted group (container) (typed FeaturePython)
  Dunit = g/cm3
  Dvalue = 1
  Group = -> [H_element129,C_element139,N_element059,O_element120]
  conduct = 2
  density = 1
  expand = 3
  formula = G4_DNA_ADENOSINE
  name = G4_DNA_ADENOSINE
  specific = 4
FEATURE [App::DocumentObjectGroupPython] H_element130  label="H_element : 077"  # scripted group (container) (typed FeaturePython)
  n = 10
  ref = H_element
FEATURE [App::DocumentObjectGroupPython] C_element140  label="C_element : 085"  # scripted group (container) (typed FeaturePython)
  n = 10
  ref = C_element
FEATURE [App::DocumentObjectGroupPython] N_element060  label="N_element : 032"  # scripted group (container) (typed FeaturePython)
  n = 5
  ref = N_element
FEATURE [App::DocumentObjectGroupPython] O_element121  label="O_element : 074"  # scripted group (container) (typed FeaturePython)
  n = 5
  ref = O_element
FEATURE [App::DocumentObjectGroupPython] G4_DNA_GUANOSINE  # scripted group (container) (typed FeaturePython)
  Dunit = g/cm3
  Dvalue = 1
  Group = -> [H_element130,C_element140,N_element060,O_element121]
  conduct = 2
  density = 1
  expand = 3
  formula = G4_DNA_GUANOSINE
  name = G4_DNA_GUANOSINE
  specific = 4
FEATURE [App::DocumentObjectGroupPython] H_element131  label="H_element : 078"  # scripted group (container) (typed FeaturePython)
  n = 10
  ref = H_element
FEATURE [App::DocumentObjectGroupPython] C_element141  label="C_element : 086"  # scripted group (container) (typed FeaturePython)
  n = 9
  ref = C_element
FEATURE [App::DocumentObjectGroupPython] N_element061  label="N_element : 033"  # scripted group (container) (typed FeaturePython)
  n = 3
  ref = N_element
FEATURE [App::DocumentObjectGroupPython] O_element122  label="O_element : 075"  # scripted group (container) (typed FeaturePython)
  n = 5
  ref = O_element
FEATURE [App::DocumentObjectGroupPython] G4_DNA_CYTIDINE  # scripted group (container) (typed FeaturePython)
  Dunit = g/cm3
  Dvalue = 1
  Group = -> [H_element131,C_element141,N_element061,O_element122]
  conduct = 2
  density = 1
  expand = 3
  formula = G4_DNA_CYTIDINE
  name = G4_DNA_CYTIDINE
  specific = 4
FEATURE [App::DocumentObjectGroupPython] H_element132  label="H_element : 079"  # scripted group (container) (typed FeaturePython)
  n = 9
  ref = H_element
FEATURE [App::DocumentObjectGroupPython] C_element142  label="C_element : 087"  # scripted group (container) (typed FeaturePython)
  n = 9
  ref = C_element
FEATURE [App::DocumentObjectGroupPython] N_element062  label="N_element : 034"  # scripted group (container) (typed FeaturePython)
  n = 2
  ref = N_element
FEATURE [App::DocumentObjectGroupPython] O_element123  label="O_element : 076"  # scripted group (container) (typed FeaturePython)
  n = 6
  ref = O_element
FEATURE [App::DocumentObjectGroupPython] G4_DNA_URIDINE  # scripted group (container) (typed FeaturePython)
  Dunit = g/cm3
  Dvalue = 1
  Group = -> [H_element132,C_element142,N_element062,O_element123]
  conduct = 2
  density = 1
  expand = 3
  formula = G4_DNA_URIDINE
  name = G4_DNA_URIDINE
  specific = 4
FEATURE [App::DocumentObjectGroupPython] H_element133  label="H_element : 080"  # scripted group (container) (typed FeaturePython)
  n = 11
  ref = H_element
FEATURE [App::DocumentObjectGroupPython] C_element143  label="C_element : 088"  # scripted group (container) (typed FeaturePython)
  n = 10
  ref = C_element
FEATURE [App::DocumentObjectGroupPython] N_element063  label="N_element : 035"  # scripted group (container) (typed FeaturePython)
  n = 2
  ref = N_element
FEATURE [App::DocumentObjectGroupPython] O_element124  label="O_element : 077"  # scripted group (container) (typed FeaturePython)
  n = 6
  ref = O_element
FEATURE [App::DocumentObjectGroupPython] G4_DNA_METHYLURIDINE  # scripted group (container) (typed FeaturePython)
  Dunit = g/cm3
  Dvalue = 1
  Group = -> [H_element133,C_element143,N_element063,O_element124]
  conduct = 2
  density = 1
  expand = 3
  formula = G4_DNA_METHYLURIDINE
  name = G4_DNA_METHYLURIDINE
  specific = 4
FEATURE [App::DocumentObjectGroupPython] P_element014  label="P_element : 003"  # scripted group (container) (typed FeaturePython)
  n = 1
  ref = P_element
FEATURE [App::DocumentObjectGroupPython] O_element125  label="O_element : 078"  # scripted group (container) (typed FeaturePython)
  n = 3
  ref = O_element
FEATURE [App::DocumentObjectGroupPython] G4_DNA_MONOPHOSPHATE  # scripted group (container) (typed FeaturePython)
  Dunit = g/cm3
  Dvalue = 1
  Group = -> [P_element014,O_element125]
  conduct = 2
  density = 1
  expand = 3
  formula = G4_DNA_MONOPHOSPHATE
  name = G4_DNA_MONOPHOSPHATE
  specific = 4
FEATURE [App::DocumentObjectGroupPython] H_element134  label="H_element : 081"  # scripted group (container) (typed FeaturePython)
  n = 10
  ref = H_element
FEATURE [App::DocumentObjectGroupPython] C_element144  label="C_element : 089"  # scripted group (container) (typed FeaturePython)
  n = 10
  ref = C_element
FEATURE [App::DocumentObjectGroupPython] N_element064  label="N_element : 036"  # scripted group (container) (typed FeaturePython)
  n = 5
  ref = N_element
FEATURE [App::DocumentObjectGroupPython] O_element126  label="O_element : 079"  # scripted group (container) (typed FeaturePython)
  n = 7
  ref = O_element
FEATURE [App::DocumentObjectGroupPython] P_element015  label="P_element : 004"  # scripted group (container) (typed FeaturePython)
  n = 1
  ref = P_element
FEATURE [App::DocumentObjectGroupPython] G4_DNA_A  # scripted group (container) (typed FeaturePython)
  Dunit = g/cm3
  Dvalue = 1
  Group = -> [H_element134,C_element144,N_element064,O_element126,P_element015]
  conduct = 2
  density = 1
  expand = 3
  formula = G4_DNA_A
  name = G4_DNA_A
  specific = 4
FEATURE [App::DocumentObjectGroupPython] H_element135  label="H_element : 082"  # scripted group (container) (typed FeaturePython)
  n = 10
  ref = H_element
FEATURE [App::DocumentObjectGroupPython] C_element145  label="C_element : 090"  # scripted group (container) (typed FeaturePython)
  n = 10
  ref = C_element
FEATURE [App::DocumentObjectGroupPython] N_element065  label="N_element : 037"  # scripted group (container) (typed FeaturePython)
  n = 5
  ref = N_element
FEATURE [App::DocumentObjectGroupPython] O_element127  label="O_element : 8"  # scripted group (container) (typed FeaturePython)
  n = 8
  ref = O_element
FEATURE [App::DocumentObjectGroupPython] P_element016  label="P_element : 005"  # scripted group (container) (typed FeaturePython)
  n = 1
  ref = P_element
FEATURE [App::DocumentObjectGroupPython] G4_DNA_G  # scripted group (container) (typed FeaturePython)
  Dunit = g/cm3
  Dvalue = 1
  Group = -> [H_element135,C_element145,N_element065,O_element127,P_element016]
  conduct = 2
  density = 1
  expand = 3
  formula = G4_DNA_G
  name = G4_DNA_G
  specific = 4
FEATURE [App::DocumentObjectGroupPython] H_element136  label="H_element : 083"  # scripted group (container) (typed FeaturePython)
  n = 10
  ref = H_element
FEATURE [App::DocumentObjectGroupPython] C_element146  label="C_element : 091"  # scripted group (container) (typed FeaturePython)
  n = 9
  ref = C_element
FEATURE [App::DocumentObjectGroupPython] N_element066  label="N_element : 038"  # scripted group (container) (typed FeaturePython)
  n = 3
  ref = N_element
FEATURE [App::DocumentObjectGroupPython] O_element128  label="O_element : 080"  # scripted group (container) (typed FeaturePython)
  n = 8
  ref = O_element
FEATURE [App::DocumentObjectGroupPython] P_element017  label="P_element : 006"  # scripted group (container) (typed FeaturePython)
  n = 1
  ref = P_element
FEATURE [App::DocumentObjectGroupPython] G4_DNA_C  # scripted group (container) (typed FeaturePython)
  Dunit = g/cm3
  Dvalue = 1
  Group = -> [H_element136,C_element146,N_element066,O_element128,P_element017]
  conduct = 2
  density = 1
  expand = 3
  formula = G4_DNA_C
  name = G4_DNA_C
  specific = 4
FEATURE [App::DocumentObjectGroupPython] H_element137  label="H_element : 084"  # scripted group (container) (typed FeaturePython)
  n = 9
  ref = H_element
FEATURE [App::DocumentObjectGroupPython] C_element147  label="C_element : 092"  # scripted group (container) (typed FeaturePython)
  n = 9
  ref = C_element
FEATURE [App::DocumentObjectGroupPython] N_element067  label="N_element : 039"  # scripted group (container) (typed FeaturePython)
  n = 2
  ref = N_element
FEATURE [App::DocumentObjectGroupPython] O_element129  label="O_element : 9"  # scripted group (container) (typed FeaturePython)
  n = 9
  ref = O_element
FEATURE [App::DocumentObjectGroupPython] P_element018  label="P_element : 007"  # scripted group (container) (typed FeaturePython)
  n = 1
  ref = P_element
FEATURE [App::DocumentObjectGroupPython] G4_DNA_U  # scripted group (container) (typed FeaturePython)
  Dunit = g/cm3
  Dvalue = 1
  Group = -> [H_element137,C_element147,N_element067,O_element129,P_element018]
  conduct = 2
  density = 1
  expand = 3
  formula = G4_DNA_U
  name = G4_DNA_U
  specific = 4
FEATURE [App::DocumentObjectGroupPython] H_element138  label="H_element : 085"  # scripted group (container) (typed FeaturePython)
  n = 11
  ref = H_element
FEATURE [App::DocumentObjectGroupPython] C_element148  label="C_element : 093"  # scripted group (container) (typed FeaturePython)
  n = 10
  ref = C_element
FEATURE [App::DocumentObjectGroupPython] N_element068  label="N_element : 040"  # scripted group (container) (typed FeaturePython)
  n = 2
  ref = N_element
FEATURE [App::DocumentObjectGroupPython] O_element130  label="O_element : 081"  # scripted group (container) (typed FeaturePython)
  n = 9
  ref = O_element
FEATURE [App::DocumentObjectGroupPython] P_element019  label="P_element : 008"  # scripted group (container) (typed FeaturePython)
  n = 1
  ref = P_element
FEATURE [App::DocumentObjectGroupPython] G4_DNA_MU  # scripted group (container) (typed FeaturePython)
  Dunit = g/cm3
  Dvalue = 1
  Group = -> [H_element138,C_element148,N_element068,O_element130,P_element019]
  conduct = 2
  density = 1
  expand = 3
  formula = G4_DNA_MU
  name = G4_DNA_MU
  specific = 4
FEATURE [App::DocumentObjectGroupPython] BioChemical  # scripted group (container) (typed FeaturePython)
  Group = -> [G4_CYTOSINE,G4_THYMINE,G4_URACIL,G4_DNA_ADENINE,G4_DNA_GUANINE,G4_DNA_CYTOSINE,G4_DNA_THYMINE,G4_DNA_URACIL,G4_DNA_ADENOSINE,G4_DNA_GUANOSINE,G4_DNA_CYTIDINE,G4_DNA_URIDINE,G4_DNA_METHYLURIDINE,G4_DNA_MONOPHOSPHATE,G4_DNA_A,G4_DNA_G,G4_DNA_C,G4_DNA_U,G4_DNA_MU]
FEATURE [App::DocumentObjectGroupPython] G4Materials  # scripted group (container) (typed FeaturePython)
  Group = -> [NIST,Element,HEP,Space,BioChemical]
  version = 1
FEATURE [App::DocumentObjectGroupPython] Geant4  # scripted group (container) (typed FeaturePython)
  Group = -> [G4Isotopes,G4Elements,G4Materials]
FEATURE [App::DocumentObjectGroupPython] Materials  # scripted group (container) (typed FeaturePython)
  Group = -> [Geant4]
FEATURE [Part::FeaturePython] GDMLBox_WorldBox  # WARN: FeaturePython — macro-defined, semantics opaque (R4)
  lunit = 2
  material = 5
  x = 100
  y = 100
  z = 100
FEATURE [Sketcher::SketchObject] Sketch001
  FullyConstrained = false
  Placement = pos=(0,0,0) rot=(1,0,0;1.5708rad)
  sketch-geometry (15):
    g0-g7: Circle x8 (B-spline internal-alignment scaffolding for g8; pole/knot coordinates omitted)
    g8: BSplineCurve PolesCount=8 KnotsCount=6 Degree=3 IsPeriodic=0
    g9-g14: GeomPoint x6 (B-spline internal-alignment scaffolding for g8; pole/knot coordinates omitted)
  constraints (5):
    c: Weight(g0) = 1
    c: Equal(g0, g1-g7) x7
    c: Coincident(g7,g0)
    c: InternalAlignment(g0-g7 -> g8) x8
    c: InternalAlignment(g9-g14 -> g8) x6
FEATURE [Part::Revolution] Revolve
  Angle = 360
  Axis = (0,0,1)
  Base = (0,0,0)
  FaceMakerClass = Part::FaceMakerBullseye
  Solid = true
  Source = -> Sketch001
  Symmetric = false
  material = 5
FEATURE [App::Part] Part
  Group = -> [Sketch001,Revolve]
  Origin = -> Origin001
FEATURE [App::Part] worldVOL
  Group = -> [GDMLBox_WorldBox,Part]
  Origin = -> Origin
